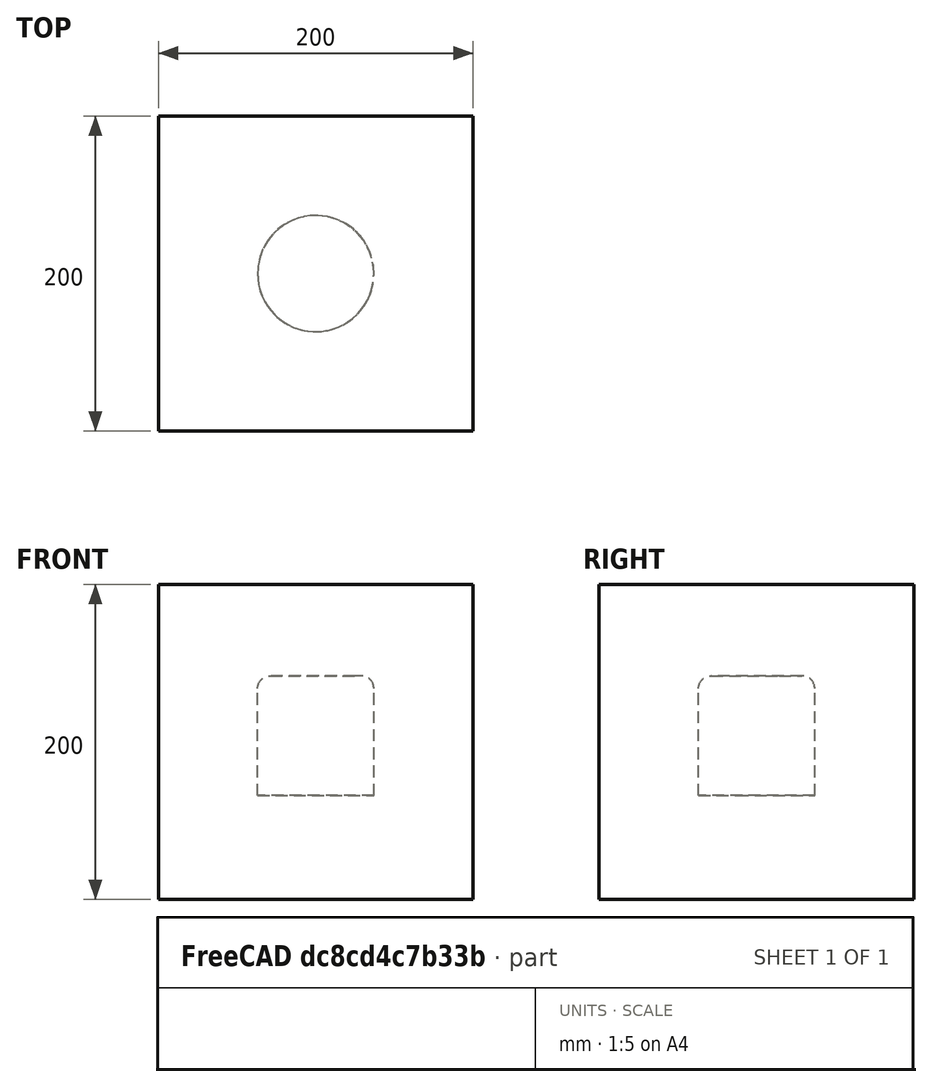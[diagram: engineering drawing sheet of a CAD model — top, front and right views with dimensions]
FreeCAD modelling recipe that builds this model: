
FCSTD DOCUMENT  (FreeCAD 1.0R39109 (Git))
Label: assemblyTest-B
License: All rights reserved
LicenseURL: http://en.wikipedia.org/wiki/All_rights_reserved
objects: App::DocumentObjectGroupPython×1254, Part::FeaturePython×4, App::Part×3, Part::Fuse×2
note: 6 computed .brp shape members not serialized (recipe doc carries the construction recipe); baked Part::Feature solids carry a one-line shape summary decoded from their .brp

FEATURE [App::DocumentObjectGroupPython] HALFPI  # scripted group (container) (typed FeaturePython)
  name = HALFPI
  value = pi/2.
FEATURE [App::DocumentObjectGroupPython] PI  # scripted group (container) (typed FeaturePython)
  name = PI
  value = 1.*pi
FEATURE [App::DocumentObjectGroupPython] TWOPI  # scripted group (container) (typed FeaturePython)
  name = TWOPI
  value = 2.*pi
FEATURE [App::DocumentObjectGroupPython] Variables  # scripted group (container) (typed FeaturePython)
FEATURE [App::DocumentObjectGroupPython] Quantities  # scripted group (container) (typed FeaturePython)
FEATURE [App::DocumentObjectGroupPython] Isotopes  # scripted group (container) (typed FeaturePython)
FEATURE [App::DocumentObjectGroupPython] Elements  # scripted group (container) (typed FeaturePython)
FEATURE [App::DocumentObjectGroupPython] G4Isotopes  # scripted group (container) (typed FeaturePython)
FEATURE [App::DocumentObjectGroupPython] H_element  # scripted group (container) (typed FeaturePython)
  Z = 1
  atom_value = 1.008
  formula = H
  name = H_element
FEATURE [App::DocumentObjectGroupPython] He_element  # scripted group (container) (typed FeaturePython)
  Z = 2
  atom_value = 4.0026
  formula = He
  name = He_element
FEATURE [App::DocumentObjectGroupPython] Li_element  # scripted group (container) (typed FeaturePython)
  Z = 3
  atom_value = 6.94
  formula = Li
  name = Li_element
FEATURE [App::DocumentObjectGroupPython] Be_element  # scripted group (container) (typed FeaturePython)
  Z = 4
  atom_value = 9.01218
  formula = Be
  name = Be_element
FEATURE [App::DocumentObjectGroupPython] B_element  # scripted group (container) (typed FeaturePython)
  Z = 5
  atom_value = 10.81
  formula = B
  name = B_element
FEATURE [App::DocumentObjectGroupPython] C_element  # scripted group (container) (typed FeaturePython)
  Z = 6
  atom_value = 12.011
  formula = C
  name = C_element
FEATURE [App::DocumentObjectGroupPython] N_element  # scripted group (container) (typed FeaturePython)
  Z = 7
  atom_value = 14.007
  formula = N
  name = N_element
FEATURE [App::DocumentObjectGroupPython] O_element  # scripted group (container) (typed FeaturePython)
  Z = 8
  atom_value = 15.999
  formula = O
  name = O_element
FEATURE [App::DocumentObjectGroupPython] F_element  # scripted group (container) (typed FeaturePython)
  Z = 9
  atom_value = 18.9984
  formula = F
  name = F_element
FEATURE [App::DocumentObjectGroupPython] Ne_element  # scripted group (container) (typed FeaturePython)
  Z = 10
  atom_value = 20.1797
  formula = Ne
  name = Ne_element
FEATURE [App::DocumentObjectGroupPython] Na_element  # scripted group (container) (typed FeaturePython)
  Z = 11
  atom_value = 22.9898
  formula = Na
  name = Na_element
FEATURE [App::DocumentObjectGroupPython] Mg_element  # scripted group (container) (typed FeaturePython)
  Z = 12
  atom_value = 24.305
  formula = Mg
  name = Mg_element
FEATURE [App::DocumentObjectGroupPython] Al_element  # scripted group (container) (typed FeaturePython)
  Z = 13
  atom_value = 26.9815
  formula = Al
  name = Al_element
FEATURE [App::DocumentObjectGroupPython] Si_element  # scripted group (container) (typed FeaturePython)
  Z = 14
  atom_value = 28.085
  formula = Si
  name = Si_element
FEATURE [App::DocumentObjectGroupPython] P_element  # scripted group (container) (typed FeaturePython)
  Z = 15
  atom_value = 30.9738
  formula = P
  name = P_element
FEATURE [App::DocumentObjectGroupPython] S_element  # scripted group (container) (typed FeaturePython)
  Z = 16
  atom_value = 32.06
  formula = S
  name = S_element
FEATURE [App::DocumentObjectGroupPython] Cl_element  # scripted group (container) (typed FeaturePython)
  Z = 17
  atom_value = 35.45
  formula = Cl
  name = Cl_element
FEATURE [App::DocumentObjectGroupPython] Ar_element  # scripted group (container) (typed FeaturePython)
  Z = 18
  atom_value = 39.95
  formula = Ar
  name = Ar_element
FEATURE [App::DocumentObjectGroupPython] K_element  # scripted group (container) (typed FeaturePython)
  Z = 19
  atom_value = 39.0983
  formula = K
  name = K_element
FEATURE [App::DocumentObjectGroupPython] Ca_element  # scripted group (container) (typed FeaturePython)
  Z = 20
  atom_value = 40.078
  formula = Ca
  name = Ca_element
FEATURE [App::DocumentObjectGroupPython] Sc_element  # scripted group (container) (typed FeaturePython)
  Z = 21
  atom_value = 44.9559
  formula = Sc
  name = Sc_element
FEATURE [App::DocumentObjectGroupPython] Ti_element  # scripted group (container) (typed FeaturePython)
  Z = 22
  atom_value = 47.867
  formula = Ti
  name = Ti_element
FEATURE [App::DocumentObjectGroupPython] V_element  # scripted group (container) (typed FeaturePython)
  Z = 23
  atom_value = 50.9415
  formula = V
  name = V_element
FEATURE [App::DocumentObjectGroupPython] Cr_element  # scripted group (container) (typed FeaturePython)
  Z = 24
  atom_value = 51.9961
  formula = Cr
  name = Cr_element
FEATURE [App::DocumentObjectGroupPython] Mn_element  # scripted group (container) (typed FeaturePython)
  Z = 25
  atom_value = 54.938
  formula = Mn
  name = Mn_element
FEATURE [App::DocumentObjectGroupPython] Fe_element  # scripted group (container) (typed FeaturePython)
  Z = 26
  atom_value = 55.845
  formula = Fe
  name = Fe_element
FEATURE [App::DocumentObjectGroupPython] Co_element  # scripted group (container) (typed FeaturePython)
  Z = 27
  atom_value = 58.9332
  formula = Co
  name = Co_element
FEATURE [App::DocumentObjectGroupPython] Ni_element  # scripted group (container) (typed FeaturePython)
  Z = 28
  atom_value = 58.6934
  formula = Ni
  name = Ni_element
FEATURE [App::DocumentObjectGroupPython] Cu_element  # scripted group (container) (typed FeaturePython)
  Z = 29
  atom_value = 63.546
  formula = Cu
  name = Cu_element
FEATURE [App::DocumentObjectGroupPython] Zn_element  # scripted group (container) (typed FeaturePython)
  Z = 30
  atom_value = 65.38
  formula = Zn
  name = Zn_element
FEATURE [App::DocumentObjectGroupPython] Ga_element  # scripted group (container) (typed FeaturePython)
  Z = 31
  atom_value = 69.723
  formula = Ga
  name = Ga_element
FEATURE [App::DocumentObjectGroupPython] Ge_element  # scripted group (container) (typed FeaturePython)
  Z = 32
  atom_value = 72.63
  formula = Ge
  name = Ge_element
FEATURE [App::DocumentObjectGroupPython] As_element  # scripted group (container) (typed FeaturePython)
  Z = 33
  atom_value = 74.9216
  formula = As
  name = As_element
FEATURE [App::DocumentObjectGroupPython] Se_element  # scripted group (container) (typed FeaturePython)
  Z = 34
  atom_value = 78.971
  formula = Se
  name = Se_element
FEATURE [App::DocumentObjectGroupPython] Br_element  # scripted group (container) (typed FeaturePython)
  Z = 35
  atom_value = 79.904
  formula = Br
  name = Br_element
FEATURE [App::DocumentObjectGroupPython] Kr_element  # scripted group (container) (typed FeaturePython)
  Z = 36
  atom_value = 83.798
  formula = Kr
  name = Kr_element
FEATURE [App::DocumentObjectGroupPython] Rb_element  # scripted group (container) (typed FeaturePython)
  Z = 37
  atom_value = 85.4678
  formula = Rb
  name = Rb_element
FEATURE [App::DocumentObjectGroupPython] Sr_element  # scripted group (container) (typed FeaturePython)
  Z = 38
  atom_value = 87.62
  formula = Sr
  name = Sr_element
FEATURE [App::DocumentObjectGroupPython] Y_element  # scripted group (container) (typed FeaturePython)
  Z = 39
  atom_value = 88.9058
  formula = Y
  name = Y_element
FEATURE [App::DocumentObjectGroupPython] Zr_element  # scripted group (container) (typed FeaturePython)
  Z = 40
  atom_value = 91.224
  formula = Zr
  name = Zr_element
FEATURE [App::DocumentObjectGroupPython] Nb_element  # scripted group (container) (typed FeaturePython)
  Z = 41
  atom_value = 92.9064
  formula = Nb
  name = Nb_element
FEATURE [App::DocumentObjectGroupPython] Mo_element  # scripted group (container) (typed FeaturePython)
  Z = 42
  atom_value = 95.95
  formula = Mo
  name = Mo_element
FEATURE [App::DocumentObjectGroupPython] Tc_element  # scripted group (container) (typed FeaturePython)
  Z = 43
  atom_value = 97
  formula = Tc
  name = Tc_element
FEATURE [App::DocumentObjectGroupPython] Ru_element  # scripted group (container) (typed FeaturePython)
  Z = 44
  atom_value = 101.07
  formula = Ru
  name = Ru_element
FEATURE [App::DocumentObjectGroupPython] Rh_element  # scripted group (container) (typed FeaturePython)
  Z = 45
  atom_value = 102.905
  formula = Rh
  name = Rh_element
FEATURE [App::DocumentObjectGroupPython] Pd_element  # scripted group (container) (typed FeaturePython)
  Z = 46
  atom_value = 106.42
  formula = Pd
  name = Pd_element
FEATURE [App::DocumentObjectGroupPython] Ag_element  # scripted group (container) (typed FeaturePython)
  Z = 47
  atom_value = 107.868
  formula = Ag
  name = Ag_element
FEATURE [App::DocumentObjectGroupPython] Cd_element  # scripted group (container) (typed FeaturePython)
  Z = 48
  atom_value = 112.414
  formula = Cd
  name = Cd_element
FEATURE [App::DocumentObjectGroupPython] In_element  # scripted group (container) (typed FeaturePython)
  Z = 49
  atom_value = 114.818
  formula = In
  name = In_element
FEATURE [App::DocumentObjectGroupPython] Sn_element  # scripted group (container) (typed FeaturePython)
  Z = 50
  atom_value = 118.71
  formula = Sn
  name = Sn_element
FEATURE [App::DocumentObjectGroupPython] Sb_element  # scripted group (container) (typed FeaturePython)
  Z = 51
  atom_value = 121.76
  formula = Sb
  name = Sb_element
FEATURE [App::DocumentObjectGroupPython] Te_element  # scripted group (container) (typed FeaturePython)
  Z = 52
  atom_value = 127.6
  formula = Te
  name = Te_element
FEATURE [App::DocumentObjectGroupPython] I_element  # scripted group (container) (typed FeaturePython)
  Z = 53
  atom_value = 126.904
  formula = I
  name = I_element
FEATURE [App::DocumentObjectGroupPython] Xe_element  # scripted group (container) (typed FeaturePython)
  Z = 54
  atom_value = 131.293
  formula = Xe
  name = Xe_element
FEATURE [App::DocumentObjectGroupPython] Cs_element  # scripted group (container) (typed FeaturePython)
  Z = 55
  atom_value = 132.905
  formula = Cs
  name = Cs_element
FEATURE [App::DocumentObjectGroupPython] Ba_element  # scripted group (container) (typed FeaturePython)
  Z = 56
  atom_value = 137.327
  formula = Ba
  name = Ba_element
FEATURE [App::DocumentObjectGroupPython] La_element  # scripted group (container) (typed FeaturePython)
  Z = 57
  atom_value = 138.905
  formula = La
  name = La_element
FEATURE [App::DocumentObjectGroupPython] Ce_element  # scripted group (container) (typed FeaturePython)
  Z = 58
  atom_value = 140.116
  formula = Ce
  name = Ce_element
FEATURE [App::DocumentObjectGroupPython] Pr_element  # scripted group (container) (typed FeaturePython)
  Z = 59
  atom_value = 140.908
  formula = Pr
  name = Pr_element
FEATURE [App::DocumentObjectGroupPython] Nd_element  # scripted group (container) (typed FeaturePython)
  Z = 60
  atom_value = 144.242
  formula = Nd
  name = Nd_element
FEATURE [App::DocumentObjectGroupPython] Pm_element  # scripted group (container) (typed FeaturePython)
  Z = 61
  atom_value = 145
  formula = Pm
  name = Pm_element
FEATURE [App::DocumentObjectGroupPython] Sm_element  # scripted group (container) (typed FeaturePython)
  Z = 62
  atom_value = 150.36
  formula = Sm
  name = Sm_element
FEATURE [App::DocumentObjectGroupPython] Eu_element  # scripted group (container) (typed FeaturePython)
  Z = 63
  atom_value = 151.964
  formula = Eu
  name = Eu_element
FEATURE [App::DocumentObjectGroupPython] Gd_element  # scripted group (container) (typed FeaturePython)
  Z = 64
  atom_value = 157.25
  formula = Gd
  name = Gd_element
FEATURE [App::DocumentObjectGroupPython] Tb_element  # scripted group (container) (typed FeaturePython)
  Z = 65
  atom_value = 158.925
  formula = Tb
  name = Tb_element
FEATURE [App::DocumentObjectGroupPython] Dy_element  # scripted group (container) (typed FeaturePython)
  Z = 66
  atom_value = 162.5
  formula = Dy
  name = Dy_element
FEATURE [App::DocumentObjectGroupPython] Ho_element  # scripted group (container) (typed FeaturePython)
  Z = 67
  atom_value = 164.93
  formula = Ho
  name = Ho_element
FEATURE [App::DocumentObjectGroupPython] Er_element  # scripted group (container) (typed FeaturePython)
  Z = 68
  atom_value = 167.259
  formula = Er
  name = Er_element
FEATURE [App::DocumentObjectGroupPython] Tm_element  # scripted group (container) (typed FeaturePython)
  Z = 69
  atom_value = 168.934
  formula = Tm
  name = Tm_element
FEATURE [App::DocumentObjectGroupPython] Yb_element  # scripted group (container) (typed FeaturePython)
  Z = 70
  atom_value = 173.045
  formula = Yb
  name = Yb_element
FEATURE [App::DocumentObjectGroupPython] Lu_element  # scripted group (container) (typed FeaturePython)
  Z = 71
  atom_value = 174.967
  formula = Lu
  name = Lu_element
FEATURE [App::DocumentObjectGroupPython] Hf_element  # scripted group (container) (typed FeaturePython)
  Z = 72
  atom_value = 178.49
  formula = Hf
  name = Hf_element
FEATURE [App::DocumentObjectGroupPython] Ta_element  # scripted group (container) (typed FeaturePython)
  Z = 73
  atom_value = 180.948
  formula = Ta
  name = Ta_element
FEATURE [App::DocumentObjectGroupPython] W_element  # scripted group (container) (typed FeaturePython)
  Z = 74
  atom_value = 183.84
  formula = W
  name = W_element
FEATURE [App::DocumentObjectGroupPython] Re_element  # scripted group (container) (typed FeaturePython)
  Z = 75
  atom_value = 186.207
  formula = Re
  name = Re_element
FEATURE [App::DocumentObjectGroupPython] Os_element  # scripted group (container) (typed FeaturePython)
  Z = 76
  atom_value = 190.23
  formula = Os
  name = Os_element
FEATURE [App::DocumentObjectGroupPython] Ir_element  # scripted group (container) (typed FeaturePython)
  Z = 77
  atom_value = 192.217
  formula = Ir
  name = Ir_element
FEATURE [App::DocumentObjectGroupPython] Pt_element  # scripted group (container) (typed FeaturePython)
  Z = 78
  atom_value = 195.084
  formula = Pt
  name = Pt_element
FEATURE [App::DocumentObjectGroupPython] Au_element  # scripted group (container) (typed FeaturePython)
  Z = 79
  atom_value = 196.967
  formula = Au
  name = Au_element
FEATURE [App::DocumentObjectGroupPython] Hg_element  # scripted group (container) (typed FeaturePython)
  Z = 80
  atom_value = 200.592
  formula = Hg
  name = Hg_element
FEATURE [App::DocumentObjectGroupPython] Tl_element  # scripted group (container) (typed FeaturePython)
  Z = 81
  atom_value = 204.38
  formula = Tl
  name = Tl_element
FEATURE [App::DocumentObjectGroupPython] Pb_element  # scripted group (container) (typed FeaturePython)
  Z = 82
  atom_value = 207.2
  formula = Pb
  name = Pb_element
FEATURE [App::DocumentObjectGroupPython] Bi_element  # scripted group (container) (typed FeaturePython)
  Z = 83
  atom_value = 208.98
  formula = Bi
  name = Bi_element
FEATURE [App::DocumentObjectGroupPython] Po_element  # scripted group (container) (typed FeaturePython)
  Z = 84
  atom_value = 209
  formula = Po
  name = Po_element
FEATURE [App::DocumentObjectGroupPython] At_element  # scripted group (container) (typed FeaturePython)
  Z = 85
  atom_value = 210
  formula = At
  name = At_element
FEATURE [App::DocumentObjectGroupPython] Rn_element  # scripted group (container) (typed FeaturePython)
  Z = 86
  atom_value = 222
  formula = Rn
  name = Rn_element
FEATURE [App::DocumentObjectGroupPython] Fr_element  # scripted group (container) (typed FeaturePython)
  Z = 87
  atom_value = 223
  formula = Fr
  name = Fr_element
FEATURE [App::DocumentObjectGroupPython] Ra_element  # scripted group (container) (typed FeaturePython)
  Z = 88
  atom_value = 226
  formula = Ra
  name = Ra_element
FEATURE [App::DocumentObjectGroupPython] Ac_element  # scripted group (container) (typed FeaturePython)
  Z = 89
  atom_value = 227
  formula = Ac
  name = Ac_element
FEATURE [App::DocumentObjectGroupPython] Th_element  # scripted group (container) (typed FeaturePython)
  Z = 90
  atom_value = 232.038
  formula = Th
  name = Th_element
FEATURE [App::DocumentObjectGroupPython] Pa_element  # scripted group (container) (typed FeaturePython)
  Z = 91
  atom_value = 231.036
  formula = Pa
  name = Pa_element
FEATURE [App::DocumentObjectGroupPython] U_element  # scripted group (container) (typed FeaturePython)
  Z = 92
  atom_value = 238.029
  formula = U
  name = U_element
FEATURE [App::DocumentObjectGroupPython] Np_element  # scripted group (container) (typed FeaturePython)
  Z = 93
  atom_value = 237
  formula = Np
  name = Np_element
FEATURE [App::DocumentObjectGroupPython] Pu_element  # scripted group (container) (typed FeaturePython)
  Z = 94
  atom_value = 244
  formula = Pu
  name = Pu_element
FEATURE [App::DocumentObjectGroupPython] Am_element  # scripted group (container) (typed FeaturePython)
  Z = 95
  atom_value = 243
  formula = Am
  name = Am_element
FEATURE [App::DocumentObjectGroupPython] Cm_element  # scripted group (container) (typed FeaturePython)
  Z = 96
  atom_value = 247
  formula = Cm
  name = Cm_element
FEATURE [App::DocumentObjectGroupPython] Bk_element  # scripted group (container) (typed FeaturePython)
  Z = 97
  atom_value = 247
  formula = Bk
  name = Bk_element
FEATURE [App::DocumentObjectGroupPython] Cf_element  # scripted group (container) (typed FeaturePython)
  Z = 98
  atom_value = 251
  formula = Cf
  name = Cf_element
FEATURE [App::DocumentObjectGroupPython] G4Elements  # scripted group (container) (typed FeaturePython)
  Group = -> [H_element,He_element,Li_element,Be_element,B_element,C_element,N_element,O_element,F_element,Ne_element,Na_element,Mg_element,Al_element,Si_element,P_element,S_element,Cl_element,Ar_element,K_element,Ca_element,Sc_element,Ti_element,V_element,Cr_element,Mn_element,Fe_element,Co_element,Ni_element,Cu_element,Zn_element,Ga_element,Ge_element,As_element,Se_element,Br_element,Kr_element,Rb_element,+61 more]
FEATURE [Part::FeaturePython] GDMLBox_WorldBox  # WARN: FeaturePython — macro-defined, semantics opaque (R4)
  lunit = 2
  material = 5
  x = 200
  y = 200
  z = 200
FEATURE [App::DocumentObjectGroupPython] HALFPI001  # scripted group (container) (typed FeaturePython)
  name = HALFPI
  value = pi/2.
FEATURE [App::DocumentObjectGroupPython] PI001  # scripted group (container) (typed FeaturePython)
  name = PI
  value = 1.*pi
FEATURE [App::DocumentObjectGroupPython] TWOPI001  # scripted group (container) (typed FeaturePython)
  name = TWOPI
  value = 2.*pi
FEATURE [App::DocumentObjectGroupPython] HALFPI001001  # scripted group (container) (typed FeaturePython)
  name = HALFPI001
  value = pi/2.
FEATURE [App::DocumentObjectGroupPython] PI001001  # scripted group (container) (typed FeaturePython)
  name = PI001
  value = 1.*pi
FEATURE [App::DocumentObjectGroupPython] TWOPI001001  # scripted group (container) (typed FeaturePython)
  name = TWOPI001
  value = 2.*pi
FEATURE [App::DocumentObjectGroupPython] Constants  # scripted group (container) (typed FeaturePython)
  Group = -> [HALFPI,PI,TWOPI,HALFPI001,PI001,TWOPI001,HALFPI001001,PI001001,TWOPI001001]
FEATURE [Part::FeaturePython] GDMLTorus_Torus  # WARN: FeaturePython — macro-defined, semantics opaque (R4)
  aunit = deg
  deltaphi = 360
  lunit = 2
  material = 0
  rmax = 8
  rmin = 0
  rtor = 28.9
  startphi = 0
FEATURE [Part::FeaturePython] GDMLTube_Tube  # WARN: FeaturePython — macro-defined, semantics opaque (R4)
  aunit = 1
  deltaphi = 360
  lunit = 2
  material = 0
  rmax = 28.9
  rmin = 0
  startphi = 0
  z = 16
FEATURE [Part::FeaturePython] GDMLTube_Tube001  label="GDMLTube_T_1"  # WARN: FeaturePython — macro-defined, semantics opaque (R4)
  Placement = pos=(0,0,-34) rot=(0,0,-1;0.349066rad)
  aunit = 1
  deltaphi = 360
  lunit = 2
  material = 0
  rmax = 36.9
  rmin = 0
  startphi = 0
  z = 68
FEATURE [Part::Fuse] Union
  Base = -> GDMLTorus_Torus
  Placement = pos=(0,0,0) rot=(0,0,1;0.523599rad)
  Tool = -> GDMLTube_Tube
FEATURE [Part::Fuse] Union001  label="U1"
  Base = -> Union
  Placement = pos=(0,0,34) rot=(0,0,1;0rad)
  Tool = -> GDMLTube_Tube001
  material = 211
FEATURE [App::Part] Bool_Union001  label="Detector"
  Group = -> [GDMLTorus_Torus,GDMLTube_Tube,Union,GDMLTube_Tube001,Union001]
  Origin = -> Origin005
FEATURE [App::Part] Part  label="DetectorAssembly"
  Group = -> [Bool_Union001]
  Origin = -> Origin007
FEATURE [App::Part] worldVOL
  Group = -> [GDMLBox_WorldBox,Part]
  Origin = -> Origin
FEATURE [App::DocumentObjectGroupPython] H_element553  label="H_element : 0.246"  # scripted group (container) (typed FeaturePython)
  n = 0.101327
FEATURE [App::DocumentObjectGroupPython] C_element593  label="C_element : 0.974"  # scripted group (container) (typed FeaturePython)
  n = 0.7755
FEATURE [App::DocumentObjectGroupPython] N_element273  label="N_element : 0.828"  # scripted group (container) (typed FeaturePython)
  n = 0.035057
FEATURE [App::DocumentObjectGroupPython] O_element521  label="O_element : 0.966"  # scripted group (container) (typed FeaturePython)
  n = 0.0523159
FEATURE [App::DocumentObjectGroupPython] F_element077  label="F_element : 0.727"  # scripted group (container) (typed FeaturePython)
  n = 0.017422
FEATURE [App::DocumentObjectGroupPython] Ca_element057  label="Ca_element : 0.240"  # scripted group (container) (typed FeaturePython)
  n = 0.018378
FEATURE [App::DocumentObjectGroupPython] G4_A_150_TISSUE  label="G4_A-150_TISSUE"  # scripted group (container) (typed FeaturePython)
  Dunit = g/cm3
  Dvalue = 1.127
  Group = -> [H_element553,C_element593,N_element273,O_element521,F_element077,Ca_element057]
  conduct = 2
  density = 1
  expand = 3
  formula = G4_A-150_TISSUE
  name = G4_A-150_TISSUE
  specific = 4
FEATURE [App::DocumentObjectGroupPython] C_element594  label="C_element : 390"  # scripted group (container) (typed FeaturePython)
  n = 3
  ref = C_element
FEATURE [App::DocumentObjectGroupPython] H_element554  label="H_element : 358"  # scripted group (container) (typed FeaturePython)
  n = 6
  ref = H_element
FEATURE [App::DocumentObjectGroupPython] O_element522  label="O_element : 335"  # scripted group (container) (typed FeaturePython)
  n = 1
  ref = O_element
FEATURE [App::DocumentObjectGroupPython] G4_ACETONE  # scripted group (container) (typed FeaturePython)
  Dunit = g/cm3
  Dvalue = 0.7899
  Group = -> [C_element594,H_element554,O_element522]
  conduct = 2
  density = 1
  expand = 3
  formula = G4_ACETONE
  name = G4_ACETONE
  specific = 4
FEATURE [App::DocumentObjectGroupPython] C_element595  label="C_element : 391"  # scripted group (container) (typed FeaturePython)
  n = 2
  ref = C_element
FEATURE [App::DocumentObjectGroupPython] H_element555  label="H_element : 359"  # scripted group (container) (typed FeaturePython)
  n = 2
  ref = H_element
FEATURE [App::DocumentObjectGroupPython] G4_ACETYLENE  # scripted group (container) (typed FeaturePython)
  Dunit = g/cm3
  Dvalue = 0.0010967
  Group = -> [C_element595,H_element555]
  conduct = 2
  density = 1
  expand = 3
  formula = G4_ACETYLENE
  name = G4_ACETYLENE
  specific = 4
FEATURE [App::DocumentObjectGroupPython] C_element596  label="C_element : 392"  # scripted group (container) (typed FeaturePython)
  n = 5
  ref = C_element
FEATURE [App::DocumentObjectGroupPython] H_element556  label="H_element : 360"  # scripted group (container) (typed FeaturePython)
  n = 5
  ref = H_element
FEATURE [App::DocumentObjectGroupPython] N_element274  label="N_element : 154"  # scripted group (container) (typed FeaturePython)
  n = 5
  ref = N_element
FEATURE [App::DocumentObjectGroupPython] G4_ADENINE  # scripted group (container) (typed FeaturePython)
  Dunit = g/cm3
  Dvalue = 1.6
  Group = -> [C_element596,H_element556,N_element274]
  conduct = 2
  density = 1
  expand = 3
  formula = G4_ADENINE
  name = G4_ADENINE
  specific = 4
FEATURE [App::DocumentObjectGroupPython] H_element557  label="H_element : 0.247"  # scripted group (container) (typed FeaturePython)
  n = 0.114
FEATURE [App::DocumentObjectGroupPython] C_element597  label="C_element : 0.975"  # scripted group (container) (typed FeaturePython)
  n = 0.598
FEATURE [App::DocumentObjectGroupPython] N_element275  label="N_element : 0.829"  # scripted group (container) (typed FeaturePython)
  n = 0.007
FEATURE [App::DocumentObjectGroupPython] O_element523  label="O_element : 0.967"  # scripted group (container) (typed FeaturePython)
  n = 0.278
FEATURE [App::DocumentObjectGroupPython] Na_element081  label="Na_element : 0.142"  # scripted group (container) (typed FeaturePython)
  n = 0.001
FEATURE [App::DocumentObjectGroupPython] S_element093  label="S_element : 0.065"  # scripted group (container) (typed FeaturePython)
  n = 0.001
FEATURE [App::DocumentObjectGroupPython] Cl_element121  label="Cl_element : 0.627"  # scripted group (container) (typed FeaturePython)
  n = 0.001
FEATURE [App::DocumentObjectGroupPython] G4_ADIPOSE_TISSUE_ICRP  # scripted group (container) (typed FeaturePython)
  Dunit = g/cm3
  Dvalue = 0.95
  Group = -> [H_element557,C_element597,N_element275,O_element523,Na_element081,S_element093,Cl_element121]
  conduct = 2
  density = 1
  expand = 3
  formula = G4_ADIPOSE_TISSUE_ICRP
  name = G4_ADIPOSE_TISSUE_ICRP
  specific = 4
FEATURE [App::DocumentObjectGroupPython] C_element598  label="C_element : 0.976"  # scripted group (container) (typed FeaturePython)
  n = 0.000124
FEATURE [App::DocumentObjectGroupPython] N_element276  label="N_element : 0.830"  # scripted group (container) (typed FeaturePython)
  n = 0.755268
FEATURE [App::DocumentObjectGroupPython] O_element524  label="O_element : 0.968"  # scripted group (container) (typed FeaturePython)
  n = 0.231781
FEATURE [App::DocumentObjectGroupPython] Ar_element009  label="Ar_element : 0.016"  # scripted group (container) (typed FeaturePython)
  n = 0.012827
FEATURE [App::DocumentObjectGroupPython] G4_AIR  # scripted group (container) (typed FeaturePython)
  Dunit = g/cm3
  Dvalue = 0.00120479
  Group = -> [C_element598,N_element276,O_element524,Ar_element009]
  conduct = 2
  density = 1
  expand = 3
  formula = G4_AIR
  name = G4_AIR
  specific = 4
FEATURE [App::DocumentObjectGroupPython] C_element599  label="C_element : 393"  # scripted group (container) (typed FeaturePython)
  n = 3
  ref = C_element
FEATURE [App::DocumentObjectGroupPython] H_element558  label="H_element : 361"  # scripted group (container) (typed FeaturePython)
  n = 7
  ref = H_element
FEATURE [App::DocumentObjectGroupPython] N_element277  label="N_element : 155"  # scripted group (container) (typed FeaturePython)
  n = 1
  ref = N_element
FEATURE [App::DocumentObjectGroupPython] O_element525  label="O_element : 336"  # scripted group (container) (typed FeaturePython)
  n = 2
  ref = O_element
FEATURE [App::DocumentObjectGroupPython] G4_ALANINE  # scripted group (container) (typed FeaturePython)
  Dunit = g/cm3
  Dvalue = 1.42
  Group = -> [C_element599,H_element558,N_element277,O_element525]
  conduct = 2
  density = 1
  expand = 3
  formula = G4_ALANINE
  name = G4_ALANINE
  specific = 4
FEATURE [App::DocumentObjectGroupPython] Al_element017  label="Al_element : 007"  # scripted group (container) (typed FeaturePython)
  n = 2
  ref = Al_element
FEATURE [App::DocumentObjectGroupPython] O_element526  label="O_element : 337"  # scripted group (container) (typed FeaturePython)
  n = 3
  ref = O_element
FEATURE [App::DocumentObjectGroupPython] G4_ALUMINUM_OXIDE  # scripted group (container) (typed FeaturePython)
  Dunit = g/cm3
  Dvalue = 3.97
  Group = -> [Al_element017,O_element526]
  conduct = 2
  density = 1
  expand = 3
  formula = G4_ALUMINUM_OXIDE
  name = G4_ALUMINUM_OXIDE
  specific = 4
FEATURE [App::DocumentObjectGroupPython] H_element559  label="H_element : 0.248"  # scripted group (container) (typed FeaturePython)
  n = 0.10593
FEATURE [App::DocumentObjectGroupPython] C_element600  label="C_element : 0.977"  # scripted group (container) (typed FeaturePython)
  n = 0.788974
FEATURE [App::DocumentObjectGroupPython] O_element527  label="O_element : 0.969"  # scripted group (container) (typed FeaturePython)
  n = 0.105096
FEATURE [App::DocumentObjectGroupPython] G4_AMBER  # scripted group (container) (typed FeaturePython)
  Dunit = g/cm3
  Dvalue = 1.1
  Group = -> [H_element559,C_element600,O_element527]
  conduct = 2
  density = 1
  expand = 3
  formula = G4_AMBER
  name = G4_AMBER
  specific = 4
FEATURE [App::DocumentObjectGroupPython] N_element278  label="N_element : 156"  # scripted group (container) (typed FeaturePython)
  n = 1
  ref = N_element
FEATURE [App::DocumentObjectGroupPython] H_element560  label="H_element : 362"  # scripted group (container) (typed FeaturePython)
  n = 3
  ref = H_element
FEATURE [App::DocumentObjectGroupPython] G4_AMMONIA  # scripted group (container) (typed FeaturePython)
  Dunit = g/cm3
  Dvalue = 0.000826019
  Group = -> [N_element278,H_element560]
  conduct = 2
  density = 1
  expand = 3
  formula = G4_AMMONIA
  name = G4_AMMONIA
  specific = 4
FEATURE [App::DocumentObjectGroupPython] C_element601  label="C_element : 394"  # scripted group (container) (typed FeaturePython)
  n = 6
  ref = C_element
FEATURE [App::DocumentObjectGroupPython] H_element561  label="H_element : 363"  # scripted group (container) (typed FeaturePython)
  n = 7
  ref = H_element
FEATURE [App::DocumentObjectGroupPython] N_element279  label="N_element : 157"  # scripted group (container) (typed FeaturePython)
  n = 1
  ref = N_element
FEATURE [App::DocumentObjectGroupPython] G4_ANILINE  # scripted group (container) (typed FeaturePython)
  Dunit = g/cm3
  Dvalue = 1.0235
  Group = -> [C_element601,H_element561,N_element279]
  conduct = 2
  density = 1
  expand = 3
  formula = G4_ANILINE
  name = G4_ANILINE
  specific = 4
FEATURE [App::DocumentObjectGroupPython] C_element602  label="C_element : 395"  # scripted group (container) (typed FeaturePython)
  n = 14
  ref = C_element
FEATURE [App::DocumentObjectGroupPython] H_element562  label="H_element : 364"  # scripted group (container) (typed FeaturePython)
  n = 10
  ref = H_element
FEATURE [App::DocumentObjectGroupPython] G4_ANTHRACENE  # scripted group (container) (typed FeaturePython)
  Dunit = g/cm3
  Dvalue = 1.283
  Group = -> [C_element602,H_element562]
  conduct = 2
  density = 1
  expand = 3
  formula = G4_ANTHRACENE
  name = G4_ANTHRACENE
  specific = 4
FEATURE [App::DocumentObjectGroupPython] H_element563  label="H_element : 0.249"  # scripted group (container) (typed FeaturePython)
  n = 0.0654709
FEATURE [App::DocumentObjectGroupPython] C_element603  label="C_element : 0.978"  # scripted group (container) (typed FeaturePython)
  n = 0.536944
FEATURE [App::DocumentObjectGroupPython] N_element280  label="N_element : 0.831"  # scripted group (container) (typed FeaturePython)
  n = 0.0215
FEATURE [App::DocumentObjectGroupPython] O_element528  label="O_element : 0.970"  # scripted group (container) (typed FeaturePython)
  n = 0.032085
FEATURE [App::DocumentObjectGroupPython] F_element078  label="F_element : 0.728"  # scripted group (container) (typed FeaturePython)
  n = 0.167411
FEATURE [App::DocumentObjectGroupPython] Ca_element058  label="Ca_element : 0.241"  # scripted group (container) (typed FeaturePython)
  n = 0.176589
FEATURE [App::DocumentObjectGroupPython] G4_B_100_BONE  label="G4_B-100_BONE"  # scripted group (container) (typed FeaturePython)
  Dunit = g/cm3
  Dvalue = 1.45
  Group = -> [H_element563,C_element603,N_element280,O_element528,F_element078,Ca_element058]
  conduct = 2
  density = 1
  expand = 3
  formula = G4_B-100_BONE
  name = G4_B-100_BONE
  specific = 4
FEATURE [App::DocumentObjectGroupPython] H_element564  label="H_element : 0.250"  # scripted group (container) (typed FeaturePython)
  n = 0.057441
FEATURE [App::DocumentObjectGroupPython] C_element604  label="C_element : 0.979"  # scripted group (container) (typed FeaturePython)
  n = 0.774591
FEATURE [App::DocumentObjectGroupPython] O_element529  label="O_element : 0.971"  # scripted group (container) (typed FeaturePython)
  n = 0.167968
FEATURE [App::DocumentObjectGroupPython] G4_BAKELITE  # scripted group (container) (typed FeaturePython)
  Dunit = g/cm3
  Dvalue = 1.25
  Group = -> [H_element564,C_element604,O_element529]
  conduct = 2
  density = 1
  expand = 3
  formula = G4_BAKELITE
  name = G4_BAKELITE
  specific = 4
FEATURE [App::DocumentObjectGroupPython] Ba_element013  label="Ba_element : 012"  # scripted group (container) (typed FeaturePython)
  n = 1
  ref = Ba_element
FEATURE [App::DocumentObjectGroupPython] F_element079  label="F_element : 037"  # scripted group (container) (typed FeaturePython)
  n = 2
  ref = F_element
FEATURE [App::DocumentObjectGroupPython] G4_BARIUM_FLUORIDE  # scripted group (container) (typed FeaturePython)
  Dunit = g/cm3
  Dvalue = 4.89
  Group = -> [Ba_element013,F_element079]
  conduct = 2
  density = 1
  expand = 3
  formula = G4_BARIUM_FLUORIDE
  name = G4_BARIUM_FLUORIDE
  specific = 4
FEATURE [App::DocumentObjectGroupPython] Ba_element014  label="Ba_element : 013"  # scripted group (container) (typed FeaturePython)
  n = 1
  ref = Ba_element
FEATURE [App::DocumentObjectGroupPython] S_element094  label="S_element : 028"  # scripted group (container) (typed FeaturePython)
  n = 1
  ref = S_element
FEATURE [App::DocumentObjectGroupPython] O_element530  label="O_element : 338"  # scripted group (container) (typed FeaturePython)
  n = 4
  ref = O_element
FEATURE [App::DocumentObjectGroupPython] G4_BARIUM_SULFATE  # scripted group (container) (typed FeaturePython)
  Dunit = g/cm3
  Dvalue = 4.5
  Group = -> [Ba_element014,S_element094,O_element530]
  conduct = 2
  density = 1
  expand = 3
  formula = G4_BARIUM_SULFATE
  name = G4_BARIUM_SULFATE
  specific = 4
FEATURE [App::DocumentObjectGroupPython] C_element605  label="C_element : 396"  # scripted group (container) (typed FeaturePython)
  n = 6
  ref = C_element
FEATURE [App::DocumentObjectGroupPython] H_element565  label="H_element : 365"  # scripted group (container) (typed FeaturePython)
  n = 6
  ref = H_element
FEATURE [App::DocumentObjectGroupPython] G4_BENZENE  # scripted group (container) (typed FeaturePython)
  Dunit = g/cm3
  Dvalue = 0.87865
  Group = -> [C_element605,H_element565]
  conduct = 2
  density = 1
  expand = 3
  formula = G4_BENZENE
  name = G4_BENZENE
  specific = 4
FEATURE [App::DocumentObjectGroupPython] Be_element009  label="Be_element : 008"  # scripted group (container) (typed FeaturePython)
  n = 1
  ref = Be_element
FEATURE [App::DocumentObjectGroupPython] O_element531  label="O_element : 339"  # scripted group (container) (typed FeaturePython)
  n = 1
  ref = O_element
FEATURE [App::DocumentObjectGroupPython] G4_BERYLLIUM_OXIDE  # scripted group (container) (typed FeaturePython)
  Dunit = g/cm3
  Dvalue = 3.01
  Group = -> [Be_element009,O_element531]
  conduct = 2
  density = 1
  expand = 3
  formula = G4_BERYLLIUM_OXIDE
  name = G4_BERYLLIUM_OXIDE
  specific = 4
FEATURE [App::DocumentObjectGroupPython] Bi_element009  label="Bi_element : 009"  # scripted group (container) (typed FeaturePython)
  n = 4
  ref = Bi_element
FEATURE [App::DocumentObjectGroupPython] Ge_element009  label="Ge_element : 008"  # scripted group (container) (typed FeaturePython)
  n = 3
  ref = Ge_element
FEATURE [App::DocumentObjectGroupPython] O_element532  label="O_element : 340"  # scripted group (container) (typed FeaturePython)
  n = 12
  ref = O_element
FEATURE [App::DocumentObjectGroupPython] G4_BGO  # scripted group (container) (typed FeaturePython)
  Dunit = g/cm3
  Dvalue = 7.13
  Group = -> [Bi_element009,Ge_element009,O_element532]
  conduct = 2
  density = 1
  expand = 3
  formula = G4_BGO
  name = G4_BGO
  specific = 4
FEATURE [App::DocumentObjectGroupPython] H_element566  label="H_element : 0.251"  # scripted group (container) (typed FeaturePython)
  n = 0.102
FEATURE [App::DocumentObjectGroupPython] C_element606  label="C_element : 0.980"  # scripted group (container) (typed FeaturePython)
  n = 0.11
FEATURE [App::DocumentObjectGroupPython] N_element281  label="N_element : 0.832"  # scripted group (container) (typed FeaturePython)
  n = 0.033
FEATURE [App::DocumentObjectGroupPython] O_element533  label="O_element : 0.972"  # scripted group (container) (typed FeaturePython)
  n = 0.745
FEATURE [App::DocumentObjectGroupPython] Na_element082  label="Na_element : 0.143"  # scripted group (container) (typed FeaturePython)
  n = 0.001
FEATURE [App::DocumentObjectGroupPython] P_element077  label="P_element : 0.138"  # scripted group (container) (typed FeaturePython)
  n = 0.001
FEATURE [App::DocumentObjectGroupPython] S_element095  label="S_element : 0.066"  # scripted group (container) (typed FeaturePython)
  n = 0.002
FEATURE [App::DocumentObjectGroupPython] Cl_element122  label="Cl_element : 0.628"  # scripted group (container) (typed FeaturePython)
  n = 0.003
FEATURE [App::DocumentObjectGroupPython] K_element053  label="K_element : 0.044"  # scripted group (container) (typed FeaturePython)
  n = 0.002
FEATURE [App::DocumentObjectGroupPython] Fe_element033  label="Fe_element : 0.021"  # scripted group (container) (typed FeaturePython)
  n = 0.001
FEATURE [App::DocumentObjectGroupPython] G4_BLOOD_ICRP  # scripted group (container) (typed FeaturePython)
  Dunit = g/cm3
  Dvalue = 1.06
  Group = -> [H_element566,C_element606,N_element281,O_element533,Na_element082,P_element077,S_element095,Cl_element122,K_element053,Fe_element033]
  conduct = 2
  density = 1
  expand = 3
  formula = G4_BLOOD_ICRP
  name = G4_BLOOD_ICRP
  specific = 4
FEATURE [App::DocumentObjectGroupPython] H_element567  label="H_element : 0.252"  # scripted group (container) (typed FeaturePython)
  n = 0.064
FEATURE [App::DocumentObjectGroupPython] C_element607  label="C_element : 0.981"  # scripted group (container) (typed FeaturePython)
  n = 0.278
FEATURE [App::DocumentObjectGroupPython] N_element282  label="N_element : 0.833"  # scripted group (container) (typed FeaturePython)
  n = 0.027
FEATURE [App::DocumentObjectGroupPython] O_element534  label="O_element : 0.973"  # scripted group (container) (typed FeaturePython)
  n = 0.41
FEATURE [App::DocumentObjectGroupPython] Mg_element045  label="Mg_element : 0.150"  # scripted group (container) (typed FeaturePython)
  n = 0.002
FEATURE [App::DocumentObjectGroupPython] P_element078  label="P_element : 0.139"  # scripted group (container) (typed FeaturePython)
  n = 0.07
FEATURE [App::DocumentObjectGroupPython] S_element096  label="S_element : 0.067"  # scripted group (container) (typed FeaturePython)
  n = 0.002
FEATURE [App::DocumentObjectGroupPython] Ca_element059  label="Ca_element : 0.242"  # scripted group (container) (typed FeaturePython)
  n = 0.147
FEATURE [App::DocumentObjectGroupPython] G4_BONE_COMPACT_ICRU  # scripted group (container) (typed FeaturePython)
  Dunit = g/cm3
  Dvalue = 1.85
  Group = -> [H_element567,C_element607,N_element282,O_element534,Mg_element045,P_element078,S_element096,Ca_element059]
  conduct = 2
  density = 1
  expand = 3
  formula = G4_BONE_COMPACT_ICRU
  name = G4_BONE_COMPACT_ICRU
  specific = 4
FEATURE [App::DocumentObjectGroupPython] H_element568  label="H_element : 0.253"  # scripted group (container) (typed FeaturePython)
  n = 0.034
FEATURE [App::DocumentObjectGroupPython] C_element608  label="C_element : 0.982"  # scripted group (container) (typed FeaturePython)
  n = 0.155
FEATURE [App::DocumentObjectGroupPython] N_element283  label="N_element : 0.834"  # scripted group (container) (typed FeaturePython)
  n = 0.042
FEATURE [App::DocumentObjectGroupPython] O_element535  label="O_element : 0.974"  # scripted group (container) (typed FeaturePython)
  n = 0.435
FEATURE [App::DocumentObjectGroupPython] Na_element083  label="Na_element : 0.144"  # scripted group (container) (typed FeaturePython)
  n = 0.001
FEATURE [App::DocumentObjectGroupPython] Mg_element046  label="Mg_element : 0.151"  # scripted group (container) (typed FeaturePython)
  n = 0.002
FEATURE [App::DocumentObjectGroupPython] P_element079  label="P_element : 0.140"  # scripted group (container) (typed FeaturePython)
  n = 0.103
FEATURE [App::DocumentObjectGroupPython] S_element097  label="S_element : 0.068"  # scripted group (container) (typed FeaturePython)
  n = 0.003
FEATURE [App::DocumentObjectGroupPython] Ca_element060  label="Ca_element : 0.243"  # scripted group (container) (typed FeaturePython)
  n = 0.225
FEATURE [App::DocumentObjectGroupPython] G4_BONE_CORTICAL_ICRP  # scripted group (container) (typed FeaturePython)
  Dunit = g/cm3
  Dvalue = 1.92
  Group = -> [H_element568,C_element608,N_element283,O_element535,Na_element083,Mg_element046,P_element079,S_element097,Ca_element060]
  conduct = 2
  density = 1
  expand = 3
  formula = G4_BONE_CORTICAL_ICRP
  name = G4_BONE_CORTICAL_ICRP
  specific = 4
FEATURE [App::DocumentObjectGroupPython] B_element029  label="B_element : 023"  # scripted group (container) (typed FeaturePython)
  n = 4
  ref = B_element
FEATURE [App::DocumentObjectGroupPython] C_element609  label="C_element : 397"  # scripted group (container) (typed FeaturePython)
  n = 1
  ref = C_element
FEATURE [App::DocumentObjectGroupPython] G4_BORON_CARBIDE  # scripted group (container) (typed FeaturePython)
  Dunit = g/cm3
  Dvalue = 2.52
  Group = -> [B_element029,C_element609]
  conduct = 2
  density = 1
  expand = 3
  formula = G4_BORON_CARBIDE
  name = G4_BORON_CARBIDE
  specific = 4
FEATURE [App::DocumentObjectGroupPython] B_element030  label="B_element : 024"  # scripted group (container) (typed FeaturePython)
  n = 2
  ref = B_element
FEATURE [App::DocumentObjectGroupPython] O_element536  label="O_element : 341"  # scripted group (container) (typed FeaturePython)
  n = 3
  ref = O_element
FEATURE [App::DocumentObjectGroupPython] G4_BORON_OXIDE  # scripted group (container) (typed FeaturePython)
  Dunit = g/cm3
  Dvalue = 1.812
  Group = -> [B_element030,O_element536]
  conduct = 2
  density = 1
  expand = 3
  formula = G4_BORON_OXIDE
  name = G4_BORON_OXIDE
  specific = 4
FEATURE [App::DocumentObjectGroupPython] H_element569  label="H_element : 0.254"  # scripted group (container) (typed FeaturePython)
  n = 0.107
FEATURE [App::DocumentObjectGroupPython] C_element610  label="C_element : 0.983"  # scripted group (container) (typed FeaturePython)
  n = 0.145
FEATURE [App::DocumentObjectGroupPython] N_element284  label="N_element : 0.835"  # scripted group (container) (typed FeaturePython)
  n = 0.022
FEATURE [App::DocumentObjectGroupPython] O_element537  label="O_element : 0.975"  # scripted group (container) (typed FeaturePython)
  n = 0.712
FEATURE [App::DocumentObjectGroupPython] Na_element084  label="Na_element : 0.145"  # scripted group (container) (typed FeaturePython)
  n = 0.002
FEATURE [App::DocumentObjectGroupPython] P_element080  label="P_element : 0.141"  # scripted group (container) (typed FeaturePython)
  n = 0.004
FEATURE [App::DocumentObjectGroupPython] S_element098  label="S_element : 0.069"  # scripted group (container) (typed FeaturePython)
  n = 0.002
FEATURE [App::DocumentObjectGroupPython] Cl_element123  label="Cl_element : 0.629"  # scripted group (container) (typed FeaturePython)
  n = 0.003
FEATURE [App::DocumentObjectGroupPython] K_element054  label="K_element : 0.045"  # scripted group (container) (typed FeaturePython)
  n = 0.003
FEATURE [App::DocumentObjectGroupPython] G4_BRAIN_ICRP  # scripted group (container) (typed FeaturePython)
  Dunit = g/cm3
  Dvalue = 1.04
  Group = -> [H_element569,C_element610,N_element284,O_element537,Na_element084,P_element080,S_element098,Cl_element123,K_element054]
  conduct = 2
  density = 1
  expand = 3
  formula = G4_BRAIN_ICRP
  name = G4_BRAIN_ICRP
  specific = 4
FEATURE [App::DocumentObjectGroupPython] C_element611  label="C_element : 398"  # scripted group (container) (typed FeaturePython)
  n = 4
  ref = C_element
FEATURE [App::DocumentObjectGroupPython] H_element570  label="H_element : 366"  # scripted group (container) (typed FeaturePython)
  n = 10
  ref = H_element
FEATURE [App::DocumentObjectGroupPython] G4_BUTANE  # scripted group (container) (typed FeaturePython)
  Dunit = g/cm3
  Dvalue = 0.00249343
  Group = -> [C_element611,H_element570]
  conduct = 2
  density = 1
  expand = 3
  formula = G4_BUTANE
  name = G4_BUTANE
  specific = 4
FEATURE [App::DocumentObjectGroupPython] C_element612  label="C_element : 399"  # scripted group (container) (typed FeaturePython)
  n = 4
  ref = C_element
FEATURE [App::DocumentObjectGroupPython] H_element571  label="H_element : 367"  # scripted group (container) (typed FeaturePython)
  n = 10
  ref = H_element
FEATURE [App::DocumentObjectGroupPython] O_element538  label="O_element : 342"  # scripted group (container) (typed FeaturePython)
  n = 1
  ref = O_element
FEATURE [App::DocumentObjectGroupPython] G4_N_BUTYL_ALCOHOL  label="G4_N-BUTYL_ALCOHOL"  # scripted group (container) (typed FeaturePython)
  Dunit = g/cm3
  Dvalue = 0.8098
  Group = -> [C_element612,H_element571,O_element538]
  conduct = 2
  density = 1
  expand = 3
  formula = G4_N-BUTYL_ALCOHOL
  name = G4_N-BUTYL_ALCOHOL
  specific = 4
FEATURE [App::DocumentObjectGroupPython] H_element572  label="H_element : 0.255"  # scripted group (container) (typed FeaturePython)
  n = 0.02468
FEATURE [App::DocumentObjectGroupPython] C_element613  label="C_element : 0.984"  # scripted group (container) (typed FeaturePython)
  n = 0.501611
FEATURE [App::DocumentObjectGroupPython] O_element539  label="O_element : 0.976"  # scripted group (container) (typed FeaturePython)
  n = 0.004527
FEATURE [App::DocumentObjectGroupPython] F_element080  label="F_element : 0.729"  # scripted group (container) (typed FeaturePython)
  n = 0.465209
FEATURE [App::DocumentObjectGroupPython] Si_element029  label="Si_element : 0.390"  # scripted group (container) (typed FeaturePython)
  n = 0.003973
FEATURE [App::DocumentObjectGroupPython] G4_C_552  label="G4_C-552"  # scripted group (container) (typed FeaturePython)
  Dunit = g/cm3
  Dvalue = 1.76
  Group = -> [H_element572,C_element613,O_element539,F_element080,Si_element029]
  conduct = 2
  density = 1
  expand = 3
  formula = G4_C-552
  name = G4_C-552
  specific = 4
FEATURE [App::DocumentObjectGroupPython] Cd_element013  label="Cd_element : 012"  # scripted group (container) (typed FeaturePython)
  n = 1
  ref = Cd_element
FEATURE [App::DocumentObjectGroupPython] Te_element009  label="Te_element : 008"  # scripted group (container) (typed FeaturePython)
  n = 1
  ref = Te_element
FEATURE [App::DocumentObjectGroupPython] G4_CADMIUM_TELLURIDE  # scripted group (container) (typed FeaturePython)
  Dunit = g/cm3
  Dvalue = 6.2
  Group = -> [Cd_element013,Te_element009]
  conduct = 2
  density = 1
  expand = 3
  formula = G4_CADMIUM_TELLURIDE
  name = G4_CADMIUM_TELLURIDE
  specific = 4
FEATURE [App::DocumentObjectGroupPython] Cd_element014  label="Cd_element : 013"  # scripted group (container) (typed FeaturePython)
  n = 1
  ref = Cd_element
FEATURE [App::DocumentObjectGroupPython] W_element021  label="W_element : 020"  # scripted group (container) (typed FeaturePython)
  n = 1
  ref = W_element
FEATURE [App::DocumentObjectGroupPython] O_element540  label="O_element : 343"  # scripted group (container) (typed FeaturePython)
  n = 4
  ref = O_element
FEATURE [App::DocumentObjectGroupPython] G4_CADMIUM_TUNGSTATE  # scripted group (container) (typed FeaturePython)
  Dunit = g/cm3
  Dvalue = 7.9
  Group = -> [Cd_element014,W_element021,O_element540]
  conduct = 2
  density = 1
  expand = 3
  formula = G4_CADMIUM_TUNGSTATE
  name = G4_CADMIUM_TUNGSTATE
  specific = 4
FEATURE [App::DocumentObjectGroupPython] Ca_element061  label="Ca_element : 028"  # scripted group (container) (typed FeaturePython)
  n = 1
  ref = Ca_element
FEATURE [App::DocumentObjectGroupPython] C_element614  label="C_element : 400"  # scripted group (container) (typed FeaturePython)
  n = 1
  ref = C_element
FEATURE [App::DocumentObjectGroupPython] O_element541  label="O_element : 344"  # scripted group (container) (typed FeaturePython)
  n = 3
  ref = O_element
FEATURE [App::DocumentObjectGroupPython] G4_CALCIUM_CARBONATE  # scripted group (container) (typed FeaturePython)
  Dunit = g/cm3
  Dvalue = 2.8
  Group = -> [Ca_element061,C_element614,O_element541]
  conduct = 2
  density = 1
  expand = 3
  formula = G4_CALCIUM_CARBONATE
  name = G4_CALCIUM_CARBONATE
  specific = 4
FEATURE [App::DocumentObjectGroupPython] Ca_element062  label="Ca_element : 029"  # scripted group (container) (typed FeaturePython)
  n = 1
  ref = Ca_element
FEATURE [App::DocumentObjectGroupPython] F_element081  label="F_element : 038"  # scripted group (container) (typed FeaturePython)
  n = 2
  ref = F_element
FEATURE [App::DocumentObjectGroupPython] G4_CALCIUM_FLUORIDE  # scripted group (container) (typed FeaturePython)
  Dunit = g/cm3
  Dvalue = 3.18
  Group = -> [Ca_element062,F_element081]
  conduct = 2
  density = 1
  expand = 3
  formula = G4_CALCIUM_FLUORIDE
  name = G4_CALCIUM_FLUORIDE
  specific = 4
FEATURE [App::DocumentObjectGroupPython] Ca_element063  label="Ca_element : 030"  # scripted group (container) (typed FeaturePython)
  n = 1
  ref = Ca_element
FEATURE [App::DocumentObjectGroupPython] O_element542  label="O_element : 345"  # scripted group (container) (typed FeaturePython)
  n = 1
  ref = O_element
FEATURE [App::DocumentObjectGroupPython] G4_CALCIUM_OXIDE  # scripted group (container) (typed FeaturePython)
  Dunit = g/cm3
  Dvalue = 3.3
  Group = -> [Ca_element063,O_element542]
  conduct = 2
  density = 1
  expand = 3
  formula = G4_CALCIUM_OXIDE
  name = G4_CALCIUM_OXIDE
  specific = 4
FEATURE [App::DocumentObjectGroupPython] Ca_element064  label="Ca_element : 031"  # scripted group (container) (typed FeaturePython)
  n = 1
  ref = Ca_element
FEATURE [App::DocumentObjectGroupPython] S_element099  label="S_element : 029"  # scripted group (container) (typed FeaturePython)
  n = 1
  ref = S_element
FEATURE [App::DocumentObjectGroupPython] O_element543  label="O_element : 346"  # scripted group (container) (typed FeaturePython)
  n = 4
  ref = O_element
FEATURE [App::DocumentObjectGroupPython] G4_CALCIUM_SULFATE  # scripted group (container) (typed FeaturePython)
  Dunit = g/cm3
  Dvalue = 2.96
  Group = -> [Ca_element064,S_element099,O_element543]
  conduct = 2
  density = 1
  expand = 3
  formula = G4_CALCIUM_SULFATE
  name = G4_CALCIUM_SULFATE
  specific = 4
FEATURE [App::DocumentObjectGroupPython] Ca_element065  label="Ca_element : 032"  # scripted group (container) (typed FeaturePython)
  n = 1
  ref = Ca_element
FEATURE [App::DocumentObjectGroupPython] W_element022  label="W_element : 021"  # scripted group (container) (typed FeaturePython)
  n = 1
  ref = W_element
FEATURE [App::DocumentObjectGroupPython] O_element544  label="O_element : 347"  # scripted group (container) (typed FeaturePython)
  n = 4
  ref = O_element
FEATURE [App::DocumentObjectGroupPython] G4_CALCIUM_TUNGSTATE  # scripted group (container) (typed FeaturePython)
  Dunit = g/cm3
  Dvalue = 6.062
  Group = -> [Ca_element065,W_element022,O_element544]
  conduct = 2
  density = 1
  expand = 3
  formula = G4_CALCIUM_TUNGSTATE
  name = G4_CALCIUM_TUNGSTATE
  specific = 4
FEATURE [App::DocumentObjectGroupPython] C_element615  label="C_element : 401"  # scripted group (container) (typed FeaturePython)
  n = 1
  ref = C_element
FEATURE [App::DocumentObjectGroupPython] O_element545  label="O_element : 348"  # scripted group (container) (typed FeaturePython)
  n = 2
  ref = O_element
FEATURE [App::DocumentObjectGroupPython] G4_CARBON_DIOXIDE  # scripted group (container) (typed FeaturePython)
  Dunit = g/cm3
  Dvalue = 0.00184212
  Group = -> [C_element615,O_element545]
  conduct = 2
  density = 1
  expand = 3
  formula = G4_CARBON_DIOXIDE
  name = G4_CARBON_DIOXIDE
  specific = 4
FEATURE [App::DocumentObjectGroupPython] C_element616  label="C_element : 402"  # scripted group (container) (typed FeaturePython)
  n = 1
  ref = C_element
FEATURE [App::DocumentObjectGroupPython] Cl_element124  label="Cl_element : 061"  # scripted group (container) (typed FeaturePython)
  n = 4
  ref = Cl_element
FEATURE [App::DocumentObjectGroupPython] G4_CARBON_TETRACHLORIDE  # scripted group (container) (typed FeaturePython)
  Dunit = g/cm3
  Dvalue = 1.594
  Group = -> [C_element616,Cl_element124]
  conduct = 2
  density = 1
  expand = 3
  formula = G4_CARBON_TETRACHLORIDE
  name = G4_CARBON_TETRACHLORIDE
  specific = 4
FEATURE [App::DocumentObjectGroupPython] C_element617  label="C_element : 403"  # scripted group (container) (typed FeaturePython)
  n = 6
  ref = C_element
FEATURE [App::DocumentObjectGroupPython] H_element573  label="H_element : 368"  # scripted group (container) (typed FeaturePython)
  n = 10
  ref = H_element
FEATURE [App::DocumentObjectGroupPython] O_element546  label="O_element : 349"  # scripted group (container) (typed FeaturePython)
  n = 5
  ref = O_element
FEATURE [App::DocumentObjectGroupPython] G4_CELLULOSE_CELLOPHANE  # scripted group (container) (typed FeaturePython)
  Dunit = g/cm3
  Dvalue = 1.42
  Group = -> [C_element617,H_element573,O_element546]
  conduct = 2
  density = 1
  expand = 3
  formula = G4_CELLULOSE_CELLOPHANE
  name = G4_CELLULOSE_CELLOPHANE
  specific = 4
FEATURE [App::DocumentObjectGroupPython] H_element574  label="H_element : 0.256"  # scripted group (container) (typed FeaturePython)
  n = 0.067125
FEATURE [App::DocumentObjectGroupPython] C_element618  label="C_element : 0.985"  # scripted group (container) (typed FeaturePython)
  n = 0.545403
FEATURE [App::DocumentObjectGroupPython] O_element547  label="O_element : 0.977"  # scripted group (container) (typed FeaturePython)
  n = 0.387472
FEATURE [App::DocumentObjectGroupPython] G4_CELLULOSE_BUTYRATE  # scripted group (container) (typed FeaturePython)
  Dunit = g/cm3
  Dvalue = 1.2
  Group = -> [H_element574,C_element618,O_element547]
  conduct = 2
  density = 1
  expand = 3
  formula = G4_CELLULOSE_BUTYRATE
  name = G4_CELLULOSE_BUTYRATE
  specific = 4
FEATURE [App::DocumentObjectGroupPython] H_element575  label="H_element : 0.257"  # scripted group (container) (typed FeaturePython)
  n = 0.029216
FEATURE [App::DocumentObjectGroupPython] C_element619  label="C_element : 0.986"  # scripted group (container) (typed FeaturePython)
  n = 0.271296
FEATURE [App::DocumentObjectGroupPython] N_element285  label="N_element : 0.836"  # scripted group (container) (typed FeaturePython)
  n = 0.121276
FEATURE [App::DocumentObjectGroupPython] O_element548  label="O_element : 0.978"  # scripted group (container) (typed FeaturePython)
  n = 0.578212
FEATURE [App::DocumentObjectGroupPython] G4_CELLULOSE_NITRATE  # scripted group (container) (typed FeaturePython)
  Dunit = g/cm3
  Dvalue = 1.49
  Group = -> [H_element575,C_element619,N_element285,O_element548]
  conduct = 2
  density = 1
  expand = 3
  formula = G4_CELLULOSE_NITRATE
  name = G4_CELLULOSE_NITRATE
  specific = 4
FEATURE [App::DocumentObjectGroupPython] H_element576  label="H_element : 0.258"  # scripted group (container) (typed FeaturePython)
  n = 0.107596
FEATURE [App::DocumentObjectGroupPython] N_element286  label="N_element : 0.837"  # scripted group (container) (typed FeaturePython)
  n = 0.0008
FEATURE [App::DocumentObjectGroupPython] O_element549  label="O_element : 0.979"  # scripted group (container) (typed FeaturePython)
  n = 0.874976
FEATURE [App::DocumentObjectGroupPython] S_element100  label="S_element : 0.070"  # scripted group (container) (typed FeaturePython)
  n = 0.014627
FEATURE [App::DocumentObjectGroupPython] Ce_element009  label="Ce_element : 0.005"  # scripted group (container) (typed FeaturePython)
  n = 0.002001
FEATURE [App::DocumentObjectGroupPython] G4_CERIC_SULFATE  # scripted group (container) (typed FeaturePython)
  Dunit = g/cm3
  Dvalue = 1.03
  Group = -> [H_element576,N_element286,O_element549,S_element100,Ce_element009]
  conduct = 2
  density = 1
  expand = 3
  formula = G4_CERIC_SULFATE
  name = G4_CERIC_SULFATE
  specific = 4
FEATURE [App::DocumentObjectGroupPython] Cs_element013  label="Cs_element : 012"  # scripted group (container) (typed FeaturePython)
  n = 1
  ref = Cs_element
FEATURE [App::DocumentObjectGroupPython] F_element082  label="F_element : 039"  # scripted group (container) (typed FeaturePython)
  n = 1
  ref = F_element
FEATURE [App::DocumentObjectGroupPython] G4_CESIUM_FLUORIDE  # scripted group (container) (typed FeaturePython)
  Dunit = g/cm3
  Dvalue = 4.115
  Group = -> [Cs_element013,F_element082]
  conduct = 2
  density = 1
  expand = 3
  formula = G4_CESIUM_FLUORIDE
  name = G4_CESIUM_FLUORIDE
  specific = 4
FEATURE [App::DocumentObjectGroupPython] Cs_element014  label="Cs_element : 013"  # scripted group (container) (typed FeaturePython)
  n = 1
  ref = Cs_element
FEATURE [App::DocumentObjectGroupPython] I_element041  label="I_element : 026"  # scripted group (container) (typed FeaturePython)
  n = 1
  ref = I_element
FEATURE [App::DocumentObjectGroupPython] G4_CESIUM_IODIDE  # scripted group (container) (typed FeaturePython)
  Dunit = g/cm3
  Dvalue = 4.51
  Group = -> [Cs_element014,I_element041]
  conduct = 2
  density = 1
  expand = 3
  formula = G4_CESIUM_IODIDE
  name = G4_CESIUM_IODIDE
  specific = 4
FEATURE [App::DocumentObjectGroupPython] C_element620  label="C_element : 404"  # scripted group (container) (typed FeaturePython)
  n = 6
  ref = C_element
FEATURE [App::DocumentObjectGroupPython] H_element577  label="H_element : 369"  # scripted group (container) (typed FeaturePython)
  n = 5
  ref = H_element
FEATURE [App::DocumentObjectGroupPython] Cl_element125  label="Cl_element : 062"  # scripted group (container) (typed FeaturePython)
  n = 1
  ref = Cl_element
FEATURE [App::DocumentObjectGroupPython] G4_CHLOROBENZENE  # scripted group (container) (typed FeaturePython)
  Dunit = g/cm3
  Dvalue = 1.1058
  Group = -> [C_element620,H_element577,Cl_element125]
  conduct = 2
  density = 1
  expand = 3
  formula = G4_CHLOROBENZENE
  name = G4_CHLOROBENZENE
  specific = 4
FEATURE [App::DocumentObjectGroupPython] C_element621  label="C_element : 405"  # scripted group (container) (typed FeaturePython)
  n = 1
  ref = C_element
FEATURE [App::DocumentObjectGroupPython] H_element578  label="H_element : 370"  # scripted group (container) (typed FeaturePython)
  n = 1
  ref = H_element
FEATURE [App::DocumentObjectGroupPython] Cl_element126  label="Cl_element : 063"  # scripted group (container) (typed FeaturePython)
  n = 3
  ref = Cl_element
FEATURE [App::DocumentObjectGroupPython] G4_CHLOROFORM  # scripted group (container) (typed FeaturePython)
  Dunit = g/cm3
  Dvalue = 1.4832
  Group = -> [C_element621,H_element578,Cl_element126]
  conduct = 2
  density = 1
  expand = 3
  formula = G4_CHLOROFORM
  name = G4_CHLOROFORM
  specific = 4
FEATURE [App::DocumentObjectGroupPython] H_element579  label="H_element : 0.259"  # scripted group (container) (typed FeaturePython)
  n = 0.01
FEATURE [App::DocumentObjectGroupPython] C_element622  label="C_element : 0.987"  # scripted group (container) (typed FeaturePython)
  n = 0.001
FEATURE [App::DocumentObjectGroupPython] O_element550  label="O_element : 0.980"  # scripted group (container) (typed FeaturePython)
  n = 0.529107
FEATURE [App::DocumentObjectGroupPython] Na_element085  label="Na_element : 0.146"  # scripted group (container) (typed FeaturePython)
  n = 0.016
FEATURE [App::DocumentObjectGroupPython] Mg_element047  label="Mg_element : 0.152"  # scripted group (container) (typed FeaturePython)
  n = 0.002
FEATURE [App::DocumentObjectGroupPython] Al_element018  label="Al_element : 0.039"  # scripted group (container) (typed FeaturePython)
  n = 0.033872
FEATURE [App::DocumentObjectGroupPython] Si_element030  label="Si_element : 0.391"  # scripted group (container) (typed FeaturePython)
  n = 0.337021
FEATURE [App::DocumentObjectGroupPython] K_element055  label="K_element : 0.046"  # scripted group (container) (typed FeaturePython)
  n = 0.013
FEATURE [App::DocumentObjectGroupPython] Ca_element066  label="Ca_element : 0.244"  # scripted group (container) (typed FeaturePython)
  n = 0.044
FEATURE [App::DocumentObjectGroupPython] Fe_element034  label="Fe_element : 0.022"  # scripted group (container) (typed FeaturePython)
  n = 0.014
FEATURE [App::DocumentObjectGroupPython] G4_CONCRETE  # scripted group (container) (typed FeaturePython)
  Dunit = g/cm3
  Dvalue = 2.3
  Group = -> [H_element579,C_element622,O_element550,Na_element085,Mg_element047,Al_element018,Si_element030,K_element055,Ca_element066,Fe_element034]
  conduct = 2
  density = 1
  expand = 3
  formula = G4_CONCRETE
  name = G4_CONCRETE
  specific = 4
FEATURE [App::DocumentObjectGroupPython] C_element623  label="C_element : 406"  # scripted group (container) (typed FeaturePython)
  n = 6
  ref = C_element
FEATURE [App::DocumentObjectGroupPython] H_element580  label="H_element : 371"  # scripted group (container) (typed FeaturePython)
  n = 12
  ref = H_element
FEATURE [App::DocumentObjectGroupPython] G4_CYCLOHEXANE  # scripted group (container) (typed FeaturePython)
  Dunit = g/cm3
  Dvalue = 0.779
  Group = -> [C_element623,H_element580]
  conduct = 2
  density = 1
  expand = 3
  formula = G4_CYCLOHEXANE
  name = G4_CYCLOHEXANE
  specific = 4
FEATURE [App::DocumentObjectGroupPython] C_element624  label="C_element : 407"  # scripted group (container) (typed FeaturePython)
  n = 6
  ref = C_element
FEATURE [App::DocumentObjectGroupPython] H_element581  label="H_element : 372"  # scripted group (container) (typed FeaturePython)
  n = 4
  ref = H_element
FEATURE [App::DocumentObjectGroupPython] Cl_element127  label="Cl_element : 064"  # scripted group (container) (typed FeaturePython)
  n = 2
  ref = Cl_element
FEATURE [App::DocumentObjectGroupPython] G4_1_2_DICHLOROBENZENE  label="G4_1.2-DICHLOROBENZENE"  # scripted group (container) (typed FeaturePython)
  Dunit = g/cm3
  Dvalue = 1.3048
  Group = -> [C_element624,H_element581,Cl_element127]
  conduct = 2
  density = 1
  expand = 3
  formula = G4_1.2-DICHLOROBENZENE
  name = G4_1.2-DICHLOROBENZENE
  specific = 4
FEATURE [App::DocumentObjectGroupPython] C_element625  label="C_element : 408"  # scripted group (container) (typed FeaturePython)
  n = 4
  ref = C_element
FEATURE [App::DocumentObjectGroupPython] H_element582  label="H_element : 373"  # scripted group (container) (typed FeaturePython)
  n = 8
  ref = H_element
FEATURE [App::DocumentObjectGroupPython] O_element551  label="O_element : 350"  # scripted group (container) (typed FeaturePython)
  n = 1
  ref = O_element
FEATURE [App::DocumentObjectGroupPython] Cl_element128  label="Cl_element : 065"  # scripted group (container) (typed FeaturePython)
  n = 2
  ref = Cl_element
FEATURE [App::DocumentObjectGroupPython] G4_DICHLORODIETHYL_ETHER  # scripted group (container) (typed FeaturePython)
  Dunit = g/cm3
  Dvalue = 1.2199
  Group = -> [C_element625,H_element582,O_element551,Cl_element128]
  conduct = 2
  density = 1
  expand = 3
  formula = G4_DICHLORODIETHYL_ETHER
  name = G4_DICHLORODIETHYL_ETHER
  specific = 4
FEATURE [App::DocumentObjectGroupPython] C_element626  label="C_element : 409"  # scripted group (container) (typed FeaturePython)
  n = 2
  ref = C_element
FEATURE [App::DocumentObjectGroupPython] H_element583  label="H_element : 374"  # scripted group (container) (typed FeaturePython)
  n = 4
  ref = H_element
FEATURE [App::DocumentObjectGroupPython] Cl_element129  label="Cl_element : 066"  # scripted group (container) (typed FeaturePython)
  n = 2
  ref = Cl_element
FEATURE [App::DocumentObjectGroupPython] G4_1_2_DICHLOROETHANE  label="G4_1.2-DICHLOROETHANE"  # scripted group (container) (typed FeaturePython)
  Dunit = g/cm3
  Dvalue = 1.2351
  Group = -> [C_element626,H_element583,Cl_element129]
  conduct = 2
  density = 1
  expand = 3
  formula = G4_1.2-DICHLOROETHANE
  name = G4_1.2-DICHLOROETHANE
  specific = 4
FEATURE [App::DocumentObjectGroupPython] C_element627  label="C_element : 410"  # scripted group (container) (typed FeaturePython)
  n = 4
  ref = C_element
FEATURE [App::DocumentObjectGroupPython] H_element584  label="H_element : 375"  # scripted group (container) (typed FeaturePython)
  n = 10
  ref = H_element
FEATURE [App::DocumentObjectGroupPython] O_element552  label="O_element : 351"  # scripted group (container) (typed FeaturePython)
  n = 1
  ref = O_element
FEATURE [App::DocumentObjectGroupPython] G4_DIETHYL_ETHER  # scripted group (container) (typed FeaturePython)
  Dunit = g/cm3
  Dvalue = 0.71378
  Group = -> [C_element627,H_element584,O_element552]
  conduct = 2
  density = 1
  expand = 3
  formula = G4_DIETHYL_ETHER
  name = G4_DIETHYL_ETHER
  specific = 4
FEATURE [App::DocumentObjectGroupPython] C_element628  label="C_element : 411"  # scripted group (container) (typed FeaturePython)
  n = 3
  ref = C_element
FEATURE [App::DocumentObjectGroupPython] H_element585  label="H_element : 376"  # scripted group (container) (typed FeaturePython)
  n = 7
  ref = H_element
FEATURE [App::DocumentObjectGroupPython] N_element287  label="N_element : 158"  # scripted group (container) (typed FeaturePython)
  n = 1
  ref = N_element
FEATURE [App::DocumentObjectGroupPython] O_element553  label="O_element : 352"  # scripted group (container) (typed FeaturePython)
  n = 1
  ref = O_element
FEATURE [App::DocumentObjectGroupPython] G4_N_N_DIMETHYL_FORMAMIDE  label="G4_N.N-DIMETHYL_FORMAMIDE"  # scripted group (container) (typed FeaturePython)
  Dunit = g/cm3
  Dvalue = 0.9487
  Group = -> [C_element628,H_element585,N_element287,O_element553]
  conduct = 2
  density = 1
  expand = 3
  formula = G4_N.N-DIMETHYL_FORMAMIDE
  name = G4_N.N-DIMETHYL_FORMAMIDE
  specific = 4
FEATURE [App::DocumentObjectGroupPython] C_element629  label="C_element : 412"  # scripted group (container) (typed FeaturePython)
  n = 2
  ref = C_element
FEATURE [App::DocumentObjectGroupPython] H_element586  label="H_element : 377"  # scripted group (container) (typed FeaturePython)
  n = 6
  ref = H_element
FEATURE [App::DocumentObjectGroupPython] O_element554  label="O_element : 353"  # scripted group (container) (typed FeaturePython)
  n = 1
  ref = O_element
FEATURE [App::DocumentObjectGroupPython] S_element101  label="S_element : 030"  # scripted group (container) (typed FeaturePython)
  n = 1
  ref = S_element
FEATURE [App::DocumentObjectGroupPython] G4_DIMETHYL_SULFOXIDE  # scripted group (container) (typed FeaturePython)
  Dunit = g/cm3
  Dvalue = 1.1014
  Group = -> [C_element629,H_element586,O_element554,S_element101]
  conduct = 2
  density = 1
  expand = 3
  formula = G4_DIMETHYL_SULFOXIDE
  name = G4_DIMETHYL_SULFOXIDE
  specific = 4
FEATURE [App::DocumentObjectGroupPython] C_element630  label="C_element : 413"  # scripted group (container) (typed FeaturePython)
  n = 2
  ref = C_element
FEATURE [App::DocumentObjectGroupPython] H_element587  label="H_element : 378"  # scripted group (container) (typed FeaturePython)
  n = 6
  ref = H_element
FEATURE [App::DocumentObjectGroupPython] G4_ETHANE  # scripted group (container) (typed FeaturePython)
  Dunit = g/cm3
  Dvalue = 0.00125324
  Group = -> [C_element630,H_element587]
  conduct = 2
  density = 1
  expand = 3
  formula = G4_ETHANE
  name = G4_ETHANE
  specific = 4
FEATURE [App::DocumentObjectGroupPython] C_element631  label="C_element : 414"  # scripted group (container) (typed FeaturePython)
  n = 2
  ref = C_element
FEATURE [App::DocumentObjectGroupPython] H_element588  label="H_element : 379"  # scripted group (container) (typed FeaturePython)
  n = 6
  ref = H_element
FEATURE [App::DocumentObjectGroupPython] O_element555  label="O_element : 354"  # scripted group (container) (typed FeaturePython)
  n = 1
  ref = O_element
FEATURE [App::DocumentObjectGroupPython] G4_ETHYL_ALCOHOL  # scripted group (container) (typed FeaturePython)
  Dunit = g/cm3
  Dvalue = 0.7893
  Group = -> [C_element631,H_element588,O_element555]
  conduct = 2
  density = 1
  expand = 3
  formula = G4_ETHYL_ALCOHOL
  name = G4_ETHYL_ALCOHOL
  specific = 4
FEATURE [App::DocumentObjectGroupPython] H_element589  label="H_element : 0.260"  # scripted group (container) (typed FeaturePython)
  n = 0.090027
FEATURE [App::DocumentObjectGroupPython] C_element632  label="C_element : 0.988"  # scripted group (container) (typed FeaturePython)
  n = 0.585182
FEATURE [App::DocumentObjectGroupPython] O_element556  label="O_element : 0.981"  # scripted group (container) (typed FeaturePython)
  n = 0.324791
FEATURE [App::DocumentObjectGroupPython] G4_ETHYL_CELLULOSE  # scripted group (container) (typed FeaturePython)
  Dunit = g/cm3
  Dvalue = 1.13
  Group = -> [H_element589,C_element632,O_element556]
  conduct = 2
  density = 1
  expand = 3
  formula = G4_ETHYL_CELLULOSE
  name = G4_ETHYL_CELLULOSE
  specific = 4
FEATURE [App::DocumentObjectGroupPython] C_element633  label="C_element : 415"  # scripted group (container) (typed FeaturePython)
  n = 2
  ref = C_element
FEATURE [App::DocumentObjectGroupPython] H_element590  label="H_element : 380"  # scripted group (container) (typed FeaturePython)
  n = 4
  ref = H_element
FEATURE [App::DocumentObjectGroupPython] G4_ETHYLENE  # scripted group (container) (typed FeaturePython)
  Dunit = g/cm3
  Dvalue = 0.00117497
  Group = -> [C_element633,H_element590]
  conduct = 2
  density = 1
  expand = 3
  formula = G4_ETHYLENE
  name = G4_ETHYLENE
  specific = 4
FEATURE [App::DocumentObjectGroupPython] H_element591  label="H_element : 0.261"  # scripted group (container) (typed FeaturePython)
  n = 0.096
FEATURE [App::DocumentObjectGroupPython] C_element634  label="C_element : 0.989"  # scripted group (container) (typed FeaturePython)
  n = 0.195
FEATURE [App::DocumentObjectGroupPython] N_element288  label="N_element : 0.838"  # scripted group (container) (typed FeaturePython)
  n = 0.057
FEATURE [App::DocumentObjectGroupPython] O_element557  label="O_element : 0.982"  # scripted group (container) (typed FeaturePython)
  n = 0.646
FEATURE [App::DocumentObjectGroupPython] Na_element086  label="Na_element : 0.147"  # scripted group (container) (typed FeaturePython)
  n = 0.001
FEATURE [App::DocumentObjectGroupPython] P_element081  label="P_element : 0.142"  # scripted group (container) (typed FeaturePython)
  n = 0.001
FEATURE [App::DocumentObjectGroupPython] S_element102  label="S_element : 0.071"  # scripted group (container) (typed FeaturePython)
  n = 0.003
FEATURE [App::DocumentObjectGroupPython] Cl_element130  label="Cl_element : 0.630"  # scripted group (container) (typed FeaturePython)
  n = 0.001
FEATURE [App::DocumentObjectGroupPython] G4_EYE_LENS_ICRP  # scripted group (container) (typed FeaturePython)
  Dunit = g/cm3
  Dvalue = 1.07
  Group = -> [H_element591,C_element634,N_element288,O_element557,Na_element086,P_element081,S_element102,Cl_element130]
  conduct = 2
  density = 1
  expand = 3
  formula = G4_EYE_LENS_ICRP
  name = G4_EYE_LENS_ICRP
  specific = 4
FEATURE [App::DocumentObjectGroupPython] Fe_element035  label="Fe_element : 017"  # scripted group (container) (typed FeaturePython)
  n = 2
  ref = Fe_element
FEATURE [App::DocumentObjectGroupPython] O_element558  label="O_element : 355"  # scripted group (container) (typed FeaturePython)
  n = 3
  ref = O_element
FEATURE [App::DocumentObjectGroupPython] G4_FERRIC_OXIDE  # scripted group (container) (typed FeaturePython)
  Dunit = g/cm3
  Dvalue = 5.2
  Group = -> [Fe_element035,O_element558]
  conduct = 2
  density = 1
  expand = 3
  formula = G4_FERRIC_OXIDE
  name = G4_FERRIC_OXIDE
  specific = 4
FEATURE [App::DocumentObjectGroupPython] Fe_element036  label="Fe_element : 018"  # scripted group (container) (typed FeaturePython)
  n = 1
  ref = Fe_element
FEATURE [App::DocumentObjectGroupPython] B_element031  label="B_element : 025"  # scripted group (container) (typed FeaturePython)
  n = 1
  ref = B_element
FEATURE [App::DocumentObjectGroupPython] G4_FERROBORIDE  # scripted group (container) (typed FeaturePython)
  Dunit = g/cm3
  Dvalue = 7.15
  Group = -> [Fe_element036,B_element031]
  conduct = 2
  density = 1
  expand = 3
  formula = G4_FERROBORIDE
  name = G4_FERROBORIDE
  specific = 4
FEATURE [App::DocumentObjectGroupPython] Fe_element037  label="Fe_element : 019"  # scripted group (container) (typed FeaturePython)
  n = 1
  ref = Fe_element
FEATURE [App::DocumentObjectGroupPython] O_element559  label="O_element : 356"  # scripted group (container) (typed FeaturePython)
  n = 1
  ref = O_element
FEATURE [App::DocumentObjectGroupPython] G4_FERROUS_OXIDE  # scripted group (container) (typed FeaturePython)
  Dunit = g/cm3
  Dvalue = 5.7
  Group = -> [Fe_element037,O_element559]
  conduct = 2
  density = 1
  expand = 3
  formula = G4_FERROUS_OXIDE
  name = G4_FERROUS_OXIDE
  specific = 4
FEATURE [App::DocumentObjectGroupPython] H_element592  label="H_element : 0.262"  # scripted group (container) (typed FeaturePython)
  n = 0.108259
FEATURE [App::DocumentObjectGroupPython] N_element289  label="N_element : 0.839"  # scripted group (container) (typed FeaturePython)
  n = 2.7e-05
FEATURE [App::DocumentObjectGroupPython] O_element560  label="O_element : 0.983"  # scripted group (container) (typed FeaturePython)
  n = 0.878636
FEATURE [App::DocumentObjectGroupPython] Na_element087  label="Na_element : 0.148"  # scripted group (container) (typed FeaturePython)
  n = 2.2e-05
FEATURE [App::DocumentObjectGroupPython] S_element103  label="S_element : 0.072"  # scripted group (container) (typed FeaturePython)
  n = 0.012968
FEATURE [App::DocumentObjectGroupPython] Cl_element131  label="Cl_element : 0.631"  # scripted group (container) (typed FeaturePython)
  n = 3.4e-05
FEATURE [App::DocumentObjectGroupPython] Fe_element038  label="Fe_element : 0.023"  # scripted group (container) (typed FeaturePython)
  n = 5.4e-05
FEATURE [App::DocumentObjectGroupPython] G4_FERROUS_SULFATE  # scripted group (container) (typed FeaturePython)
  Dunit = g/cm3
  Dvalue = 1.024
  Group = -> [H_element592,N_element289,O_element560,Na_element087,S_element103,Cl_element131,Fe_element038]
  conduct = 2
  density = 1
  expand = 3
  formula = G4_FERROUS_SULFATE
  name = G4_FERROUS_SULFATE
  specific = 4
FEATURE [App::DocumentObjectGroupPython] C_element635  label="C_element : 0.990"  # scripted group (container) (typed FeaturePython)
  n = 0.099335
FEATURE [App::DocumentObjectGroupPython] F_element083  label="F_element : 0.730"  # scripted group (container) (typed FeaturePython)
  n = 0.314247
FEATURE [App::DocumentObjectGroupPython] Cl_element132  label="Cl_element : 0.632"  # scripted group (container) (typed FeaturePython)
  n = 0.586418
FEATURE [App::DocumentObjectGroupPython] G4_FREON_12  label="G4_FREON-12"  # scripted group (container) (typed FeaturePython)
  Dunit = g/cm3
  Dvalue = 1.12
  Group = -> [C_element635,F_element083,Cl_element132]
  conduct = 2
  density = 1
  expand = 3
  formula = G4_FREON-12
  name = G4_FREON-12
  specific = 4
FEATURE [App::DocumentObjectGroupPython] C_element636  label="C_element : 0.991"  # scripted group (container) (typed FeaturePython)
  n = 0.057245
FEATURE [App::DocumentObjectGroupPython] F_element084  label="F_element : 0.731"  # scripted group (container) (typed FeaturePython)
  n = 0.181096
FEATURE [App::DocumentObjectGroupPython] Br_element029  label="Br_element : 0.769"  # scripted group (container) (typed FeaturePython)
  n = 0.761659
FEATURE [App::DocumentObjectGroupPython] G4_FREON_12B2  label="G4_FREON-12B2"  # scripted group (container) (typed FeaturePython)
  Dunit = g/cm3
  Dvalue = 1.8
  Group = -> [C_element636,F_element084,Br_element029]
  conduct = 2
  density = 1
  expand = 3
  formula = G4_FREON-12B2
  name = G4_FREON-12B2
  specific = 4
FEATURE [App::DocumentObjectGroupPython] C_element637  label="C_element : 0.992"  # scripted group (container) (typed FeaturePython)
  n = 0.114983
FEATURE [App::DocumentObjectGroupPython] F_element085  label="F_element : 0.732"  # scripted group (container) (typed FeaturePython)
  n = 0.545621
FEATURE [App::DocumentObjectGroupPython] Cl_element133  label="Cl_element : 0.633"  # scripted group (container) (typed FeaturePython)
  n = 0.339396
FEATURE [App::DocumentObjectGroupPython] G4_FREON_13  label="G4_FREON-13"  # scripted group (container) (typed FeaturePython)
  Dunit = g/cm3
  Dvalue = 0.95
  Group = -> [C_element637,F_element085,Cl_element133]
  conduct = 2
  density = 1
  expand = 3
  formula = G4_FREON-13
  name = G4_FREON-13
  specific = 4
FEATURE [App::DocumentObjectGroupPython] C_element638  label="C_element : 416"  # scripted group (container) (typed FeaturePython)
  n = 1
  ref = C_element
FEATURE [App::DocumentObjectGroupPython] F_element086  label="F_element : 040"  # scripted group (container) (typed FeaturePython)
  n = 3
  ref = F_element
FEATURE [App::DocumentObjectGroupPython] Br_element030  label="Br_element : 016"  # scripted group (container) (typed FeaturePython)
  n = 1
  ref = Br_element
FEATURE [App::DocumentObjectGroupPython] G4_FREON_13B1  label="G4_FREON-13B1"  # scripted group (container) (typed FeaturePython)
  Dunit = g/cm3
  Dvalue = 1.5
  Group = -> [C_element638,F_element086,Br_element030]
  conduct = 2
  density = 1
  expand = 3
  formula = G4_FREON-13B1
  name = G4_FREON-13B1
  specific = 4
FEATURE [App::DocumentObjectGroupPython] C_element639  label="C_element : 0.993"  # scripted group (container) (typed FeaturePython)
  n = 0.061309
FEATURE [App::DocumentObjectGroupPython] F_element087  label="F_element : 0.733"  # scripted group (container) (typed FeaturePython)
  n = 0.290924
FEATURE [App::DocumentObjectGroupPython] I_element042  label="I_element : 0.657"  # scripted group (container) (typed FeaturePython)
  n = 0.647767
FEATURE [App::DocumentObjectGroupPython] G4_FREON_13I1  label="G4_FREON-13I1"  # scripted group (container) (typed FeaturePython)
  Dunit = g/cm3
  Dvalue = 1.8
  Group = -> [C_element639,F_element087,I_element042]
  conduct = 2
  density = 1
  expand = 3
  formula = G4_FREON-13I1
  name = G4_FREON-13I1
  specific = 4
FEATURE [App::DocumentObjectGroupPython] Gd_element009  label="Gd_element : 007"  # scripted group (container) (typed FeaturePython)
  n = 2
  ref = Gd_element
FEATURE [App::DocumentObjectGroupPython] O_element561  label="O_element : 357"  # scripted group (container) (typed FeaturePython)
  n = 2
  ref = O_element
FEATURE [App::DocumentObjectGroupPython] S_element104  label="S_element : 031"  # scripted group (container) (typed FeaturePython)
  n = 1
  ref = S_element
FEATURE [App::DocumentObjectGroupPython] G4_GADOLINIUM_OXYSULFIDE  # scripted group (container) (typed FeaturePython)
  Dunit = g/cm3
  Dvalue = 7.44
  Group = -> [Gd_element009,O_element561,S_element104]
  conduct = 2
  density = 1
  expand = 3
  formula = G4_GADOLINIUM_OXYSULFIDE
  name = G4_GADOLINIUM_OXYSULFIDE
  specific = 4
FEATURE [App::DocumentObjectGroupPython] Ga_element009  label="Ga_element : 008"  # scripted group (container) (typed FeaturePython)
  n = 1
  ref = Ga_element
FEATURE [App::DocumentObjectGroupPython] As_element013  label="As_element : 008"  # scripted group (container) (typed FeaturePython)
  n = 1
  ref = As_element
FEATURE [App::DocumentObjectGroupPython] G4_GALLIUM_ARSENIDE  # scripted group (container) (typed FeaturePython)
  Dunit = g/cm3
  Dvalue = 5.31
  Group = -> [Ga_element009,As_element013]
  conduct = 2
  density = 1
  expand = 3
  formula = G4_GALLIUM_ARSENIDE
  name = G4_GALLIUM_ARSENIDE
  specific = 4
FEATURE [App::DocumentObjectGroupPython] H_element593  label="H_element : 0.263"  # scripted group (container) (typed FeaturePython)
  n = 0.08118
FEATURE [App::DocumentObjectGroupPython] C_element640  label="C_element : 0.994"  # scripted group (container) (typed FeaturePython)
  n = 0.41606
FEATURE [App::DocumentObjectGroupPython] N_element290  label="N_element : 0.840"  # scripted group (container) (typed FeaturePython)
  n = 0.11124
FEATURE [App::DocumentObjectGroupPython] O_element562  label="O_element : 0.984"  # scripted group (container) (typed FeaturePython)
  n = 0.38064
FEATURE [App::DocumentObjectGroupPython] S_element105  label="S_element : 0.073"  # scripted group (container) (typed FeaturePython)
  n = 0.01088
FEATURE [App::DocumentObjectGroupPython] G4_GEL_PHOTO_EMULSION  # scripted group (container) (typed FeaturePython)
  Dunit = g/cm3
  Dvalue = 1.2914
  Group = -> [H_element593,C_element640,N_element290,O_element562,S_element105]
  conduct = 2
  density = 1
  expand = 3
  formula = G4_GEL_PHOTO_EMULSION
  name = G4_GEL_PHOTO_EMULSION
  specific = 4
FEATURE [App::DocumentObjectGroupPython] B_element032  label="B_element : 0.043"  # scripted group (container) (typed FeaturePython)
  n = 0.0400639
FEATURE [App::DocumentObjectGroupPython] O_element563  label="O_element : 0.985"  # scripted group (container) (typed FeaturePython)
  n = 0.539561
FEATURE [App::DocumentObjectGroupPython] Na_element088  label="Na_element : 0.149"  # scripted group (container) (typed FeaturePython)
  n = 0.0281909
FEATURE [App::DocumentObjectGroupPython] Al_element019  label="Al_element : 0.040"  # scripted group (container) (typed FeaturePython)
  n = 0.011644
FEATURE [App::DocumentObjectGroupPython] Si_element031  label="Si_element : 0.392"  # scripted group (container) (typed FeaturePython)
  n = 0.377219
FEATURE [App::DocumentObjectGroupPython] K_element056  label="K_element : 0.047"  # scripted group (container) (typed FeaturePython)
  n = 0.00332099
FEATURE [App::DocumentObjectGroupPython] G4_Pyrex_Glass  # scripted group (container) (typed FeaturePython)
  Dunit = g/cm3
  Dvalue = 2.23
  Group = -> [B_element032,O_element563,Na_element088,Al_element019,Si_element031,K_element056]
  conduct = 2
  density = 1
  expand = 3
  formula = G4_Pyrex_Glass
  name = G4_Pyrex_Glass
  specific = 4
FEATURE [App::DocumentObjectGroupPython] O_element564  label="O_element : 0.986"  # scripted group (container) (typed FeaturePython)
  n = 0.156453
FEATURE [App::DocumentObjectGroupPython] Si_element032  label="Si_element : 0.393"  # scripted group (container) (typed FeaturePython)
  n = 0.080866
FEATURE [App::DocumentObjectGroupPython] Ti_element017  label="Ti_element : 0.019"  # scripted group (container) (typed FeaturePython)
  n = 0.008092
FEATURE [App::DocumentObjectGroupPython] As_element014  label="As_element : 0.006"  # scripted group (container) (typed FeaturePython)
  n = 0.002651
FEATURE [App::DocumentObjectGroupPython] Pb_element025  label="Pb_element : 0.933"  # scripted group (container) (typed FeaturePython)
  n = 0.751938
FEATURE [App::DocumentObjectGroupPython] G4_GLASS_LEAD  # scripted group (container) (typed FeaturePython)
  Dunit = g/cm3
  Dvalue = 6.22
  Group = -> [O_element564,Si_element032,Ti_element017,As_element014,Pb_element025]
  conduct = 2
  density = 1
  expand = 3
  formula = G4_GLASS_LEAD
  name = G4_GLASS_LEAD
  specific = 4
FEATURE [App::DocumentObjectGroupPython] O_element565  label="O_element : 0.987"  # scripted group (container) (typed FeaturePython)
  n = 0.4598
FEATURE [App::DocumentObjectGroupPython] Na_element089  label="Na_element : 0.150"  # scripted group (container) (typed FeaturePython)
  n = 0.0964411
FEATURE [App::DocumentObjectGroupPython] Si_element033  label="Si_element : 0.394"  # scripted group (container) (typed FeaturePython)
  n = 0.336553
FEATURE [App::DocumentObjectGroupPython] Ca_element067  label="Ca_element : 0.245"  # scripted group (container) (typed FeaturePython)
  n = 0.107205
FEATURE [App::DocumentObjectGroupPython] G4_GLASS_PLATE  # scripted group (container) (typed FeaturePython)
  Dunit = g/cm3
  Dvalue = 2.4
  Group = -> [O_element565,Na_element089,Si_element033,Ca_element067]
  conduct = 2
  density = 1
  expand = 3
  formula = G4_GLASS_PLATE
  name = G4_GLASS_PLATE
  specific = 4
FEATURE [App::DocumentObjectGroupPython] C_element641  label="C_element : 417"  # scripted group (container) (typed FeaturePython)
  n = 5
  ref = C_element
FEATURE [App::DocumentObjectGroupPython] H_element594  label="H_element : 381"  # scripted group (container) (typed FeaturePython)
  n = 10
  ref = H_element
FEATURE [App::DocumentObjectGroupPython] N_element291  label="N_element : 159"  # scripted group (container) (typed FeaturePython)
  n = 2
  ref = N_element
FEATURE [App::DocumentObjectGroupPython] O_element566  label="O_element : 358"  # scripted group (container) (typed FeaturePython)
  n = 3
  ref = O_element
FEATURE [App::DocumentObjectGroupPython] G4_GLUTAMINE  # scripted group (container) (typed FeaturePython)
  Dunit = g/cm3
  Dvalue = 1.46
  Group = -> [C_element641,H_element594,N_element291,O_element566]
  conduct = 2
  density = 1
  expand = 3
  formula = G4_GLUTAMINE
  name = G4_GLUTAMINE
  specific = 4
FEATURE [App::DocumentObjectGroupPython] C_element642  label="C_element : 418"  # scripted group (container) (typed FeaturePython)
  n = 3
  ref = C_element
FEATURE [App::DocumentObjectGroupPython] H_element595  label="H_element : 382"  # scripted group (container) (typed FeaturePython)
  n = 8
  ref = H_element
FEATURE [App::DocumentObjectGroupPython] O_element567  label="O_element : 359"  # scripted group (container) (typed FeaturePython)
  n = 3
  ref = O_element
FEATURE [App::DocumentObjectGroupPython] G4_GLYCEROL  # scripted group (container) (typed FeaturePython)
  Dunit = g/cm3
  Dvalue = 1.2613
  Group = -> [C_element642,H_element595,O_element567]
  conduct = 2
  density = 1
  expand = 3
  formula = G4_GLYCEROL
  name = G4_GLYCEROL
  specific = 4
FEATURE [App::DocumentObjectGroupPython] C_element643  label="C_element : 419"  # scripted group (container) (typed FeaturePython)
  n = 5
  ref = C_element
FEATURE [App::DocumentObjectGroupPython] H_element596  label="H_element : 383"  # scripted group (container) (typed FeaturePython)
  n = 5
  ref = H_element
FEATURE [App::DocumentObjectGroupPython] N_element292  label="N_element : 160"  # scripted group (container) (typed FeaturePython)
  n = 5
  ref = N_element
FEATURE [App::DocumentObjectGroupPython] O_element568  label="O_element : 360"  # scripted group (container) (typed FeaturePython)
  n = 1
  ref = O_element
FEATURE [App::DocumentObjectGroupPython] G4_GUANINE  # scripted group (container) (typed FeaturePython)
  Dunit = g/cm3
  Dvalue = 2.2
  Group = -> [C_element643,H_element596,N_element292,O_element568]
  conduct = 2
  density = 1
  expand = 3
  formula = G4_GUANINE
  name = G4_GUANINE
  specific = 4
FEATURE [App::DocumentObjectGroupPython] Ca_element068  label="Ca_element : 033"  # scripted group (container) (typed FeaturePython)
  n = 1
  ref = Ca_element
FEATURE [App::DocumentObjectGroupPython] S_element106  label="S_element : 032"  # scripted group (container) (typed FeaturePython)
  n = 1
  ref = S_element
FEATURE [App::DocumentObjectGroupPython] O_element569  label="O_element : 361"  # scripted group (container) (typed FeaturePython)
  n = 6
  ref = O_element
FEATURE [App::DocumentObjectGroupPython] H_element597  label="H_element : 384"  # scripted group (container) (typed FeaturePython)
  n = 4
  ref = H_element
FEATURE [App::DocumentObjectGroupPython] G4_GYPSUM  # scripted group (container) (typed FeaturePython)
  Dunit = g/cm3
  Dvalue = 2.32
  Group = -> [Ca_element068,S_element106,O_element569,H_element597]
  conduct = 2
  density = 1
  expand = 3
  formula = G4_GYPSUM
  name = G4_GYPSUM
  specific = 4
FEATURE [App::DocumentObjectGroupPython] C_element644  label="C_element : 420"  # scripted group (container) (typed FeaturePython)
  n = 7
  ref = C_element
FEATURE [App::DocumentObjectGroupPython] H_element598  label="H_element : 385"  # scripted group (container) (typed FeaturePython)
  n = 16
  ref = H_element
FEATURE [App::DocumentObjectGroupPython] G4_N_HEPTANE  label="G4_N-HEPTANE"  # scripted group (container) (typed FeaturePython)
  Dunit = g/cm3
  Dvalue = 0.68376
  Group = -> [C_element644,H_element598]
  conduct = 2
  density = 1
  expand = 3
  formula = G4_N-HEPTANE
  name = G4_N-HEPTANE
  specific = 4
FEATURE [App::DocumentObjectGroupPython] C_element645  label="C_element : 421"  # scripted group (container) (typed FeaturePython)
  n = 6
  ref = C_element
FEATURE [App::DocumentObjectGroupPython] H_element599  label="H_element : 386"  # scripted group (container) (typed FeaturePython)
  n = 14
  ref = H_element
FEATURE [App::DocumentObjectGroupPython] G4_N_HEXANE  label="G4_N-HEXANE"  # scripted group (container) (typed FeaturePython)
  Dunit = g/cm3
  Dvalue = 0.6603
  Group = -> [C_element645,H_element599]
  conduct = 2
  density = 1
  expand = 3
  formula = G4_N-HEXANE
  name = G4_N-HEXANE
  specific = 4
FEATURE [App::DocumentObjectGroupPython] C_element646  label="C_element : 422"  # scripted group (container) (typed FeaturePython)
  n = 22
  ref = C_element
FEATURE [App::DocumentObjectGroupPython] H_element600  label="H_element : 387"  # scripted group (container) (typed FeaturePython)
  n = 10
  ref = H_element
FEATURE [App::DocumentObjectGroupPython] N_element293  label="N_element : 161"  # scripted group (container) (typed FeaturePython)
  n = 2
  ref = N_element
FEATURE [App::DocumentObjectGroupPython] O_element570  label="O_element : 362"  # scripted group (container) (typed FeaturePython)
  n = 5
  ref = O_element
FEATURE [App::DocumentObjectGroupPython] G4_KAPTON  # scripted group (container) (typed FeaturePython)
  Dunit = g/cm3
  Dvalue = 1.42
  Group = -> [C_element646,H_element600,N_element293,O_element570]
  conduct = 2
  density = 1
  expand = 3
  formula = G4_KAPTON
  name = G4_KAPTON
  specific = 4
FEATURE [App::DocumentObjectGroupPython] La_element013  label="La_element : 011"  # scripted group (container) (typed FeaturePython)
  n = 1
  ref = La_element
FEATURE [App::DocumentObjectGroupPython] Br_element031  label="Br_element : 017"  # scripted group (container) (typed FeaturePython)
  n = 1
  ref = Br_element
FEATURE [App::DocumentObjectGroupPython] O_element571  label="O_element : 363"  # scripted group (container) (typed FeaturePython)
  n = 1
  ref = O_element
FEATURE [App::DocumentObjectGroupPython] G4_LANTHANUM_OXYBROMIDE  # scripted group (container) (typed FeaturePython)
  Dunit = g/cm3
  Dvalue = 6.28
  Group = -> [La_element013,Br_element031,O_element571]
  conduct = 2
  density = 1
  expand = 3
  formula = G4_LANTHANUM_OXYBROMIDE
  name = G4_LANTHANUM_OXYBROMIDE
  specific = 4
FEATURE [App::DocumentObjectGroupPython] La_element014  label="La_element : 012"  # scripted group (container) (typed FeaturePython)
  n = 2
  ref = La_element
FEATURE [App::DocumentObjectGroupPython] O_element572  label="O_element : 364"  # scripted group (container) (typed FeaturePython)
  n = 2
  ref = O_element
FEATURE [App::DocumentObjectGroupPython] S_element107  label="S_element : 033"  # scripted group (container) (typed FeaturePython)
  n = 1
  ref = S_element
FEATURE [App::DocumentObjectGroupPython] G4_LANTHANUM_OXYSULFIDE  # scripted group (container) (typed FeaturePython)
  Dunit = g/cm3
  Dvalue = 5.86
  Group = -> [La_element014,O_element572,S_element107]
  conduct = 2
  density = 1
  expand = 3
  formula = G4_LANTHANUM_OXYSULFIDE
  name = G4_LANTHANUM_OXYSULFIDE
  specific = 4
FEATURE [App::DocumentObjectGroupPython] O_element573  label="O_element : 0.988"  # scripted group (container) (typed FeaturePython)
  n = 0.071682
FEATURE [App::DocumentObjectGroupPython] Pb_element026  label="Pb_element : 0.934"  # scripted group (container) (typed FeaturePython)
  n = 0.928318
FEATURE [App::DocumentObjectGroupPython] G4_LEAD_OXIDE  # scripted group (container) (typed FeaturePython)
  Dunit = g/cm3
  Dvalue = 9.53
  Group = -> [O_element573,Pb_element026]
  conduct = 2
  density = 1
  expand = 3
  formula = G4_LEAD_OXIDE
  name = G4_LEAD_OXIDE
  specific = 4
FEATURE [App::DocumentObjectGroupPython] Li_element033  label="Li_element : 031"  # scripted group (container) (typed FeaturePython)
  n = 1
  ref = Li_element
FEATURE [App::DocumentObjectGroupPython] N_element294  label="N_element : 162"  # scripted group (container) (typed FeaturePython)
  n = 1
  ref = N_element
FEATURE [App::DocumentObjectGroupPython] H_element601  label="H_element : 388"  # scripted group (container) (typed FeaturePython)
  n = 2
  ref = H_element
FEATURE [App::DocumentObjectGroupPython] G4_LITHIUM_AMIDE  # scripted group (container) (typed FeaturePython)
  Dunit = g/cm3
  Dvalue = 1.178
  Group = -> [Li_element033,N_element294,H_element601]
  conduct = 2
  density = 1
  expand = 3
  formula = G4_LITHIUM_AMIDE
  name = G4_LITHIUM_AMIDE
  specific = 4
FEATURE [App::DocumentObjectGroupPython] Li_element034  label="Li_element : 032"  # scripted group (container) (typed FeaturePython)
  n = 2
  ref = Li_element
FEATURE [App::DocumentObjectGroupPython] C_element647  label="C_element : 423"  # scripted group (container) (typed FeaturePython)
  n = 1
  ref = C_element
FEATURE [App::DocumentObjectGroupPython] O_element574  label="O_element : 365"  # scripted group (container) (typed FeaturePython)
  n = 3
  ref = O_element
FEATURE [App::DocumentObjectGroupPython] G4_LITHIUM_CARBONATE  # scripted group (container) (typed FeaturePython)
  Dunit = g/cm3
  Dvalue = 2.11
  Group = -> [Li_element034,C_element647,O_element574]
  conduct = 2
  density = 1
  expand = 3
  formula = G4_LITHIUM_CARBONATE
  name = G4_LITHIUM_CARBONATE
  specific = 4
FEATURE [App::DocumentObjectGroupPython] Li_element035  label="Li_element : 033"  # scripted group (container) (typed FeaturePython)
  n = 1
  ref = Li_element
FEATURE [App::DocumentObjectGroupPython] F_element088  label="F_element : 041"  # scripted group (container) (typed FeaturePython)
  n = 1
  ref = F_element
FEATURE [App::DocumentObjectGroupPython] G4_LITHIUM_FLUORIDE  # scripted group (container) (typed FeaturePython)
  Dunit = g/cm3
  Dvalue = 2.635
  Group = -> [Li_element035,F_element088]
  conduct = 2
  density = 1
  expand = 3
  formula = G4_LITHIUM_FLUORIDE
  name = G4_LITHIUM_FLUORIDE
  specific = 4
FEATURE [App::DocumentObjectGroupPython] Li_element036  label="Li_element : 034"  # scripted group (container) (typed FeaturePython)
  n = 1
  ref = Li_element
FEATURE [App::DocumentObjectGroupPython] H_element602  label="H_element : 389"  # scripted group (container) (typed FeaturePython)
  n = 1
  ref = H_element
FEATURE [App::DocumentObjectGroupPython] G4_LITHIUM_HYDRIDE  # scripted group (container) (typed FeaturePython)
  Dunit = g/cm3
  Dvalue = 0.82
  Group = -> [Li_element036,H_element602]
  conduct = 2
  density = 1
  expand = 3
  formula = G4_LITHIUM_HYDRIDE
  name = G4_LITHIUM_HYDRIDE
  specific = 4
FEATURE [App::DocumentObjectGroupPython] Li_element037  label="Li_element : 035"  # scripted group (container) (typed FeaturePython)
  n = 1
  ref = Li_element
FEATURE [App::DocumentObjectGroupPython] I_element043  label="I_element : 027"  # scripted group (container) (typed FeaturePython)
  n = 1
  ref = I_element
FEATURE [App::DocumentObjectGroupPython] G4_LITHIUM_IODIDE  # scripted group (container) (typed FeaturePython)
  Dunit = g/cm3
  Dvalue = 3.494
  Group = -> [Li_element037,I_element043]
  conduct = 2
  density = 1
  expand = 3
  formula = G4_LITHIUM_IODIDE
  name = G4_LITHIUM_IODIDE
  specific = 4
FEATURE [App::DocumentObjectGroupPython] Li_element038  label="Li_element : 036"  # scripted group (container) (typed FeaturePython)
  n = 2
  ref = Li_element
FEATURE [App::DocumentObjectGroupPython] O_element575  label="O_element : 366"  # scripted group (container) (typed FeaturePython)
  n = 1
  ref = O_element
FEATURE [App::DocumentObjectGroupPython] G4_LITHIUM_OXIDE  # scripted group (container) (typed FeaturePython)
  Dunit = g/cm3
  Dvalue = 2.013
  Group = -> [Li_element038,O_element575]
  conduct = 2
  density = 1
  expand = 3
  formula = G4_LITHIUM_OXIDE
  name = G4_LITHIUM_OXIDE
  specific = 4
FEATURE [App::DocumentObjectGroupPython] Li_element039  label="Li_element : 037"  # scripted group (container) (typed FeaturePython)
  n = 2
  ref = Li_element
FEATURE [App::DocumentObjectGroupPython] B_element033  label="B_element : 026"  # scripted group (container) (typed FeaturePython)
  n = 4
  ref = B_element
FEATURE [App::DocumentObjectGroupPython] O_element576  label="O_element : 367"  # scripted group (container) (typed FeaturePython)
  n = 7
  ref = O_element
FEATURE [App::DocumentObjectGroupPython] G4_LITHIUM_TETRABORATE  # scripted group (container) (typed FeaturePython)
  Dunit = g/cm3
  Dvalue = 2.44
  Group = -> [Li_element039,B_element033,O_element576]
  conduct = 2
  density = 1
  expand = 3
  formula = G4_LITHIUM_TETRABORATE
  name = G4_LITHIUM_TETRABORATE
  specific = 4
FEATURE [App::DocumentObjectGroupPython] H_element603  label="H_element : 0.264"  # scripted group (container) (typed FeaturePython)
  n = 0.105
FEATURE [App::DocumentObjectGroupPython] C_element648  label="C_element : 0.995"  # scripted group (container) (typed FeaturePython)
  n = 0.083
FEATURE [App::DocumentObjectGroupPython] N_element295  label="N_element : 0.841"  # scripted group (container) (typed FeaturePython)
  n = 0.023
FEATURE [App::DocumentObjectGroupPython] O_element577  label="O_element : 0.989"  # scripted group (container) (typed FeaturePython)
  n = 0.779
FEATURE [App::DocumentObjectGroupPython] Na_element090  label="Na_element : 0.151"  # scripted group (container) (typed FeaturePython)
  n = 0.002
FEATURE [App::DocumentObjectGroupPython] P_element082  label="P_element : 0.143"  # scripted group (container) (typed FeaturePython)
  n = 0.001
FEATURE [App::DocumentObjectGroupPython] S_element108  label="S_element : 0.074"  # scripted group (container) (typed FeaturePython)
  n = 0.002
FEATURE [App::DocumentObjectGroupPython] Cl_element134  label="Cl_element : 0.634"  # scripted group (container) (typed FeaturePython)
  n = 0.003
FEATURE [App::DocumentObjectGroupPython] K_element057  label="K_element : 0.048"  # scripted group (container) (typed FeaturePython)
  n = 0.002
FEATURE [App::DocumentObjectGroupPython] G4_LUNG_ICRP  # scripted group (container) (typed FeaturePython)
  Dunit = g/cm3
  Dvalue = 1.04
  Group = -> [H_element603,C_element648,N_element295,O_element577,Na_element090,P_element082,S_element108,Cl_element134,K_element057]
  conduct = 2
  density = 1
  expand = 3
  formula = G4_LUNG_ICRP
  name = G4_LUNG_ICRP
  specific = 4
FEATURE [App::DocumentObjectGroupPython] H_element604  label="H_element : 0.265"  # scripted group (container) (typed FeaturePython)
  n = 0.114318
FEATURE [App::DocumentObjectGroupPython] C_element649  label="C_element : 0.996"  # scripted group (container) (typed FeaturePython)
  n = 0.655824
FEATURE [App::DocumentObjectGroupPython] O_element578  label="O_element : 0.990"  # scripted group (container) (typed FeaturePython)
  n = 0.0921831
FEATURE [App::DocumentObjectGroupPython] Mg_element048  label="Mg_element : 0.153"  # scripted group (container) (typed FeaturePython)
  n = 0.134792
FEATURE [App::DocumentObjectGroupPython] Ca_element069  label="Ca_element : 0.246"  # scripted group (container) (typed FeaturePython)
  n = 0.002883
FEATURE [App::DocumentObjectGroupPython] G4_M3_WAX  # scripted group (container) (typed FeaturePython)
  Dunit = g/cm3
  Dvalue = 1.05
  Group = -> [H_element604,C_element649,O_element578,Mg_element048,Ca_element069]
  conduct = 2
  density = 1
  expand = 3
  formula = G4_M3_WAX
  name = G4_M3_WAX
  specific = 4
FEATURE [App::DocumentObjectGroupPython] Mg_element049  label="Mg_element : 020"  # scripted group (container) (typed FeaturePython)
  n = 1
  ref = Mg_element
FEATURE [App::DocumentObjectGroupPython] C_element650  label="C_element : 424"  # scripted group (container) (typed FeaturePython)
  n = 1
  ref = C_element
FEATURE [App::DocumentObjectGroupPython] O_element579  label="O_element : 368"  # scripted group (container) (typed FeaturePython)
  n = 3
  ref = O_element
FEATURE [App::DocumentObjectGroupPython] G4_MAGNESIUM_CARBONATE  # scripted group (container) (typed FeaturePython)
  Dunit = g/cm3
  Dvalue = 2.958
  Group = -> [Mg_element049,C_element650,O_element579]
  conduct = 2
  density = 1
  expand = 3
  formula = G4_MAGNESIUM_CARBONATE
  name = G4_MAGNESIUM_CARBONATE
  specific = 4
FEATURE [App::DocumentObjectGroupPython] Mg_element050  label="Mg_element : 021"  # scripted group (container) (typed FeaturePython)
  n = 1
  ref = Mg_element
FEATURE [App::DocumentObjectGroupPython] F_element089  label="F_element : 042"  # scripted group (container) (typed FeaturePython)
  n = 2
  ref = F_element
FEATURE [App::DocumentObjectGroupPython] G4_MAGNESIUM_FLUORIDE  # scripted group (container) (typed FeaturePython)
  Dunit = g/cm3
  Dvalue = 3
  Group = -> [Mg_element050,F_element089]
  conduct = 2
  density = 1
  expand = 3
  formula = G4_MAGNESIUM_FLUORIDE
  name = G4_MAGNESIUM_FLUORIDE
  specific = 4
FEATURE [App::DocumentObjectGroupPython] Mg_element051  label="Mg_element : 022"  # scripted group (container) (typed FeaturePython)
  n = 1
  ref = Mg_element
FEATURE [App::DocumentObjectGroupPython] O_element580  label="O_element : 369"  # scripted group (container) (typed FeaturePython)
  n = 1
  ref = O_element
FEATURE [App::DocumentObjectGroupPython] G4_MAGNESIUM_OXIDE  # scripted group (container) (typed FeaturePython)
  Dunit = g/cm3
  Dvalue = 3.58
  Group = -> [Mg_element051,O_element580]
  conduct = 2
  density = 1
  expand = 3
  formula = G4_MAGNESIUM_OXIDE
  name = G4_MAGNESIUM_OXIDE
  specific = 4
FEATURE [App::DocumentObjectGroupPython] Mg_element052  label="Mg_element : 023"  # scripted group (container) (typed FeaturePython)
  n = 1
  ref = Mg_element
FEATURE [App::DocumentObjectGroupPython] B_element034  label="B_element : 027"  # scripted group (container) (typed FeaturePython)
  n = 4
  ref = B_element
FEATURE [App::DocumentObjectGroupPython] O_element581  label="O_element : 370"  # scripted group (container) (typed FeaturePython)
  n = 7
  ref = O_element
FEATURE [App::DocumentObjectGroupPython] G4_MAGNESIUM_TETRABORATE  # scripted group (container) (typed FeaturePython)
  Dunit = g/cm3
  Dvalue = 2.53
  Group = -> [Mg_element052,B_element034,O_element581]
  conduct = 2
  density = 1
  expand = 3
  formula = G4_MAGNESIUM_TETRABORATE
  name = G4_MAGNESIUM_TETRABORATE
  specific = 4
FEATURE [App::DocumentObjectGroupPython] Hg_element009  label="Hg_element : 008"  # scripted group (container) (typed FeaturePython)
  n = 1
  ref = Hg_element
FEATURE [App::DocumentObjectGroupPython] I_element044  label="I_element : 028"  # scripted group (container) (typed FeaturePython)
  n = 2
  ref = I_element
FEATURE [App::DocumentObjectGroupPython] G4_MERCURIC_IODIDE  # scripted group (container) (typed FeaturePython)
  Dunit = g/cm3
  Dvalue = 6.36
  Group = -> [Hg_element009,I_element044]
  conduct = 2
  density = 1
  expand = 3
  formula = G4_MERCURIC_IODIDE
  name = G4_MERCURIC_IODIDE
  specific = 4
FEATURE [App::DocumentObjectGroupPython] C_element651  label="C_element : 425"  # scripted group (container) (typed FeaturePython)
  n = 1
  ref = C_element
FEATURE [App::DocumentObjectGroupPython] H_element605  label="H_element : 390"  # scripted group (container) (typed FeaturePython)
  n = 4
  ref = H_element
FEATURE [App::DocumentObjectGroupPython] G4_METHANE  # scripted group (container) (typed FeaturePython)
  Dunit = g/cm3
  Dvalue = 0.000667151
  Group = -> [C_element651,H_element605]
  conduct = 2
  density = 1
  expand = 3
  formula = G4_METHANE
  name = G4_METHANE
  specific = 4
FEATURE [App::DocumentObjectGroupPython] C_element652  label="C_element : 426"  # scripted group (container) (typed FeaturePython)
  n = 1
  ref = C_element
FEATURE [App::DocumentObjectGroupPython] H_element606  label="H_element : 391"  # scripted group (container) (typed FeaturePython)
  n = 4
  ref = H_element
FEATURE [App::DocumentObjectGroupPython] O_element582  label="O_element : 371"  # scripted group (container) (typed FeaturePython)
  n = 1
  ref = O_element
FEATURE [App::DocumentObjectGroupPython] G4_METHANOL  # scripted group (container) (typed FeaturePython)
  Dunit = g/cm3
  Dvalue = 0.7914
  Group = -> [C_element652,H_element606,O_element582]
  conduct = 2
  density = 1
  expand = 3
  formula = G4_METHANOL
  name = G4_METHANOL
  specific = 4
FEATURE [App::DocumentObjectGroupPython] H_element607  label="H_element : 0.266"  # scripted group (container) (typed FeaturePython)
  n = 0.13404
FEATURE [App::DocumentObjectGroupPython] C_element653  label="C_element : 0.997"  # scripted group (container) (typed FeaturePython)
  n = 0.77796
FEATURE [App::DocumentObjectGroupPython] O_element583  label="O_element : 0.991"  # scripted group (container) (typed FeaturePython)
  n = 0.03502
FEATURE [App::DocumentObjectGroupPython] Mg_element053  label="Mg_element : 0.154"  # scripted group (container) (typed FeaturePython)
  n = 0.038594
FEATURE [App::DocumentObjectGroupPython] Ti_element018  label="Ti_element : 0.020"  # scripted group (container) (typed FeaturePython)
  n = 0.014386
FEATURE [App::DocumentObjectGroupPython] G4_MIX_D_WAX  # scripted group (container) (typed FeaturePython)
  Dunit = g/cm3
  Dvalue = 0.99
  Group = -> [H_element607,C_element653,O_element583,Mg_element053,Ti_element018]
  conduct = 2
  density = 1
  expand = 3
  formula = G4_MIX_D_WAX
  name = G4_MIX_D_WAX
  specific = 4
FEATURE [App::DocumentObjectGroupPython] H_element608  label="H_element : 0.267"  # scripted group (container) (typed FeaturePython)
  n = 0.081192
FEATURE [App::DocumentObjectGroupPython] C_element654  label="C_element : 0.998"  # scripted group (container) (typed FeaturePython)
  n = 0.583442
FEATURE [App::DocumentObjectGroupPython] N_element296  label="N_element : 0.842"  # scripted group (container) (typed FeaturePython)
  n = 0.017798
FEATURE [App::DocumentObjectGroupPython] O_element584  label="O_element : 0.992"  # scripted group (container) (typed FeaturePython)
  n = 0.186381
FEATURE [App::DocumentObjectGroupPython] Mg_element054  label="Mg_element : 0.155"  # scripted group (container) (typed FeaturePython)
  n = 0.130287
FEATURE [App::DocumentObjectGroupPython] Cl_element135  label="Cl_element : 0.635"  # scripted group (container) (typed FeaturePython)
  n = 0.0009
FEATURE [App::DocumentObjectGroupPython] G4_MS20_TISSUE  # scripted group (container) (typed FeaturePython)
  Dunit = g/cm3
  Dvalue = 1
  Group = -> [H_element608,C_element654,N_element296,O_element584,Mg_element054,Cl_element135]
  conduct = 2
  density = 1
  expand = 3
  formula = G4_MS20_TISSUE
  name = G4_MS20_TISSUE
  specific = 4
FEATURE [App::DocumentObjectGroupPython] H_element609  label="H_element : 0.268"  # scripted group (container) (typed FeaturePython)
  n = 0.102
FEATURE [App::DocumentObjectGroupPython] C_element655  label="C_element : 0.999"  # scripted group (container) (typed FeaturePython)
  n = 0.143
FEATURE [App::DocumentObjectGroupPython] N_element297  label="N_element : 0.843"  # scripted group (container) (typed FeaturePython)
  n = 0.034
FEATURE [App::DocumentObjectGroupPython] O_element585  label="O_element : 0.993"  # scripted group (container) (typed FeaturePython)
  n = 0.71
FEATURE [App::DocumentObjectGroupPython] Na_element091  label="Na_element : 0.152"  # scripted group (container) (typed FeaturePython)
  n = 0.001
FEATURE [App::DocumentObjectGroupPython] P_element083  label="P_element : 0.144"  # scripted group (container) (typed FeaturePython)
  n = 0.002
FEATURE [App::DocumentObjectGroupPython] S_element109  label="S_element : 0.075"  # scripted group (container) (typed FeaturePython)
  n = 0.003
FEATURE [App::DocumentObjectGroupPython] Cl_element136  label="Cl_element : 0.636"  # scripted group (container) (typed FeaturePython)
  n = 0.001
FEATURE [App::DocumentObjectGroupPython] K_element058  label="K_element : 0.049"  # scripted group (container) (typed FeaturePython)
  n = 0.004
FEATURE [App::DocumentObjectGroupPython] G4_MUSCLE_SKELETAL_ICRP  # scripted group (container) (typed FeaturePython)
  Dunit = g/cm3
  Dvalue = 1.05
  Group = -> [H_element609,C_element655,N_element297,O_element585,Na_element091,P_element083,S_element109,Cl_element136,K_element058]
  conduct = 2
  density = 1
  expand = 3
  formula = G4_MUSCLE_SKELETAL_ICRP
  name = G4_MUSCLE_SKELETAL_ICRP
  specific = 4
FEATURE [App::DocumentObjectGroupPython] H_element610  label="H_element : 0.269"  # scripted group (container) (typed FeaturePython)
  n = 0.102102
FEATURE [App::DocumentObjectGroupPython] C_element656  label="C_element : 0.1000"  # scripted group (container) (typed FeaturePython)
  n = 0.123123
FEATURE [App::DocumentObjectGroupPython] N_element298  label="N_element : 0.844"  # scripted group (container) (typed FeaturePython)
  n = 0.035035
FEATURE [App::DocumentObjectGroupPython] O_element586  label="O_element : 0.994"  # scripted group (container) (typed FeaturePython)
  n = 0.72973
FEATURE [App::DocumentObjectGroupPython] Na_element092  label="Na_element : 0.153"  # scripted group (container) (typed FeaturePython)
  n = 0.001001
FEATURE [App::DocumentObjectGroupPython] P_element084  label="P_element : 0.145"  # scripted group (container) (typed FeaturePython)
  n = 0.002002
FEATURE [App::DocumentObjectGroupPython] S_element110  label="S_element : 0.076"  # scripted group (container) (typed FeaturePython)
  n = 0.004004
FEATURE [App::DocumentObjectGroupPython] K_element059  label="K_element : 0.050"  # scripted group (container) (typed FeaturePython)
  n = 0.003003
FEATURE [App::DocumentObjectGroupPython] G4_MUSCLE_STRIATED_ICRU  # scripted group (container) (typed FeaturePython)
  Dunit = g/cm3
  Dvalue = 1.04
  Group = -> [H_element610,C_element656,N_element298,O_element586,Na_element092,P_element084,S_element110,K_element059]
  conduct = 2
  density = 1
  expand = 3
  formula = G4_MUSCLE_STRIATED_ICRU
  name = G4_MUSCLE_STRIATED_ICRU
  specific = 4
FEATURE [App::DocumentObjectGroupPython] H_element611  label="H_element : 0.270"  # scripted group (container) (typed FeaturePython)
  n = 0.0982341
FEATURE [App::DocumentObjectGroupPython] C_element657  label="C_element : 0.1001"  # scripted group (container) (typed FeaturePython)
  n = 0.156214
FEATURE [App::DocumentObjectGroupPython] N_element299  label="N_element : 0.845"  # scripted group (container) (typed FeaturePython)
  n = 0.035451
FEATURE [App::DocumentObjectGroupPython] O_element587  label="O_element : 0.995"  # scripted group (container) (typed FeaturePython)
  n = 0.710101
FEATURE [App::DocumentObjectGroupPython] G4_MUSCLE_WITH_SUCROSE  # scripted group (container) (typed FeaturePython)
  Dunit = g/cm3
  Dvalue = 1.11
  Group = -> [H_element611,C_element657,N_element299,O_element587]
  conduct = 2
  density = 1
  expand = 3
  formula = G4_MUSCLE_WITH_SUCROSE
  name = G4_MUSCLE_WITH_SUCROSE
  specific = 4
FEATURE [App::DocumentObjectGroupPython] H_element612  label="H_element : 0.271"  # scripted group (container) (typed FeaturePython)
  n = 0.101969
FEATURE [App::DocumentObjectGroupPython] C_element658  label="C_element : 0.1002"  # scripted group (container) (typed FeaturePython)
  n = 0.120058
FEATURE [App::DocumentObjectGroupPython] N_element300  label="N_element : 0.846"  # scripted group (container) (typed FeaturePython)
  n = 0.035451
FEATURE [App::DocumentObjectGroupPython] O_element588  label="O_element : 0.996"  # scripted group (container) (typed FeaturePython)
  n = 0.742522
FEATURE [App::DocumentObjectGroupPython] G4_MUSCLE_WITHOUT_SUCROSE  # scripted group (container) (typed FeaturePython)
  Dunit = g/cm3
  Dvalue = 1.07
  Group = -> [H_element612,C_element658,N_element300,O_element588]
  conduct = 2
  density = 1
  expand = 3
  formula = G4_MUSCLE_WITHOUT_SUCROSE
  name = G4_MUSCLE_WITHOUT_SUCROSE
  specific = 4
FEATURE [App::DocumentObjectGroupPython] C_element659  label="C_element : 427"  # scripted group (container) (typed FeaturePython)
  n = 10
  ref = C_element
FEATURE [App::DocumentObjectGroupPython] H_element613  label="H_element : 392"  # scripted group (container) (typed FeaturePython)
  n = 8
  ref = H_element
FEATURE [App::DocumentObjectGroupPython] G4_NAPHTHALENE  # scripted group (container) (typed FeaturePython)
  Dunit = g/cm3
  Dvalue = 1.145
  Group = -> [C_element659,H_element613]
  conduct = 2
  density = 1
  expand = 3
  formula = G4_NAPHTHALENE
  name = G4_NAPHTHALENE
  specific = 4
FEATURE [App::DocumentObjectGroupPython] C_element660  label="C_element : 428"  # scripted group (container) (typed FeaturePython)
  n = 6
  ref = C_element
FEATURE [App::DocumentObjectGroupPython] H_element614  label="H_element : 393"  # scripted group (container) (typed FeaturePython)
  n = 5
  ref = H_element
FEATURE [App::DocumentObjectGroupPython] N_element301  label="N_element : 163"  # scripted group (container) (typed FeaturePython)
  n = 1
  ref = N_element
FEATURE [App::DocumentObjectGroupPython] O_element589  label="O_element : 372"  # scripted group (container) (typed FeaturePython)
  n = 2
  ref = O_element
FEATURE [App::DocumentObjectGroupPython] G4_NITROBENZENE  # scripted group (container) (typed FeaturePython)
  Dunit = g/cm3
  Dvalue = 1.19867
  Group = -> [C_element660,H_element614,N_element301,O_element589]
  conduct = 2
  density = 1
  expand = 3
  formula = G4_NITROBENZENE
  name = G4_NITROBENZENE
  specific = 4
FEATURE [App::DocumentObjectGroupPython] N_element302  label="N_element : 164"  # scripted group (container) (typed FeaturePython)
  n = 2
  ref = N_element
FEATURE [App::DocumentObjectGroupPython] O_element590  label="O_element : 373"  # scripted group (container) (typed FeaturePython)
  n = 1
  ref = O_element
FEATURE [App::DocumentObjectGroupPython] G4_NITROUS_OXIDE  # scripted group (container) (typed FeaturePython)
  Dunit = g/cm3
  Dvalue = 0.00183094
  Group = -> [N_element302,O_element590]
  conduct = 2
  density = 1
  expand = 3
  formula = G4_NITROUS_OXIDE
  name = G4_NITROUS_OXIDE
  specific = 4
FEATURE [App::DocumentObjectGroupPython] H_element615  label="H_element : 0.272"  # scripted group (container) (typed FeaturePython)
  n = 0.103509
FEATURE [App::DocumentObjectGroupPython] C_element661  label="C_element : 0.1003"  # scripted group (container) (typed FeaturePython)
  n = 0.648416
FEATURE [App::DocumentObjectGroupPython] N_element303  label="N_element : 0.847"  # scripted group (container) (typed FeaturePython)
  n = 0.0995361
FEATURE [App::DocumentObjectGroupPython] O_element591  label="O_element : 0.997"  # scripted group (container) (typed FeaturePython)
  n = 0.148539
FEATURE [App::DocumentObjectGroupPython] G4_NYLON_8062  label="G4_NYLON-8062"  # scripted group (container) (typed FeaturePython)
  Dunit = g/cm3
  Dvalue = 1.08
  Group = -> [H_element615,C_element661,N_element303,O_element591]
  conduct = 2
  density = 1
  expand = 3
  formula = G4_NYLON-8062
  name = G4_NYLON-8062
  specific = 4
FEATURE [App::DocumentObjectGroupPython] C_element662  label="C_element : 429"  # scripted group (container) (typed FeaturePython)
  n = 6
  ref = C_element
FEATURE [App::DocumentObjectGroupPython] H_element616  label="H_element : 394"  # scripted group (container) (typed FeaturePython)
  n = 11
  ref = H_element
FEATURE [App::DocumentObjectGroupPython] N_element304  label="N_element : 165"  # scripted group (container) (typed FeaturePython)
  n = 1
  ref = N_element
FEATURE [App::DocumentObjectGroupPython] O_element592  label="O_element : 374"  # scripted group (container) (typed FeaturePython)
  n = 1
  ref = O_element
FEATURE [App::DocumentObjectGroupPython] G4_NYLON_6_6  label="G4_NYLON-6-6"  # scripted group (container) (typed FeaturePython)
  Dunit = g/cm3
  Dvalue = 1.14
  Group = -> [C_element662,H_element616,N_element304,O_element592]
  conduct = 2
  density = 1
  expand = 3
  formula = G4_NYLON-6-6
  name = G4_NYLON-6-6
  specific = 4
FEATURE [App::DocumentObjectGroupPython] H_element617  label="H_element : 0.273"  # scripted group (container) (typed FeaturePython)
  n = 0.107062
FEATURE [App::DocumentObjectGroupPython] C_element663  label="C_element : 0.1004"  # scripted group (container) (typed FeaturePython)
  n = 0.680449
FEATURE [App::DocumentObjectGroupPython] N_element305  label="N_element : 0.848"  # scripted group (container) (typed FeaturePython)
  n = 0.099189
FEATURE [App::DocumentObjectGroupPython] O_element593  label="O_element : 0.998"  # scripted group (container) (typed FeaturePython)
  n = 0.1133
FEATURE [App::DocumentObjectGroupPython] G4_NYLON_6_10  label="G4_NYLON-6-10"  # scripted group (container) (typed FeaturePython)
  Dunit = g/cm3
  Dvalue = 1.14
  Group = -> [H_element617,C_element663,N_element305,O_element593]
  conduct = 2
  density = 1
  expand = 3
  formula = G4_NYLON-6-10
  name = G4_NYLON-6-10
  specific = 4
FEATURE [App::DocumentObjectGroupPython] H_element618  label="H_element : 0.274"  # scripted group (container) (typed FeaturePython)
  n = 0.115476
FEATURE [App::DocumentObjectGroupPython] C_element664  label="C_element : 0.1005"  # scripted group (container) (typed FeaturePython)
  n = 0.720818
FEATURE [App::DocumentObjectGroupPython] N_element306  label="N_element : 0.849"  # scripted group (container) (typed FeaturePython)
  n = 0.0764169
FEATURE [App::DocumentObjectGroupPython] O_element594  label="O_element : 0.999"  # scripted group (container) (typed FeaturePython)
  n = 0.0872889
FEATURE [App::DocumentObjectGroupPython] G4_NYLON_11_RILSAN  label="G4_NYLON-11_RILSAN"  # scripted group (container) (typed FeaturePython)
  Dunit = g/cm3
  Dvalue = 1.425
  Group = -> [H_element618,C_element664,N_element306,O_element594]
  conduct = 2
  density = 1
  expand = 3
  formula = G4_NYLON-11_RILSAN
  name = G4_NYLON-11_RILSAN
  specific = 4
FEATURE [App::DocumentObjectGroupPython] C_element665  label="C_element : 430"  # scripted group (container) (typed FeaturePython)
  n = 8
  ref = C_element
FEATURE [App::DocumentObjectGroupPython] H_element619  label="H_element : 395"  # scripted group (container) (typed FeaturePython)
  n = 18
  ref = H_element
FEATURE [App::DocumentObjectGroupPython] G4_OCTANE  # scripted group (container) (typed FeaturePython)
  Dunit = g/cm3
  Dvalue = 0.7026
  Group = -> [C_element665,H_element619]
  conduct = 2
  density = 1
  expand = 3
  formula = G4_OCTANE
  name = G4_OCTANE
  specific = 4
FEATURE [App::DocumentObjectGroupPython] C_element666  label="C_element : 431"  # scripted group (container) (typed FeaturePython)
  n = 25
  ref = C_element
FEATURE [App::DocumentObjectGroupPython] H_element620  label="H_element : 396"  # scripted group (container) (typed FeaturePython)
  n = 52
  ref = H_element
FEATURE [App::DocumentObjectGroupPython] G4_PARAFFIN  # scripted group (container) (typed FeaturePython)
  Dunit = g/cm3
  Dvalue = 0.93
  Group = -> [C_element666,H_element620]
  conduct = 2
  density = 1
  expand = 3
  formula = G4_PARAFFIN
  name = G4_PARAFFIN
  specific = 4
FEATURE [App::DocumentObjectGroupPython] C_element667  label="C_element : 432"  # scripted group (container) (typed FeaturePython)
  n = 5
  ref = C_element
FEATURE [App::DocumentObjectGroupPython] H_element621  label="H_element : 397"  # scripted group (container) (typed FeaturePython)
  n = 12
  ref = H_element
FEATURE [App::DocumentObjectGroupPython] G4_N_PENTANE  label="G4_N-PENTANE"  # scripted group (container) (typed FeaturePython)
  Dunit = g/cm3
  Dvalue = 0.6262
  Group = -> [C_element667,H_element621]
  conduct = 2
  density = 1
  expand = 3
  formula = G4_N-PENTANE
  name = G4_N-PENTANE
  specific = 4
FEATURE [App::DocumentObjectGroupPython] H_element622  label="H_element : 0.275"  # scripted group (container) (typed FeaturePython)
  n = 0.0141
FEATURE [App::DocumentObjectGroupPython] C_element668  label="C_element : 0.1006"  # scripted group (container) (typed FeaturePython)
  n = 0.072261
FEATURE [App::DocumentObjectGroupPython] N_element307  label="N_element : 0.850"  # scripted group (container) (typed FeaturePython)
  n = 0.01932
FEATURE [App::DocumentObjectGroupPython] O_element595  label="O_element : 0.1000"  # scripted group (container) (typed FeaturePython)
  n = 0.066101
FEATURE [App::DocumentObjectGroupPython] S_element111  label="S_element : 0.077"  # scripted group (container) (typed FeaturePython)
  n = 0.00189
FEATURE [App::DocumentObjectGroupPython] Br_element032  label="Br_element : 0.770"  # scripted group (container) (typed FeaturePython)
  n = 0.349103
FEATURE [App::DocumentObjectGroupPython] Ag_element025  label="Ag_element : 0.579"  # scripted group (container) (typed FeaturePython)
  n = 0.474105
FEATURE [App::DocumentObjectGroupPython] I_element045  label="I_element : 0.658"  # scripted group (container) (typed FeaturePython)
  n = 0.00312
FEATURE [App::DocumentObjectGroupPython] G4_PHOTO_EMULSION  # scripted group (container) (typed FeaturePython)
  Dunit = g/cm3
  Dvalue = 3.815
  Group = -> [H_element622,C_element668,N_element307,O_element595,S_element111,Br_element032,Ag_element025,I_element045]
  conduct = 2
  density = 1
  expand = 3
  formula = G4_PHOTO_EMULSION
  name = G4_PHOTO_EMULSION
  specific = 4
FEATURE [App::DocumentObjectGroupPython] C_element669  label="C_element : 433"  # scripted group (container) (typed FeaturePython)
  n = 9
  ref = C_element
FEATURE [App::DocumentObjectGroupPython] H_element623  label="H_element : 398"  # scripted group (container) (typed FeaturePython)
  n = 10
  ref = H_element
FEATURE [App::DocumentObjectGroupPython] G4_PLASTIC_SC_VINYLTOLUENE  # scripted group (container) (typed FeaturePython)
  Dunit = g/cm3
  Dvalue = 1.032
  Group = -> [C_element669,H_element623]
  conduct = 2
  density = 1
  expand = 3
  formula = G4_PLASTIC_SC_VINYLTOLUENE
  name = G4_PLASTIC_SC_VINYLTOLUENE
  specific = 4
FEATURE [App::DocumentObjectGroupPython] Pu_element009  label="Pu_element : 008"  # scripted group (container) (typed FeaturePython)
  n = 1
  ref = Pu_element
FEATURE [App::DocumentObjectGroupPython] O_element596  label="O_element : 375"  # scripted group (container) (typed FeaturePython)
  n = 2
  ref = O_element
FEATURE [App::DocumentObjectGroupPython] G4_PLUTONIUM_DIOXIDE  # scripted group (container) (typed FeaturePython)
  Dunit = g/cm3
  Dvalue = 11.46
  Group = -> [Pu_element009,O_element596]
  conduct = 2
  density = 1
  expand = 3
  formula = G4_PLUTONIUM_DIOXIDE
  name = G4_PLUTONIUM_DIOXIDE
  specific = 4
FEATURE [App::DocumentObjectGroupPython] C_element670  label="C_element : 434"  # scripted group (container) (typed FeaturePython)
  n = 3
  ref = C_element
FEATURE [App::DocumentObjectGroupPython] H_element624  label="H_element : 399"  # scripted group (container) (typed FeaturePython)
  n = 3
  ref = H_element
FEATURE [App::DocumentObjectGroupPython] N_element308  label="N_element : 166"  # scripted group (container) (typed FeaturePython)
  n = 1
  ref = N_element
FEATURE [App::DocumentObjectGroupPython] G4_POLYACRYLONITRILE  # scripted group (container) (typed FeaturePython)
  Dunit = g/cm3
  Dvalue = 1.17
  Group = -> [C_element670,H_element624,N_element308]
  conduct = 2
  density = 1
  expand = 3
  formula = G4_POLYACRYLONITRILE
  name = G4_POLYACRYLONITRILE
  specific = 4
FEATURE [App::DocumentObjectGroupPython] C_element671  label="C_element : 435"  # scripted group (container) (typed FeaturePython)
  n = 16
  ref = C_element
FEATURE [App::DocumentObjectGroupPython] H_element625  label="H_element : 400"  # scripted group (container) (typed FeaturePython)
  n = 14
  ref = H_element
FEATURE [App::DocumentObjectGroupPython] O_element597  label="O_element : 376"  # scripted group (container) (typed FeaturePython)
  n = 3
  ref = O_element
FEATURE [App::DocumentObjectGroupPython] G4_POLYCARBONATE  # scripted group (container) (typed FeaturePython)
  Dunit = g/cm3
  Dvalue = 1.2
  Group = -> [C_element671,H_element625,O_element597]
  conduct = 2
  density = 1
  expand = 3
  formula = G4_POLYCARBONATE
  name = G4_POLYCARBONATE
  specific = 4
FEATURE [App::DocumentObjectGroupPython] C_element672  label="C_element : 436"  # scripted group (container) (typed FeaturePython)
  n = 8
  ref = C_element
FEATURE [App::DocumentObjectGroupPython] H_element626  label="H_element : 401"  # scripted group (container) (typed FeaturePython)
  n = 7
  ref = H_element
FEATURE [App::DocumentObjectGroupPython] Cl_element137  label="Cl_element : 067"  # scripted group (container) (typed FeaturePython)
  n = 1
  ref = Cl_element
FEATURE [App::DocumentObjectGroupPython] G4_POLYCHLOROSTYRENE  # scripted group (container) (typed FeaturePython)
  Dunit = g/cm3
  Dvalue = 1.3
  Group = -> [C_element672,H_element626,Cl_element137]
  conduct = 2
  density = 1
  expand = 3
  formula = G4_POLYCHLOROSTYRENE
  name = G4_POLYCHLOROSTYRENE
  specific = 4
FEATURE [App::DocumentObjectGroupPython] C_element673  label="C_element : 437"  # scripted group (container) (typed FeaturePython)
  n = 1
  ref = C_element
FEATURE [App::DocumentObjectGroupPython] H_element627  label="H_element : 402"  # scripted group (container) (typed FeaturePython)
  n = 2
  ref = H_element
FEATURE [App::DocumentObjectGroupPython] G4_POLYETHYLENE  # scripted group (container) (typed FeaturePython)
  Dunit = g/cm3
  Dvalue = 0.94
  Group = -> [C_element673,H_element627]
  conduct = 2
  density = 1
  expand = 3
  formula = G4_POLYETHYLENE
  name = G4_POLYETHYLENE
  specific = 4
FEATURE [App::DocumentObjectGroupPython] C_element674  label="C_element : 438"  # scripted group (container) (typed FeaturePython)
  n = 10
  ref = C_element
FEATURE [App::DocumentObjectGroupPython] H_element628  label="H_element : 403"  # scripted group (container) (typed FeaturePython)
  n = 8
  ref = H_element
FEATURE [App::DocumentObjectGroupPython] O_element598  label="O_element : 377"  # scripted group (container) (typed FeaturePython)
  n = 4
  ref = O_element
FEATURE [App::DocumentObjectGroupPython] G4_MYLAR  # scripted group (container) (typed FeaturePython)
  Dunit = g/cm3
  Dvalue = 1.4
  Group = -> [C_element674,H_element628,O_element598]
  conduct = 2
  density = 1
  expand = 3
  formula = G4_MYLAR
  name = G4_MYLAR
  specific = 4
FEATURE [App::DocumentObjectGroupPython] C_element675  label="C_element : 439"  # scripted group (container) (typed FeaturePython)
  n = 5
  ref = C_element
FEATURE [App::DocumentObjectGroupPython] H_element629  label="H_element : 404"  # scripted group (container) (typed FeaturePython)
  n = 8
  ref = H_element
FEATURE [App::DocumentObjectGroupPython] O_element599  label="O_element : 378"  # scripted group (container) (typed FeaturePython)
  n = 2
  ref = O_element
FEATURE [App::DocumentObjectGroupPython] G4_PLEXIGLASS  # scripted group (container) (typed FeaturePython)
  Dunit = g/cm3
  Dvalue = 1.19
  Group = -> [C_element675,H_element629,O_element599]
  conduct = 2
  density = 1
  expand = 3
  formula = G4_PLEXIGLASS
  name = G4_PLEXIGLASS
  specific = 4
FEATURE [App::DocumentObjectGroupPython] C_element676  label="C_element : 440"  # scripted group (container) (typed FeaturePython)
  n = 1
  ref = C_element
FEATURE [App::DocumentObjectGroupPython] H_element630  label="H_element : 405"  # scripted group (container) (typed FeaturePython)
  n = 2
  ref = H_element
FEATURE [App::DocumentObjectGroupPython] O_element600  label="O_element : 379"  # scripted group (container) (typed FeaturePython)
  n = 1
  ref = O_element
FEATURE [App::DocumentObjectGroupPython] G4_POLYOXYMETHYLENE  # scripted group (container) (typed FeaturePython)
  Dunit = g/cm3
  Dvalue = 1.425
  Group = -> [C_element676,H_element630,O_element600]
  conduct = 2
  density = 1
  expand = 3
  formula = G4_POLYOXYMETHYLENE
  name = G4_POLYOXYMETHYLENE
  specific = 4
FEATURE [App::DocumentObjectGroupPython] C_element677  label="C_element : 441"  # scripted group (container) (typed FeaturePython)
  n = 2
  ref = C_element
FEATURE [App::DocumentObjectGroupPython] H_element631  label="H_element : 406"  # scripted group (container) (typed FeaturePython)
  n = 4
  ref = H_element
FEATURE [App::DocumentObjectGroupPython] G4_POLYPROPYLENE  # scripted group (container) (typed FeaturePython)
  Dunit = g/cm3
  Dvalue = 0.9
  Group = -> [C_element677,H_element631]
  conduct = 2
  density = 1
  expand = 3
  formula = G4_POLYPROPYLENE
  name = G4_POLYPROPYLENE
  specific = 4
FEATURE [App::DocumentObjectGroupPython] C_element678  label="C_element : 442"  # scripted group (container) (typed FeaturePython)
  n = 8
  ref = C_element
FEATURE [App::DocumentObjectGroupPython] H_element632  label="H_element : 407"  # scripted group (container) (typed FeaturePython)
  n = 8
  ref = H_element
FEATURE [App::DocumentObjectGroupPython] G4_POLYSTYRENE  # scripted group (container) (typed FeaturePython)
  Dunit = g/cm3
  Dvalue = 1.06
  Group = -> [C_element678,H_element632]
  conduct = 2
  density = 1
  expand = 3
  formula = G4_POLYSTYRENE
  name = G4_POLYSTYRENE
  specific = 4
FEATURE [App::DocumentObjectGroupPython] C_element679  label="C_element : 443"  # scripted group (container) (typed FeaturePython)
  n = 2
  ref = C_element
FEATURE [App::DocumentObjectGroupPython] F_element090  label="F_element : 043"  # scripted group (container) (typed FeaturePython)
  n = 4
  ref = F_element
FEATURE [App::DocumentObjectGroupPython] G4_TEFLON  # scripted group (container) (typed FeaturePython)
  Dunit = g/cm3
  Dvalue = 2.2
  Group = -> [C_element679,F_element090]
  conduct = 2
  density = 1
  expand = 3
  formula = G4_TEFLON
  name = G4_TEFLON
  specific = 4
FEATURE [App::DocumentObjectGroupPython] C_element680  label="C_element : 444"  # scripted group (container) (typed FeaturePython)
  n = 2
  ref = C_element
FEATURE [App::DocumentObjectGroupPython] F_element091  label="F_element : 044"  # scripted group (container) (typed FeaturePython)
  n = 3
  ref = F_element
FEATURE [App::DocumentObjectGroupPython] Cl_element138  label="Cl_element : 068"  # scripted group (container) (typed FeaturePython)
  n = 1
  ref = Cl_element
FEATURE [App::DocumentObjectGroupPython] G4_POLYTRIFLUOROCHLOROETHYLENE  # scripted group (container) (typed FeaturePython)
  Dunit = g/cm3
  Dvalue = 2.1
  Group = -> [C_element680,F_element091,Cl_element138]
  conduct = 2
  density = 1
  expand = 3
  formula = G4_POLYTRIFLUOROCHLOROETHYLENE
  name = G4_POLYTRIFLUOROCHLOROETHYLENE
  specific = 4
FEATURE [App::DocumentObjectGroupPython] C_element681  label="C_element : 445"  # scripted group (container) (typed FeaturePython)
  n = 4
  ref = C_element
FEATURE [App::DocumentObjectGroupPython] H_element633  label="H_element : 408"  # scripted group (container) (typed FeaturePython)
  n = 6
  ref = H_element
FEATURE [App::DocumentObjectGroupPython] O_element601  label="O_element : 380"  # scripted group (container) (typed FeaturePython)
  n = 2
  ref = O_element
FEATURE [App::DocumentObjectGroupPython] G4_POLYVINYL_ACETATE  # scripted group (container) (typed FeaturePython)
  Dunit = g/cm3
  Dvalue = 1.19
  Group = -> [C_element681,H_element633,O_element601]
  conduct = 2
  density = 1
  expand = 3
  formula = G4_POLYVINYL_ACETATE
  name = G4_POLYVINYL_ACETATE
  specific = 4
FEATURE [App::DocumentObjectGroupPython] C_element682  label="C_element : 446"  # scripted group (container) (typed FeaturePython)
  n = 2
  ref = C_element
FEATURE [App::DocumentObjectGroupPython] H_element634  label="H_element : 409"  # scripted group (container) (typed FeaturePython)
  n = 4
  ref = H_element
FEATURE [App::DocumentObjectGroupPython] O_element602  label="O_element : 381"  # scripted group (container) (typed FeaturePython)
  n = 1
  ref = O_element
FEATURE [App::DocumentObjectGroupPython] G4_POLYVINYL_ALCOHOL  # scripted group (container) (typed FeaturePython)
  Dunit = g/cm3
  Dvalue = 1.3
  Group = -> [C_element682,H_element634,O_element602]
  conduct = 2
  density = 1
  expand = 3
  formula = G4_POLYVINYL_ALCOHOL
  name = G4_POLYVINYL_ALCOHOL
  specific = 4
FEATURE [App::DocumentObjectGroupPython] C_element683  label="C_element : 447"  # scripted group (container) (typed FeaturePython)
  n = 8
  ref = C_element
FEATURE [App::DocumentObjectGroupPython] H_element635  label="H_element : 410"  # scripted group (container) (typed FeaturePython)
  n = 14
  ref = H_element
FEATURE [App::DocumentObjectGroupPython] O_element603  label="O_element : 382"  # scripted group (container) (typed FeaturePython)
  n = 2
  ref = O_element
FEATURE [App::DocumentObjectGroupPython] G4_POLYVINYL_BUTYRAL  # scripted group (container) (typed FeaturePython)
  Dunit = g/cm3
  Dvalue = 1.12
  Group = -> [C_element683,H_element635,O_element603]
  conduct = 2
  density = 1
  expand = 3
  formula = G4_POLYVINYL_BUTYRAL
  name = G4_POLYVINYL_BUTYRAL
  specific = 4
FEATURE [App::DocumentObjectGroupPython] C_element684  label="C_element : 448"  # scripted group (container) (typed FeaturePython)
  n = 2
  ref = C_element
FEATURE [App::DocumentObjectGroupPython] H_element636  label="H_element : 411"  # scripted group (container) (typed FeaturePython)
  n = 3
  ref = H_element
FEATURE [App::DocumentObjectGroupPython] Cl_element139  label="Cl_element : 069"  # scripted group (container) (typed FeaturePython)
  n = 1
  ref = Cl_element
FEATURE [App::DocumentObjectGroupPython] G4_POLYVINYL_CHLORIDE  # scripted group (container) (typed FeaturePython)
  Dunit = g/cm3
  Dvalue = 1.3
  Group = -> [C_element684,H_element636,Cl_element139]
  conduct = 2
  density = 1
  expand = 3
  formula = G4_POLYVINYL_CHLORIDE
  name = G4_POLYVINYL_CHLORIDE
  specific = 4
FEATURE [App::DocumentObjectGroupPython] C_element685  label="C_element : 449"  # scripted group (container) (typed FeaturePython)
  n = 2
  ref = C_element
FEATURE [App::DocumentObjectGroupPython] H_element637  label="H_element : 412"  # scripted group (container) (typed FeaturePython)
  n = 2
  ref = H_element
FEATURE [App::DocumentObjectGroupPython] Cl_element140  label="Cl_element : 070"  # scripted group (container) (typed FeaturePython)
  n = 2
  ref = Cl_element
FEATURE [App::DocumentObjectGroupPython] G4_POLYVINYLIDENE_CHLORIDE  # scripted group (container) (typed FeaturePython)
  Dunit = g/cm3
  Dvalue = 1.7
  Group = -> [C_element685,H_element637,Cl_element140]
  conduct = 2
  density = 1
  expand = 3
  formula = G4_POLYVINYLIDENE_CHLORIDE
  name = G4_POLYVINYLIDENE_CHLORIDE
  specific = 4
FEATURE [App::DocumentObjectGroupPython] C_element686  label="C_element : 450"  # scripted group (container) (typed FeaturePython)
  n = 2
  ref = C_element
FEATURE [App::DocumentObjectGroupPython] H_element638  label="H_element : 413"  # scripted group (container) (typed FeaturePython)
  n = 2
  ref = H_element
FEATURE [App::DocumentObjectGroupPython] F_element092  label="F_element : 045"  # scripted group (container) (typed FeaturePython)
  n = 2
  ref = F_element
FEATURE [App::DocumentObjectGroupPython] G4_POLYVINYLIDENE_FLUORIDE  # scripted group (container) (typed FeaturePython)
  Dunit = g/cm3
  Dvalue = 1.76
  Group = -> [C_element686,H_element638,F_element092]
  conduct = 2
  density = 1
  expand = 3
  formula = G4_POLYVINYLIDENE_FLUORIDE
  name = G4_POLYVINYLIDENE_FLUORIDE
  specific = 4
FEATURE [App::DocumentObjectGroupPython] C_element687  label="C_element : 451"  # scripted group (container) (typed FeaturePython)
  n = 6
  ref = C_element
FEATURE [App::DocumentObjectGroupPython] H_element639  label="H_element : 414"  # scripted group (container) (typed FeaturePython)
  n = 9
  ref = H_element
FEATURE [App::DocumentObjectGroupPython] N_element309  label="N_element : 167"  # scripted group (container) (typed FeaturePython)
  n = 1
  ref = N_element
FEATURE [App::DocumentObjectGroupPython] O_element604  label="O_element : 383"  # scripted group (container) (typed FeaturePython)
  n = 1
  ref = O_element
FEATURE [App::DocumentObjectGroupPython] G4_POLYVINYL_PYRROLIDONE  # scripted group (container) (typed FeaturePython)
  Dunit = g/cm3
  Dvalue = 1.25
  Group = -> [C_element687,H_element639,N_element309,O_element604]
  conduct = 2
  density = 1
  expand = 3
  formula = G4_POLYVINYL_PYRROLIDONE
  name = G4_POLYVINYL_PYRROLIDONE
  specific = 4
FEATURE [App::DocumentObjectGroupPython] K_element060  label="K_element : 011"  # scripted group (container) (typed FeaturePython)
  n = 1
  ref = K_element
FEATURE [App::DocumentObjectGroupPython] I_element046  label="I_element : 029"  # scripted group (container) (typed FeaturePython)
  n = 1
  ref = I_element
FEATURE [App::DocumentObjectGroupPython] G4_POTASSIUM_IODIDE  # scripted group (container) (typed FeaturePython)
  Dunit = g/cm3
  Dvalue = 3.13
  Group = -> [K_element060,I_element046]
  conduct = 2
  density = 1
  expand = 3
  formula = G4_POTASSIUM_IODIDE
  name = G4_POTASSIUM_IODIDE
  specific = 4
FEATURE [App::DocumentObjectGroupPython] K_element061  label="K_element : 012"  # scripted group (container) (typed FeaturePython)
  n = 2
  ref = K_element
FEATURE [App::DocumentObjectGroupPython] O_element605  label="O_element : 384"  # scripted group (container) (typed FeaturePython)
  n = 1
  ref = O_element
FEATURE [App::DocumentObjectGroupPython] G4_POTASSIUM_OXIDE  # scripted group (container) (typed FeaturePython)
  Dunit = g/cm3
  Dvalue = 2.32
  Group = -> [K_element061,O_element605]
  conduct = 2
  density = 1
  expand = 3
  formula = G4_POTASSIUM_OXIDE
  name = G4_POTASSIUM_OXIDE
  specific = 4
FEATURE [App::DocumentObjectGroupPython] C_element688  label="C_element : 452"  # scripted group (container) (typed FeaturePython)
  n = 3
  ref = C_element
FEATURE [App::DocumentObjectGroupPython] H_element640  label="H_element : 415"  # scripted group (container) (typed FeaturePython)
  n = 8
  ref = H_element
FEATURE [App::DocumentObjectGroupPython] G4_PROPANE  # scripted group (container) (typed FeaturePython)
  Dunit = g/cm3
  Dvalue = 0.00187939
  Group = -> [C_element688,H_element640]
  conduct = 2
  density = 1
  expand = 3
  formula = G4_PROPANE
  name = G4_PROPANE
  specific = 4
FEATURE [App::DocumentObjectGroupPython] C_element689  label="C_element : 453"  # scripted group (container) (typed FeaturePython)
  n = 3
  ref = C_element
FEATURE [App::DocumentObjectGroupPython] H_element641  label="H_element : 416"  # scripted group (container) (typed FeaturePython)
  n = 8
  ref = H_element
FEATURE [App::DocumentObjectGroupPython] G4_lPROPANE  # scripted group (container) (typed FeaturePython)
  Dunit = g/cm3
  Dvalue = 0.43
  Group = -> [C_element689,H_element641]
  conduct = 2
  density = 1
  expand = 3
  formula = G4_lPROPANE
  name = G4_lPROPANE
  specific = 4
FEATURE [App::DocumentObjectGroupPython] C_element690  label="C_element : 454"  # scripted group (container) (typed FeaturePython)
  n = 3
  ref = C_element
FEATURE [App::DocumentObjectGroupPython] H_element642  label="H_element : 417"  # scripted group (container) (typed FeaturePython)
  n = 8
  ref = H_element
FEATURE [App::DocumentObjectGroupPython] O_element606  label="O_element : 385"  # scripted group (container) (typed FeaturePython)
  n = 1
  ref = O_element
FEATURE [App::DocumentObjectGroupPython] G4_N_PROPYL_ALCOHOL  label="G4_N-PROPYL_ALCOHOL"  # scripted group (container) (typed FeaturePython)
  Dunit = g/cm3
  Dvalue = 0.8035
  Group = -> [C_element690,H_element642,O_element606]
  conduct = 2
  density = 1
  expand = 3
  formula = G4_N-PROPYL_ALCOHOL
  name = G4_N-PROPYL_ALCOHOL
  specific = 4
FEATURE [App::DocumentObjectGroupPython] C_element691  label="C_element : 455"  # scripted group (container) (typed FeaturePython)
  n = 5
  ref = C_element
FEATURE [App::DocumentObjectGroupPython] H_element643  label="H_element : 418"  # scripted group (container) (typed FeaturePython)
  n = 5
  ref = H_element
FEATURE [App::DocumentObjectGroupPython] N_element310  label="N_element : 168"  # scripted group (container) (typed FeaturePython)
  n = 1
  ref = N_element
FEATURE [App::DocumentObjectGroupPython] G4_PYRIDINE  # scripted group (container) (typed FeaturePython)
  Dunit = g/cm3
  Dvalue = 0.9819
  Group = -> [C_element691,H_element643,N_element310]
  conduct = 2
  density = 1
  expand = 3
  formula = G4_PYRIDINE
  name = G4_PYRIDINE
  specific = 4
FEATURE [App::DocumentObjectGroupPython] H_element644  label="H_element : 0.276"  # scripted group (container) (typed FeaturePython)
  n = 0.143711
FEATURE [App::DocumentObjectGroupPython] C_element692  label="C_element : 0.1007"  # scripted group (container) (typed FeaturePython)
  n = 0.856289
FEATURE [App::DocumentObjectGroupPython] G4_RUBBER_BUTYL  # scripted group (container) (typed FeaturePython)
  Dunit = g/cm3
  Dvalue = 0.92
  Group = -> [H_element644,C_element692]
  conduct = 2
  density = 1
  expand = 3
  formula = G4_RUBBER_BUTYL
  name = G4_RUBBER_BUTYL
  specific = 4
FEATURE [App::DocumentObjectGroupPython] H_element645  label="H_element : 0.277"  # scripted group (container) (typed FeaturePython)
  n = 0.118371
FEATURE [App::DocumentObjectGroupPython] C_element693  label="C_element : 0.1008"  # scripted group (container) (typed FeaturePython)
  n = 0.881629
FEATURE [App::DocumentObjectGroupPython] G4_RUBBER_NATURAL  # scripted group (container) (typed FeaturePython)
  Dunit = g/cm3
  Dvalue = 0.92
  Group = -> [H_element645,C_element693]
  conduct = 2
  density = 1
  expand = 3
  formula = G4_RUBBER_NATURAL
  name = G4_RUBBER_NATURAL
  specific = 4
FEATURE [App::DocumentObjectGroupPython] H_element646  label="H_element : 0.278"  # scripted group (container) (typed FeaturePython)
  n = 0.05692
FEATURE [App::DocumentObjectGroupPython] C_element694  label="C_element : 0.1009"  # scripted group (container) (typed FeaturePython)
  n = 0.542646
FEATURE [App::DocumentObjectGroupPython] Cl_element141  label="Cl_element : 0.637"  # scripted group (container) (typed FeaturePython)
  n = 0.400434
FEATURE [App::DocumentObjectGroupPython] G4_RUBBER_NEOPRENE  # scripted group (container) (typed FeaturePython)
  Dunit = g/cm3
  Dvalue = 1.23
  Group = -> [H_element646,C_element694,Cl_element141]
  conduct = 2
  density = 1
  expand = 3
  formula = G4_RUBBER_NEOPRENE
  name = G4_RUBBER_NEOPRENE
  specific = 4
FEATURE [App::DocumentObjectGroupPython] Si_element034  label="Si_element : 008"  # scripted group (container) (typed FeaturePython)
  n = 1
  ref = Si_element
FEATURE [App::DocumentObjectGroupPython] O_element607  label="O_element : 386"  # scripted group (container) (typed FeaturePython)
  n = 2
  ref = O_element
FEATURE [App::DocumentObjectGroupPython] G4_SILICON_DIOXIDE  # scripted group (container) (typed FeaturePython)
  Dunit = g/cm3
  Dvalue = 2.32
  Group = -> [Si_element034,O_element607]
  conduct = 2
  density = 1
  expand = 3
  formula = G4_SILICON_DIOXIDE
  name = G4_SILICON_DIOXIDE
  specific = 4
FEATURE [App::DocumentObjectGroupPython] Ag_element026  label="Ag_element : 016"  # scripted group (container) (typed FeaturePython)
  n = 1
  ref = Ag_element
FEATURE [App::DocumentObjectGroupPython] Br_element033  label="Br_element : 018"  # scripted group (container) (typed FeaturePython)
  n = 1
  ref = Br_element
FEATURE [App::DocumentObjectGroupPython] G4_SILVER_BROMIDE  # scripted group (container) (typed FeaturePython)
  Dunit = g/cm3
  Dvalue = 6.473
  Group = -> [Ag_element026,Br_element033]
  conduct = 2
  density = 1
  expand = 3
  formula = G4_SILVER_BROMIDE
  name = G4_SILVER_BROMIDE
  specific = 4
FEATURE [App::DocumentObjectGroupPython] Ag_element027  label="Ag_element : 017"  # scripted group (container) (typed FeaturePython)
  n = 1
  ref = Ag_element
FEATURE [App::DocumentObjectGroupPython] Cl_element142  label="Cl_element : 071"  # scripted group (container) (typed FeaturePython)
  n = 1
  ref = Cl_element
FEATURE [App::DocumentObjectGroupPython] G4_SILVER_CHLORIDE  # scripted group (container) (typed FeaturePython)
  Dunit = g/cm3
  Dvalue = 5.56
  Group = -> [Ag_element027,Cl_element142]
  conduct = 2
  density = 1
  expand = 3
  formula = G4_SILVER_CHLORIDE
  name = G4_SILVER_CHLORIDE
  specific = 4
FEATURE [App::DocumentObjectGroupPython] Br_element034  label="Br_element : 0.771"  # scripted group (container) (typed FeaturePython)
  n = 0.422895
FEATURE [App::DocumentObjectGroupPython] Ag_element028  label="Ag_element : 0.580"  # scripted group (container) (typed FeaturePython)
  n = 0.573748
FEATURE [App::DocumentObjectGroupPython] I_element047  label="I_element : 0.659"  # scripted group (container) (typed FeaturePython)
  n = 0.003357
FEATURE [App::DocumentObjectGroupPython] G4_SILVER_HALIDES  # scripted group (container) (typed FeaturePython)
  Dunit = g/cm3
  Dvalue = 6.47
  Group = -> [Br_element034,Ag_element028,I_element047]
  conduct = 2
  density = 1
  expand = 3
  formula = G4_SILVER_HALIDES
  name = G4_SILVER_HALIDES
  specific = 4
FEATURE [App::DocumentObjectGroupPython] Ag_element029  label="Ag_element : 018"  # scripted group (container) (typed FeaturePython)
  n = 1
  ref = Ag_element
FEATURE [App::DocumentObjectGroupPython] I_element048  label="I_element : 030"  # scripted group (container) (typed FeaturePython)
  n = 1
  ref = I_element
FEATURE [App::DocumentObjectGroupPython] G4_SILVER_IODIDE  # scripted group (container) (typed FeaturePython)
  Dunit = g/cm3
  Dvalue = 6.01
  Group = -> [Ag_element029,I_element048]
  conduct = 2
  density = 1
  expand = 3
  formula = G4_SILVER_IODIDE
  name = G4_SILVER_IODIDE
  specific = 4
FEATURE [App::DocumentObjectGroupPython] H_element647  label="H_element : 0.279"  # scripted group (container) (typed FeaturePython)
  n = 0.1
FEATURE [App::DocumentObjectGroupPython] C_element695  label="C_element : 0.1010"  # scripted group (container) (typed FeaturePython)
  n = 0.204
FEATURE [App::DocumentObjectGroupPython] N_element311  label="N_element : 0.851"  # scripted group (container) (typed FeaturePython)
  n = 0.042
FEATURE [App::DocumentObjectGroupPython] O_element608  label="O_element : 0.1001"  # scripted group (container) (typed FeaturePython)
  n = 0.645
FEATURE [App::DocumentObjectGroupPython] Na_element093  label="Na_element : 0.154"  # scripted group (container) (typed FeaturePython)
  n = 0.002
FEATURE [App::DocumentObjectGroupPython] P_element085  label="P_element : 0.146"  # scripted group (container) (typed FeaturePython)
  n = 0.001
FEATURE [App::DocumentObjectGroupPython] S_element112  label="S_element : 0.078"  # scripted group (container) (typed FeaturePython)
  n = 0.002
FEATURE [App::DocumentObjectGroupPython] Cl_element143  label="Cl_element : 0.638"  # scripted group (container) (typed FeaturePython)
  n = 0.003
FEATURE [App::DocumentObjectGroupPython] K_element062  label="K_element : 0.051"  # scripted group (container) (typed FeaturePython)
  n = 0.001
FEATURE [App::DocumentObjectGroupPython] G4_SKIN_ICRP  # scripted group (container) (typed FeaturePython)
  Dunit = g/cm3
  Dvalue = 1.09
  Group = -> [H_element647,C_element695,N_element311,O_element608,Na_element093,P_element085,S_element112,Cl_element143,K_element062]
  conduct = 2
  density = 1
  expand = 3
  formula = G4_SKIN_ICRP
  name = G4_SKIN_ICRP
  specific = 4
FEATURE [App::DocumentObjectGroupPython] Na_element094  label="Na_element : 019"  # scripted group (container) (typed FeaturePython)
  n = 2
  ref = Na_element
FEATURE [App::DocumentObjectGroupPython] C_element696  label="C_element : 456"  # scripted group (container) (typed FeaturePython)
  n = 1
  ref = C_element
FEATURE [App::DocumentObjectGroupPython] O_element609  label="O_element : 387"  # scripted group (container) (typed FeaturePython)
  n = 3
  ref = O_element
FEATURE [App::DocumentObjectGroupPython] G4_SODIUM_CARBONATE  # scripted group (container) (typed FeaturePython)
  Dunit = g/cm3
  Dvalue = 2.532
  Group = -> [Na_element094,C_element696,O_element609]
  conduct = 2
  density = 1
  expand = 3
  formula = G4_SODIUM_CARBONATE
  name = G4_SODIUM_CARBONATE
  specific = 4
FEATURE [App::DocumentObjectGroupPython] Na_element095  label="Na_element : 020"  # scripted group (container) (typed FeaturePython)
  n = 1
  ref = Na_element
FEATURE [App::DocumentObjectGroupPython] I_element049  label="I_element : 031"  # scripted group (container) (typed FeaturePython)
  n = 1
  ref = I_element
FEATURE [App::DocumentObjectGroupPython] G4_SODIUM_IODIDE  # scripted group (container) (typed FeaturePython)
  Dunit = g/cm3
  Dvalue = 3.667
  Group = -> [Na_element095,I_element049]
  conduct = 2
  density = 1
  expand = 3
  formula = G4_SODIUM_IODIDE
  name = G4_SODIUM_IODIDE
  specific = 4
FEATURE [App::DocumentObjectGroupPython] Na_element096  label="Na_element : 021"  # scripted group (container) (typed FeaturePython)
  n = 2
  ref = Na_element
FEATURE [App::DocumentObjectGroupPython] O_element610  label="O_element : 388"  # scripted group (container) (typed FeaturePython)
  n = 1
  ref = O_element
FEATURE [App::DocumentObjectGroupPython] G4_SODIUM_MONOXIDE  # scripted group (container) (typed FeaturePython)
  Dunit = g/cm3
  Dvalue = 2.27
  Group = -> [Na_element096,O_element610]
  conduct = 2
  density = 1
  expand = 3
  formula = G4_SODIUM_MONOXIDE
  name = G4_SODIUM_MONOXIDE
  specific = 4
FEATURE [App::DocumentObjectGroupPython] Na_element097  label="Na_element : 022"  # scripted group (container) (typed FeaturePython)
  n = 1
  ref = Na_element
FEATURE [App::DocumentObjectGroupPython] N_element312  label="N_element : 169"  # scripted group (container) (typed FeaturePython)
  n = 1
  ref = N_element
FEATURE [App::DocumentObjectGroupPython] O_element611  label="O_element : 389"  # scripted group (container) (typed FeaturePython)
  n = 3
  ref = O_element
FEATURE [App::DocumentObjectGroupPython] G4_SODIUM_NITRATE  # scripted group (container) (typed FeaturePython)
  Dunit = g/cm3
  Dvalue = 2.261
  Group = -> [Na_element097,N_element312,O_element611]
  conduct = 2
  density = 1
  expand = 3
  formula = G4_SODIUM_NITRATE
  name = G4_SODIUM_NITRATE
  specific = 4
FEATURE [App::DocumentObjectGroupPython] C_element697  label="C_element : 457"  # scripted group (container) (typed FeaturePython)
  n = 14
  ref = C_element
FEATURE [App::DocumentObjectGroupPython] H_element648  label="H_element : 419"  # scripted group (container) (typed FeaturePython)
  n = 12
  ref = H_element
FEATURE [App::DocumentObjectGroupPython] G4_STILBENE  # scripted group (container) (typed FeaturePython)
  Dunit = g/cm3
  Dvalue = 0.9707
  Group = -> [C_element697,H_element648]
  conduct = 2
  density = 1
  expand = 3
  formula = G4_STILBENE
  name = G4_STILBENE
  specific = 4
FEATURE [App::DocumentObjectGroupPython] C_element698  label="C_element : 458"  # scripted group (container) (typed FeaturePython)
  n = 12
  ref = C_element
FEATURE [App::DocumentObjectGroupPython] H_element649  label="H_element : 420"  # scripted group (container) (typed FeaturePython)
  n = 22
  ref = H_element
FEATURE [App::DocumentObjectGroupPython] O_element612  label="O_element : 390"  # scripted group (container) (typed FeaturePython)
  n = 11
  ref = O_element
FEATURE [App::DocumentObjectGroupPython] G4_SUCROSE  # scripted group (container) (typed FeaturePython)
  Dunit = g/cm3
  Dvalue = 1.5805
  Group = -> [C_element698,H_element649,O_element612]
  conduct = 2
  density = 1
  expand = 3
  formula = G4_SUCROSE
  name = G4_SUCROSE
  specific = 4
FEATURE [App::DocumentObjectGroupPython] C_element699  label="C_element : 459"  # scripted group (container) (typed FeaturePython)
  n = 18
  ref = C_element
FEATURE [App::DocumentObjectGroupPython] H_element650  label="H_element : 421"  # scripted group (container) (typed FeaturePython)
  n = 14
  ref = H_element
FEATURE [App::DocumentObjectGroupPython] G4_TERPHENYL  # scripted group (container) (typed FeaturePython)
  Dunit = g/cm3
  Dvalue = 1.24
  Group = -> [C_element699,H_element650]
  conduct = 2
  density = 1
  expand = 3
  formula = G4_TERPHENYL
  name = G4_TERPHENYL
  specific = 4
FEATURE [App::DocumentObjectGroupPython] H_element651  label="H_element : 0.280"  # scripted group (container) (typed FeaturePython)
  n = 0.106
FEATURE [App::DocumentObjectGroupPython] C_element700  label="C_element : 0.1011"  # scripted group (container) (typed FeaturePython)
  n = 0.099
FEATURE [App::DocumentObjectGroupPython] N_element313  label="N_element : 0.852"  # scripted group (container) (typed FeaturePython)
  n = 0.02
FEATURE [App::DocumentObjectGroupPython] O_element613  label="O_element : 0.1002"  # scripted group (container) (typed FeaturePython)
  n = 0.766
FEATURE [App::DocumentObjectGroupPython] Na_element098  label="Na_element : 0.155"  # scripted group (container) (typed FeaturePython)
  n = 0.002
FEATURE [App::DocumentObjectGroupPython] P_element086  label="P_element : 0.147"  # scripted group (container) (typed FeaturePython)
  n = 0.001
FEATURE [App::DocumentObjectGroupPython] S_element113  label="S_element : 0.079"  # scripted group (container) (typed FeaturePython)
  n = 0.002
FEATURE [App::DocumentObjectGroupPython] Cl_element144  label="Cl_element : 0.639"  # scripted group (container) (typed FeaturePython)
  n = 0.002
FEATURE [App::DocumentObjectGroupPython] K_element063  label="K_element : 0.052"  # scripted group (container) (typed FeaturePython)
  n = 0.002
FEATURE [App::DocumentObjectGroupPython] G4_TESTIS_ICRP  # scripted group (container) (typed FeaturePython)
  Dunit = g/cm3
  Dvalue = 1.04
  Group = -> [H_element651,C_element700,N_element313,O_element613,Na_element098,P_element086,S_element113,Cl_element144,K_element063]
  conduct = 2
  density = 1
  expand = 3
  formula = G4_TESTIS_ICRP
  name = G4_TESTIS_ICRP
  specific = 4
FEATURE [App::DocumentObjectGroupPython] C_element701  label="C_element : 460"  # scripted group (container) (typed FeaturePython)
  n = 2
  ref = C_element
FEATURE [App::DocumentObjectGroupPython] Cl_element145  label="Cl_element : 072"  # scripted group (container) (typed FeaturePython)
  n = 4
  ref = Cl_element
FEATURE [App::DocumentObjectGroupPython] G4_TETRACHLOROETHYLENE  # scripted group (container) (typed FeaturePython)
  Dunit = g/cm3
  Dvalue = 1.625
  Group = -> [C_element701,Cl_element145]
  conduct = 2
  density = 1
  expand = 3
  formula = G4_TETRACHLOROETHYLENE
  name = G4_TETRACHLOROETHYLENE
  specific = 4
FEATURE [App::DocumentObjectGroupPython] Tl_element009  label="Tl_element : 008"  # scripted group (container) (typed FeaturePython)
  n = 1
  ref = Tl_element
FEATURE [App::DocumentObjectGroupPython] Cl_element146  label="Cl_element : 073"  # scripted group (container) (typed FeaturePython)
  n = 1
  ref = Cl_element
FEATURE [App::DocumentObjectGroupPython] G4_THALLIUM_CHLORIDE  # scripted group (container) (typed FeaturePython)
  Dunit = g/cm3
  Dvalue = 7.004
  Group = -> [Tl_element009,Cl_element146]
  conduct = 2
  density = 1
  expand = 3
  formula = G4_THALLIUM_CHLORIDE
  name = G4_THALLIUM_CHLORIDE
  specific = 4
FEATURE [App::DocumentObjectGroupPython] H_element652  label="H_element : 0.281"  # scripted group (container) (typed FeaturePython)
  n = 0.105
FEATURE [App::DocumentObjectGroupPython] C_element702  label="C_element : 0.1012"  # scripted group (container) (typed FeaturePython)
  n = 0.256
FEATURE [App::DocumentObjectGroupPython] N_element314  label="N_element : 0.853"  # scripted group (container) (typed FeaturePython)
  n = 0.027
FEATURE [App::DocumentObjectGroupPython] O_element614  label="O_element : 0.1003"  # scripted group (container) (typed FeaturePython)
  n = 0.602
FEATURE [App::DocumentObjectGroupPython] Na_element099  label="Na_element : 0.156"  # scripted group (container) (typed FeaturePython)
  n = 0.001
FEATURE [App::DocumentObjectGroupPython] P_element087  label="P_element : 0.148"  # scripted group (container) (typed FeaturePython)
  n = 0.002
FEATURE [App::DocumentObjectGroupPython] S_element114  label="S_element : 0.080"  # scripted group (container) (typed FeaturePython)
  n = 0.003
FEATURE [App::DocumentObjectGroupPython] Cl_element147  label="Cl_element : 0.640"  # scripted group (container) (typed FeaturePython)
  n = 0.002
FEATURE [App::DocumentObjectGroupPython] K_element064  label="K_element : 0.053"  # scripted group (container) (typed FeaturePython)
  n = 0.002
FEATURE [App::DocumentObjectGroupPython] G4_TISSUE_SOFT_ICRP  # scripted group (container) (typed FeaturePython)
  Dunit = g/cm3
  Dvalue = 1.03
  Group = -> [H_element652,C_element702,N_element314,O_element614,Na_element099,P_element087,S_element114,Cl_element147,K_element064]
  conduct = 2
  density = 1
  expand = 3
  formula = G4_TISSUE_SOFT_ICRP
  name = G4_TISSUE_SOFT_ICRP
  specific = 4
FEATURE [App::DocumentObjectGroupPython] H_element653  label="H_element : 0.282"  # scripted group (container) (typed FeaturePython)
  n = 0.101
FEATURE [App::DocumentObjectGroupPython] C_element703  label="C_element : 0.1013"  # scripted group (container) (typed FeaturePython)
  n = 0.111
FEATURE [App::DocumentObjectGroupPython] N_element315  label="N_element : 0.854"  # scripted group (container) (typed FeaturePython)
  n = 0.026
FEATURE [App::DocumentObjectGroupPython] O_element615  label="O_element : 0.1004"  # scripted group (container) (typed FeaturePython)
  n = 0.762
FEATURE [App::DocumentObjectGroupPython] G4_TISSUE_SOFT_ICRU_4  label="G4_TISSUE_SOFT_ICRU-4"  # scripted group (container) (typed FeaturePython)
  Dunit = g/cm3
  Dvalue = 1
  Group = -> [H_element653,C_element703,N_element315,O_element615]
  conduct = 2
  density = 1
  expand = 3
  formula = G4_TISSUE_SOFT_ICRU-4
  name = G4_TISSUE_SOFT_ICRU-4
  specific = 4
FEATURE [App::DocumentObjectGroupPython] H_element654  label="H_element : 0.283"  # scripted group (container) (typed FeaturePython)
  n = 0.101869
FEATURE [App::DocumentObjectGroupPython] C_element704  label="C_element : 0.1014"  # scripted group (container) (typed FeaturePython)
  n = 0.456179
FEATURE [App::DocumentObjectGroupPython] N_element316  label="N_element : 0.855"  # scripted group (container) (typed FeaturePython)
  n = 0.035172
FEATURE [App::DocumentObjectGroupPython] O_element616  label="O_element : 0.1005"  # scripted group (container) (typed FeaturePython)
  n = 0.40678
FEATURE [App::DocumentObjectGroupPython] G4_TISSUE_METHANE  label="G4_TISSUE-METHANE"  # scripted group (container) (typed FeaturePython)
  Dunit = g/cm3
  Dvalue = 0.00106409
  Group = -> [H_element654,C_element704,N_element316,O_element616]
  conduct = 2
  density = 1
  expand = 3
  formula = G4_TISSUE-METHANE
  name = G4_TISSUE-METHANE
  specific = 4
FEATURE [App::DocumentObjectGroupPython] H_element655  label="H_element : 0.284"  # scripted group (container) (typed FeaturePython)
  n = 0.102672
FEATURE [App::DocumentObjectGroupPython] C_element705  label="C_element : 0.1015"  # scripted group (container) (typed FeaturePython)
  n = 0.56894
FEATURE [App::DocumentObjectGroupPython] N_element317  label="N_element : 0.856"  # scripted group (container) (typed FeaturePython)
  n = 0.035022
FEATURE [App::DocumentObjectGroupPython] O_element617  label="O_element : 0.1006"  # scripted group (container) (typed FeaturePython)
  n = 0.293366
FEATURE [App::DocumentObjectGroupPython] G4_TISSUE_PROPANE  label="G4_TISSUE-PROPANE"  # scripted group (container) (typed FeaturePython)
  Dunit = g/cm3
  Dvalue = 0.00182628
  Group = -> [H_element655,C_element705,N_element317,O_element617]
  conduct = 2
  density = 1
  expand = 3
  formula = G4_TISSUE-PROPANE
  name = G4_TISSUE-PROPANE
  specific = 4
FEATURE [App::DocumentObjectGroupPython] Ti_element019  label="Ti_element : 008"  # scripted group (container) (typed FeaturePython)
  n = 1
  ref = Ti_element
FEATURE [App::DocumentObjectGroupPython] O_element618  label="O_element : 391"  # scripted group (container) (typed FeaturePython)
  n = 2
  ref = O_element
FEATURE [App::DocumentObjectGroupPython] G4_TITANIUM_DIOXIDE  # scripted group (container) (typed FeaturePython)
  Dunit = g/cm3
  Dvalue = 4.26
  Group = -> [Ti_element019,O_element618]
  conduct = 2
  density = 1
  expand = 3
  formula = G4_TITANIUM_DIOXIDE
  name = G4_TITANIUM_DIOXIDE
  specific = 4
FEATURE [App::DocumentObjectGroupPython] C_element706  label="C_element : 461"  # scripted group (container) (typed FeaturePython)
  n = 7
  ref = C_element
FEATURE [App::DocumentObjectGroupPython] H_element656  label="H_element : 422"  # scripted group (container) (typed FeaturePython)
  n = 8
  ref = H_element
FEATURE [App::DocumentObjectGroupPython] G4_TOLUENE  # scripted group (container) (typed FeaturePython)
  Dunit = g/cm3
  Dvalue = 0.8669
  Group = -> [C_element706,H_element656]
  conduct = 2
  density = 1
  expand = 3
  formula = G4_TOLUENE
  name = G4_TOLUENE
  specific = 4
FEATURE [App::DocumentObjectGroupPython] C_element707  label="C_element : 462"  # scripted group (container) (typed FeaturePython)
  n = 2
  ref = C_element
FEATURE [App::DocumentObjectGroupPython] H_element657  label="H_element : 423"  # scripted group (container) (typed FeaturePython)
  n = 1
  ref = H_element
FEATURE [App::DocumentObjectGroupPython] Cl_element148  label="Cl_element : 074"  # scripted group (container) (typed FeaturePython)
  n = 3
  ref = Cl_element
FEATURE [App::DocumentObjectGroupPython] G4_TRICHLOROETHYLENE  # scripted group (container) (typed FeaturePython)
  Dunit = g/cm3
  Dvalue = 1.46
  Group = -> [C_element707,H_element657,Cl_element148]
  conduct = 2
  density = 1
  expand = 3
  formula = G4_TRICHLOROETHYLENE
  name = G4_TRICHLOROETHYLENE
  specific = 4
FEATURE [App::DocumentObjectGroupPython] C_element708  label="C_element : 463"  # scripted group (container) (typed FeaturePython)
  n = 6
  ref = C_element
FEATURE [App::DocumentObjectGroupPython] H_element658  label="H_element : 424"  # scripted group (container) (typed FeaturePython)
  n = 15
  ref = H_element
FEATURE [App::DocumentObjectGroupPython] O_element619  label="O_element : 392"  # scripted group (container) (typed FeaturePython)
  n = 4
  ref = O_element
FEATURE [App::DocumentObjectGroupPython] P_element088  label="P_element : 032"  # scripted group (container) (typed FeaturePython)
  n = 1
  ref = P_element
FEATURE [App::DocumentObjectGroupPython] G4_TRIETHYL_PHOSPHATE  # scripted group (container) (typed FeaturePython)
  Dunit = g/cm3
  Dvalue = 1.07
  Group = -> [C_element708,H_element658,O_element619,P_element088]
  conduct = 2
  density = 1
  expand = 3
  formula = G4_TRIETHYL_PHOSPHATE
  name = G4_TRIETHYL_PHOSPHATE
  specific = 4
FEATURE [App::DocumentObjectGroupPython] W_element023  label="W_element : 022"  # scripted group (container) (typed FeaturePython)
  n = 1
  ref = W_element
FEATURE [App::DocumentObjectGroupPython] F_element093  label="F_element : 046"  # scripted group (container) (typed FeaturePython)
  n = 6
  ref = F_element
FEATURE [App::DocumentObjectGroupPython] G4_TUNGSTEN_HEXAFLUORIDE  # scripted group (container) (typed FeaturePython)
  Dunit = g/cm3
  Dvalue = 2.4
  Group = -> [W_element023,F_element093]
  conduct = 2
  density = 1
  expand = 3
  formula = G4_TUNGSTEN_HEXAFLUORIDE
  name = G4_TUNGSTEN_HEXAFLUORIDE
  specific = 4
FEATURE [App::DocumentObjectGroupPython] U_element017  label="U_element : 016"  # scripted group (container) (typed FeaturePython)
  n = 1
  ref = U_element
FEATURE [App::DocumentObjectGroupPython] C_element709  label="C_element : 464"  # scripted group (container) (typed FeaturePython)
  n = 2
  ref = C_element
FEATURE [App::DocumentObjectGroupPython] G4_URANIUM_DICARBIDE  # scripted group (container) (typed FeaturePython)
  Dunit = g/cm3
  Dvalue = 11.28
  Group = -> [U_element017,C_element709]
  conduct = 2
  density = 1
  expand = 3
  formula = G4_URANIUM_DICARBIDE
  name = G4_URANIUM_DICARBIDE
  specific = 4
FEATURE [App::DocumentObjectGroupPython] U_element018  label="U_element : 017"  # scripted group (container) (typed FeaturePython)
  n = 1
  ref = U_element
FEATURE [App::DocumentObjectGroupPython] C_element710  label="C_element : 465"  # scripted group (container) (typed FeaturePython)
  n = 1
  ref = C_element
FEATURE [App::DocumentObjectGroupPython] G4_URANIUM_MONOCARBIDE  # scripted group (container) (typed FeaturePython)
  Dunit = g/cm3
  Dvalue = 13.63
  Group = -> [U_element018,C_element710]
  conduct = 2
  density = 1
  expand = 3
  formula = G4_URANIUM_MONOCARBIDE
  name = G4_URANIUM_MONOCARBIDE
  specific = 4
FEATURE [App::DocumentObjectGroupPython] U_element019  label="U_element : 018"  # scripted group (container) (typed FeaturePython)
  n = 1
  ref = U_element
FEATURE [App::DocumentObjectGroupPython] O_element620  label="O_element : 393"  # scripted group (container) (typed FeaturePython)
  n = 2
  ref = O_element
FEATURE [App::DocumentObjectGroupPython] G4_URANIUM_OXIDE  # scripted group (container) (typed FeaturePython)
  Dunit = g/cm3
  Dvalue = 10.96
  Group = -> [U_element019,O_element620]
  conduct = 2
  density = 1
  expand = 3
  formula = G4_URANIUM_OXIDE
  name = G4_URANIUM_OXIDE
  specific = 4
FEATURE [App::DocumentObjectGroupPython] C_element711  label="C_element : 466"  # scripted group (container) (typed FeaturePython)
  n = 1
  ref = C_element
FEATURE [App::DocumentObjectGroupPython] H_element659  label="H_element : 425"  # scripted group (container) (typed FeaturePython)
  n = 4
  ref = H_element
FEATURE [App::DocumentObjectGroupPython] N_element318  label="N_element : 170"  # scripted group (container) (typed FeaturePython)
  n = 2
  ref = N_element
FEATURE [App::DocumentObjectGroupPython] O_element621  label="O_element : 394"  # scripted group (container) (typed FeaturePython)
  n = 1
  ref = O_element
FEATURE [App::DocumentObjectGroupPython] G4_UREA  # scripted group (container) (typed FeaturePython)
  Dunit = g/cm3
  Dvalue = 1.323
  Group = -> [C_element711,H_element659,N_element318,O_element621]
  conduct = 2
  density = 1
  expand = 3
  formula = G4_UREA
  name = G4_UREA
  specific = 4
FEATURE [App::DocumentObjectGroupPython] C_element712  label="C_element : 467"  # scripted group (container) (typed FeaturePython)
  n = 5
  ref = C_element
FEATURE [App::DocumentObjectGroupPython] H_element660  label="H_element : 426"  # scripted group (container) (typed FeaturePython)
  n = 11
  ref = H_element
FEATURE [App::DocumentObjectGroupPython] N_element319  label="N_element : 171"  # scripted group (container) (typed FeaturePython)
  n = 1
  ref = N_element
FEATURE [App::DocumentObjectGroupPython] O_element622  label="O_element : 395"  # scripted group (container) (typed FeaturePython)
  n = 2
  ref = O_element
FEATURE [App::DocumentObjectGroupPython] G4_VALINE  # scripted group (container) (typed FeaturePython)
  Dunit = g/cm3
  Dvalue = 1.23
  Group = -> [C_element712,H_element660,N_element319,O_element622]
  conduct = 2
  density = 1
  expand = 3
  formula = G4_VALINE
  name = G4_VALINE
  specific = 4
FEATURE [App::DocumentObjectGroupPython] H_element661  label="H_element : 0.285"  # scripted group (container) (typed FeaturePython)
  n = 0.009417
FEATURE [App::DocumentObjectGroupPython] C_element713  label="C_element : 0.1016"  # scripted group (container) (typed FeaturePython)
  n = 0.280555
FEATURE [App::DocumentObjectGroupPython] F_element094  label="F_element : 0.734"  # scripted group (container) (typed FeaturePython)
  n = 0.710028
FEATURE [App::DocumentObjectGroupPython] G4_VITON  # scripted group (container) (typed FeaturePython)
  Dunit = g/cm3
  Dvalue = 1.8
  Group = -> [H_element661,C_element713,F_element094]
  conduct = 2
  density = 1
  expand = 3
  formula = G4_VITON
  name = G4_VITON
  specific = 4
FEATURE [App::DocumentObjectGroupPython] H_element662  label="H_element : 427"  # scripted group (container) (typed FeaturePython)
  n = 2
  ref = H_element
FEATURE [App::DocumentObjectGroupPython] O_element623  label="O_element : 396"  # scripted group (container) (typed FeaturePython)
  n = 1
  ref = O_element
FEATURE [App::DocumentObjectGroupPython] G4_WATER  # scripted group (container) (typed FeaturePython)
  Dunit = g/cm3
  Dvalue = 1
  Group = -> [H_element662,O_element623]
  conduct = 2
  density = 1
  expand = 3
  formula = G4_WATER
  name = G4_WATER
  specific = 4
FEATURE [App::DocumentObjectGroupPython] H_element663  label="H_element : 428"  # scripted group (container) (typed FeaturePython)
  n = 2
  ref = H_element
FEATURE [App::DocumentObjectGroupPython] O_element624  label="O_element : 397"  # scripted group (container) (typed FeaturePython)
  n = 1
  ref = O_element
FEATURE [App::DocumentObjectGroupPython] G4_WATER_VAPOR  # scripted group (container) (typed FeaturePython)
  Dunit = g/cm3
  Dvalue = 0.000756182
  Group = -> [H_element663,O_element624]
  conduct = 2
  density = 1
  expand = 3
  formula = G4_WATER_VAPOR
  name = G4_WATER_VAPOR
  specific = 4
FEATURE [App::DocumentObjectGroupPython] C_element714  label="C_element : 468"  # scripted group (container) (typed FeaturePython)
  n = 8
  ref = C_element
FEATURE [App::DocumentObjectGroupPython] H_element664  label="H_element : 429"  # scripted group (container) (typed FeaturePython)
  n = 10
  ref = H_element
FEATURE [App::DocumentObjectGroupPython] G4_XYLENE  # scripted group (container) (typed FeaturePython)
  Dunit = g/cm3
  Dvalue = 0.87
  Group = -> [C_element714,H_element664]
  conduct = 2
  density = 1
  expand = 3
  formula = G4_XYLENE
  name = G4_XYLENE
  specific = 4
FEATURE [App::DocumentObjectGroupPython] C_element715  label="C_element : 469"  # scripted group (container) (typed FeaturePython)
  n = 1
  ref = C_element
FEATURE [App::DocumentObjectGroupPython] G4_GRAPHITE  # scripted group (container) (typed FeaturePython)
  Dunit = g/cm3
  Dvalue = 2.21
  Group = -> [C_element715]
  conduct = 2
  density = 1
  expand = 3
  formula = G4_GRAPHITE
  name = G4_GRAPHITE
  specific = 4
FEATURE [App::DocumentObjectGroupPython] NIST  # scripted group (container) (typed FeaturePython)
  Group = -> [G4_A_150_TISSUE,G4_ACETONE,G4_ACETYLENE,G4_ADENINE,G4_ADIPOSE_TISSUE_ICRP,G4_AIR,G4_ALANINE,G4_ALUMINUM_OXIDE,G4_AMBER,G4_AMMONIA,G4_ANILINE,G4_ANTHRACENE,G4_B_100_BONE,G4_BAKELITE,G4_BARIUM_FLUORIDE,G4_BARIUM_SULFATE,G4_BENZENE,G4_BERYLLIUM_OXIDE,G4_BGO,G4_BLOOD_ICRP,G4_BONE_COMPACT_ICRU,G4_BONE_CORTICAL_ICRP,G4_BORON_CARBIDE,G4_BORON_OXIDE,G4_BRAIN_ICRP,G4_BUTANE,G4_N_BUTYL_ALCOHOL,G4_C_552,+152 more]
FEATURE [App::DocumentObjectGroupPython] H_element665  label="H_element : 430"  # scripted group (container) (typed FeaturePython)
  n = 1
  ref = H_element
FEATURE [App::DocumentObjectGroupPython] G4_H  # scripted group (container) (typed FeaturePython)
  Dunit = g/cm3
  Dvalue = 8.3748e-05
  Group = -> [H_element665]
  conduct = 2
  density = 1
  expand = 3
  formula = H
  name = G4_H
  specific = 4
FEATURE [App::DocumentObjectGroupPython] He_element005  label="He_element : 004"  # scripted group (container) (typed FeaturePython)
  n = 1
  ref = He_element
FEATURE [App::DocumentObjectGroupPython] G4_He  # scripted group (container) (typed FeaturePython)
  Dunit = g/cm3
  Dvalue = 0.000166322
  Group = -> [He_element005]
  conduct = 2
  density = 1
  expand = 3
  formula = He
  name = G4_He
  specific = 4
FEATURE [App::DocumentObjectGroupPython] Li_element040  label="Li_element : 038"  # scripted group (container) (typed FeaturePython)
  n = 1
  ref = Li_element
FEATURE [App::DocumentObjectGroupPython] G4_Li  # scripted group (container) (typed FeaturePython)
  Dunit = g/cm3
  Dvalue = 0.534
  Group = -> [Li_element040]
  conduct = 2
  density = 1
  expand = 3
  formula = Li
  name = G4_Li
  specific = 4
FEATURE [App::DocumentObjectGroupPython] Be_element010  label="Be_element : 009"  # scripted group (container) (typed FeaturePython)
  n = 1
  ref = Be_element
FEATURE [App::DocumentObjectGroupPython] G4_Be  # scripted group (container) (typed FeaturePython)
  Dunit = g/cm3
  Dvalue = 1.848
  Group = -> [Be_element010]
  conduct = 2
  density = 1
  expand = 3
  formula = Be
  name = G4_Be
  specific = 4
FEATURE [App::DocumentObjectGroupPython] B_element035  label="B_element : 028"  # scripted group (container) (typed FeaturePython)
  n = 1
  ref = B_element
FEATURE [App::DocumentObjectGroupPython] G4_B  # scripted group (container) (typed FeaturePython)
  Dunit = g/cm3
  Dvalue = 2.37
  Group = -> [B_element035]
  conduct = 2
  density = 1
  expand = 3
  formula = B
  name = G4_B
  specific = 4
FEATURE [App::DocumentObjectGroupPython] C_element716  label="C_element : 470"  # scripted group (container) (typed FeaturePython)
  n = 1
  ref = C_element
FEATURE [App::DocumentObjectGroupPython] G4_C  # scripted group (container) (typed FeaturePython)
  Dunit = g/cm3
  Dvalue = 2
  Group = -> [C_element716]
  conduct = 2
  density = 1
  expand = 3
  formula = C
  name = G4_C
  specific = 4
FEATURE [App::DocumentObjectGroupPython] N_element320  label="N_element : 172"  # scripted group (container) (typed FeaturePython)
  n = 1
  ref = N_element
FEATURE [App::DocumentObjectGroupPython] G4_N  # scripted group (container) (typed FeaturePython)
  Dunit = g/cm3
  Dvalue = 0.0011652
  Group = -> [N_element320]
  conduct = 2
  density = 1
  expand = 3
  formula = N
  name = G4_N
  specific = 4
FEATURE [App::DocumentObjectGroupPython] O_element625  label="O_element : 398"  # scripted group (container) (typed FeaturePython)
  n = 1
  ref = O_element
FEATURE [App::DocumentObjectGroupPython] G4_O  # scripted group (container) (typed FeaturePython)
  Dunit = g/cm3
  Dvalue = 0.00133151
  Group = -> [O_element625]
  conduct = 2
  density = 1
  expand = 3
  formula = O
  name = G4_O
  specific = 4
FEATURE [App::DocumentObjectGroupPython] F_element095  label="F_element : 047"  # scripted group (container) (typed FeaturePython)
  n = 1
  ref = F_element
FEATURE [App::DocumentObjectGroupPython] G4_F  # scripted group (container) (typed FeaturePython)
  Dunit = g/cm3
  Dvalue = 0.00158029
  Group = -> [F_element095]
  conduct = 2
  density = 1
  expand = 3
  formula = F
  name = G4_F
  specific = 4
FEATURE [App::DocumentObjectGroupPython] Ne_element005  label="Ne_element : 004"  # scripted group (container) (typed FeaturePython)
  n = 1
  ref = Ne_element
FEATURE [App::DocumentObjectGroupPython] G4_Ne  # scripted group (container) (typed FeaturePython)
  Dunit = g/cm3
  Dvalue = 0.000838505
  Group = -> [Ne_element005]
  conduct = 2
  density = 1
  expand = 3
  formula = Ne
  name = G4_Ne
  specific = 4
FEATURE [App::DocumentObjectGroupPython] Na_element100  label="Na_element : 023"  # scripted group (container) (typed FeaturePython)
  n = 1
  ref = Na_element
FEATURE [App::DocumentObjectGroupPython] G4_Na  # scripted group (container) (typed FeaturePython)
  Dunit = g/cm3
  Dvalue = 0.971
  Group = -> [Na_element100]
  conduct = 2
  density = 1
  expand = 3
  formula = Na
  name = G4_Na
  specific = 4
FEATURE [App::DocumentObjectGroupPython] Mg_element055  label="Mg_element : 024"  # scripted group (container) (typed FeaturePython)
  n = 1
  ref = Mg_element
FEATURE [App::DocumentObjectGroupPython] G4_Mg  # scripted group (container) (typed FeaturePython)
  Dunit = g/cm3
  Dvalue = 1.74
  Group = -> [Mg_element055]
  conduct = 2
  density = 1
  expand = 3
  formula = Mg
  name = G4_Mg
  specific = 4
FEATURE [App::DocumentObjectGroupPython] Al_element020  label="Al_element : 008"  # scripted group (container) (typed FeaturePython)
  n = 1
  ref = Al_element
FEATURE [App::DocumentObjectGroupPython] G4_Al  # scripted group (container) (typed FeaturePython)
  Dunit = g/cm3
  Dvalue = 2.699
  Group = -> [Al_element020]
  conduct = 2
  density = 1
  expand = 3
  formula = Al
  name = G4_Al
  specific = 4
FEATURE [App::DocumentObjectGroupPython] Si_element035  label="Si_element : 009"  # scripted group (container) (typed FeaturePython)
  n = 1
  ref = Si_element
FEATURE [App::DocumentObjectGroupPython] G4_Si  # scripted group (container) (typed FeaturePython)
  Dunit = g/cm3
  Dvalue = 2.33
  Group = -> [Si_element035]
  conduct = 2
  density = 1
  expand = 3
  formula = Si
  name = G4_Si
  specific = 4
FEATURE [App::DocumentObjectGroupPython] P_element089  label="P_element : 033"  # scripted group (container) (typed FeaturePython)
  n = 1
  ref = P_element
FEATURE [App::DocumentObjectGroupPython] G4_P  # scripted group (container) (typed FeaturePython)
  Dunit = g/cm3
  Dvalue = 2.2
  Group = -> [P_element089]
  conduct = 2
  density = 1
  expand = 3
  formula = P
  name = G4_P
  specific = 4
FEATURE [App::DocumentObjectGroupPython] S_element115  label="S_element : 034"  # scripted group (container) (typed FeaturePython)
  n = 1
  ref = S_element
FEATURE [App::DocumentObjectGroupPython] G4_S  # scripted group (container) (typed FeaturePython)
  Dunit = g/cm3
  Dvalue = 2
  Group = -> [S_element115]
  conduct = 2
  density = 1
  expand = 3
  formula = S
  name = G4_S
  specific = 4
FEATURE [App::DocumentObjectGroupPython] Cl_element149  label="Cl_element : 075"  # scripted group (container) (typed FeaturePython)
  n = 1
  ref = Cl_element
FEATURE [App::DocumentObjectGroupPython] G4_Cl  # scripted group (container) (typed FeaturePython)
  Dunit = g/cm3
  Dvalue = 0.00299473
  Group = -> [Cl_element149]
  conduct = 2
  density = 1
  expand = 3
  formula = Cl
  name = G4_Cl
  specific = 4
FEATURE [App::DocumentObjectGroupPython] Ar_element010  label="Ar_element : 004"  # scripted group (container) (typed FeaturePython)
  n = 1
  ref = Ar_element
FEATURE [App::DocumentObjectGroupPython] G4_Ar  # scripted group (container) (typed FeaturePython)
  Dunit = g/cm3
  Dvalue = 0.00166201
  Group = -> [Ar_element010]
  conduct = 2
  density = 1
  expand = 3
  formula = Ar
  name = G4_Ar
  specific = 4
FEATURE [App::DocumentObjectGroupPython] K_element065  label="K_element : 013"  # scripted group (container) (typed FeaturePython)
  n = 1
  ref = K_element
FEATURE [App::DocumentObjectGroupPython] G4_K  # scripted group (container) (typed FeaturePython)
  Dunit = g/cm3
  Dvalue = 0.862
  Group = -> [K_element065]
  conduct = 2
  density = 1
  expand = 3
  formula = K
  name = G4_K
  specific = 4
FEATURE [App::DocumentObjectGroupPython] Ca_element070  label="Ca_element : 034"  # scripted group (container) (typed FeaturePython)
  n = 1
  ref = Ca_element
FEATURE [App::DocumentObjectGroupPython] G4_Ca  # scripted group (container) (typed FeaturePython)
  Dunit = g/cm3
  Dvalue = 1.55
  Group = -> [Ca_element070]
  conduct = 2
  density = 1
  expand = 3
  formula = Ca
  name = G4_Ca
  specific = 4
FEATURE [App::DocumentObjectGroupPython] Sc_element005  label="Sc_element : 004"  # scripted group (container) (typed FeaturePython)
  n = 1
  ref = Sc_element
FEATURE [App::DocumentObjectGroupPython] G4_Sc  # scripted group (container) (typed FeaturePython)
  Dunit = g/cm3
  Dvalue = 2.989
  Group = -> [Sc_element005]
  conduct = 2
  density = 1
  expand = 3
  formula = Sc
  name = G4_Sc
  specific = 4
FEATURE [App::DocumentObjectGroupPython] Ti_element020  label="Ti_element : 009"  # scripted group (container) (typed FeaturePython)
  n = 1
  ref = Ti_element
FEATURE [App::DocumentObjectGroupPython] G4_Ti  # scripted group (container) (typed FeaturePython)
  Dunit = g/cm3
  Dvalue = 4.54
  Group = -> [Ti_element020]
  conduct = 2
  density = 1
  expand = 3
  formula = Ti
  name = G4_Ti
  specific = 4
FEATURE [App::DocumentObjectGroupPython] V_element005  label="V_element : 004"  # scripted group (container) (typed FeaturePython)
  n = 1
  ref = V_element
FEATURE [App::DocumentObjectGroupPython] G4_V  # scripted group (container) (typed FeaturePython)
  Dunit = g/cm3
  Dvalue = 6.11
  Group = -> [V_element005]
  conduct = 2
  density = 1
  expand = 3
  formula = V
  name = G4_V
  specific = 4
FEATURE [App::DocumentObjectGroupPython] Cr_element009  label="Cr_element : 023"  # scripted group (container) (typed FeaturePython)
  n = 1
  ref = Cr_element
FEATURE [App::DocumentObjectGroupPython] G4_Cr  # scripted group (container) (typed FeaturePython)
  Dunit = g/cm3
  Dvalue = 7.18
  Group = -> [Cr_element009]
  conduct = 2
  density = 1
  expand = 3
  formula = Cr
  name = G4_Cr
  specific = 4
FEATURE [App::DocumentObjectGroupPython] Mn_element005  label="Mn_element : 004"  # scripted group (container) (typed FeaturePython)
  n = 1
  ref = Mn_element
FEATURE [App::DocumentObjectGroupPython] G4_Mn  # scripted group (container) (typed FeaturePython)
  Dunit = g/cm3
  Dvalue = 7.44
  Group = -> [Mn_element005]
  conduct = 2
  density = 1
  expand = 3
  formula = Mn
  name = G4_Mn
  specific = 4
FEATURE [App::DocumentObjectGroupPython] Fe_element039  label="Fe_element : 020"  # scripted group (container) (typed FeaturePython)
  n = 1
  ref = Fe_element
FEATURE [App::DocumentObjectGroupPython] G4_Fe  # scripted group (container) (typed FeaturePython)
  Dunit = g/cm3
  Dvalue = 7.874
  Group = -> [Fe_element039]
  conduct = 2
  density = 1
  expand = 3
  formula = Fe
  name = G4_Fe
  specific = 4
FEATURE [App::DocumentObjectGroupPython] Co_element005  label="Co_element : 004"  # scripted group (container) (typed FeaturePython)
  n = 1
  ref = Co_element
FEATURE [App::DocumentObjectGroupPython] G4_Co  # scripted group (container) (typed FeaturePython)
  Dunit = g/cm3
  Dvalue = 8.9
  Group = -> [Co_element005]
  conduct = 2
  density = 1
  expand = 3
  formula = Co
  name = G4_Co
  specific = 4
FEATURE [App::DocumentObjectGroupPython] Ni_element009  label="Ni_element : 013"  # scripted group (container) (typed FeaturePython)
  n = 1
  ref = Ni_element
FEATURE [App::DocumentObjectGroupPython] G4_Ni  # scripted group (container) (typed FeaturePython)
  Dunit = g/cm3
  Dvalue = 8.902
  Group = -> [Ni_element009]
  conduct = 2
  density = 1
  expand = 3
  formula = Ni
  name = G4_Ni
  specific = 4
FEATURE [App::DocumentObjectGroupPython] Cu_element013  label="Cu_element : 096"  # scripted group (container) (typed FeaturePython)
  n = 1
  ref = Cu_element
FEATURE [App::DocumentObjectGroupPython] G4_Cu  # scripted group (container) (typed FeaturePython)
  Dunit = g/cm3
  Dvalue = 8.96
  Group = -> [Cu_element013]
  conduct = 2
  density = 1
  expand = 3
  formula = Cu
  name = G4_Cu
  specific = 4
FEATURE [App::DocumentObjectGroupPython] Zn_element013  label="Zn_element : 042"  # scripted group (container) (typed FeaturePython)
  n = 1
  ref = Zn_element
FEATURE [App::DocumentObjectGroupPython] G4_Zn  # scripted group (container) (typed FeaturePython)
  Dunit = g/cm3
  Dvalue = 7.133
  Group = -> [Zn_element013]
  conduct = 2
  density = 1
  expand = 3
  formula = Zn
  name = G4_Zn
  specific = 4
FEATURE [App::DocumentObjectGroupPython] Ga_element010  label="Ga_element : 009"  # scripted group (container) (typed FeaturePython)
  n = 1
  ref = Ga_element
FEATURE [App::DocumentObjectGroupPython] G4_Ga  # scripted group (container) (typed FeaturePython)
  Dunit = g/cm3
  Dvalue = 5.904
  Group = -> [Ga_element010]
  conduct = 2
  density = 1
  expand = 3
  formula = Ga
  name = G4_Ga
  specific = 4
FEATURE [App::DocumentObjectGroupPython] Ge_element010  label="Ge_element : 009"  # scripted group (container) (typed FeaturePython)
  n = 1
  ref = Ge_element
FEATURE [App::DocumentObjectGroupPython] G4_Ge  # scripted group (container) (typed FeaturePython)
  Dunit = g/cm3
  Dvalue = 5.323
  Group = -> [Ge_element010]
  conduct = 2
  density = 1
  expand = 3
  formula = Ge
  name = G4_Ge
  specific = 4
FEATURE [App::DocumentObjectGroupPython] As_element015  label="As_element : 009"  # scripted group (container) (typed FeaturePython)
  n = 1
  ref = As_element
FEATURE [App::DocumentObjectGroupPython] G4_As  # scripted group (container) (typed FeaturePython)
  Dunit = g/cm3
  Dvalue = 5.73
  Group = -> [As_element015]
  conduct = 2
  density = 1
  expand = 3
  formula = As
  name = G4_As
  specific = 4
FEATURE [App::DocumentObjectGroupPython] Se_element005  label="Se_element : 004"  # scripted group (container) (typed FeaturePython)
  n = 1
  ref = Se_element
FEATURE [App::DocumentObjectGroupPython] G4_Se  # scripted group (container) (typed FeaturePython)
  Dunit = g/cm3
  Dvalue = 4.5
  Group = -> [Se_element005]
  conduct = 2
  density = 1
  expand = 3
  formula = Se
  name = G4_Se
  specific = 4
FEATURE [App::DocumentObjectGroupPython] Br_element035  label="Br_element : 019"  # scripted group (container) (typed FeaturePython)
  n = 1
  ref = Br_element
FEATURE [App::DocumentObjectGroupPython] G4_Br  # scripted group (container) (typed FeaturePython)
  Dunit = g/cm3
  Dvalue = 0.0070721
  Group = -> [Br_element035]
  conduct = 2
  density = 1
  expand = 3
  formula = Br
  name = G4_Br
  specific = 4
FEATURE [App::DocumentObjectGroupPython] Kr_element005  label="Kr_element : 004"  # scripted group (container) (typed FeaturePython)
  n = 1
  ref = Kr_element
FEATURE [App::DocumentObjectGroupPython] G4_Kr  # scripted group (container) (typed FeaturePython)
  Dunit = g/cm3
  Dvalue = 0.00347832
  Group = -> [Kr_element005]
  conduct = 2
  density = 1
  expand = 3
  formula = Kr
  name = G4_Kr
  specific = 4
FEATURE [App::DocumentObjectGroupPython] Rb_element005  label="Rb_element : 004"  # scripted group (container) (typed FeaturePython)
  n = 1
  ref = Rb_element
FEATURE [App::DocumentObjectGroupPython] G4_Rb  # scripted group (container) (typed FeaturePython)
  Dunit = g/cm3
  Dvalue = 1.532
  Group = -> [Rb_element005]
  conduct = 2
  density = 1
  expand = 3
  formula = Rb
  name = G4_Rb
  specific = 4
FEATURE [App::DocumentObjectGroupPython] Sr_element005  label="Sr_element : 004"  # scripted group (container) (typed FeaturePython)
  n = 1
  ref = Sr_element
FEATURE [App::DocumentObjectGroupPython] G4_Sr  # scripted group (container) (typed FeaturePython)
  Dunit = g/cm3
  Dvalue = 2.54
  Group = -> [Sr_element005]
  conduct = 2
  density = 1
  expand = 3
  formula = Sr
  name = G4_Sr
  specific = 4
FEATURE [App::DocumentObjectGroupPython] Y_element005  label="Y_element : 004"  # scripted group (container) (typed FeaturePython)
  n = 1
  ref = Y_element
FEATURE [App::DocumentObjectGroupPython] G4_Y  # scripted group (container) (typed FeaturePython)
  Dunit = g/cm3
  Dvalue = 4.469
  Group = -> [Y_element005]
  conduct = 2
  density = 1
  expand = 3
  formula = Y
  name = G4_Y
  specific = 4
FEATURE [App::DocumentObjectGroupPython] Zr_element005  label="Zr_element : 004"  # scripted group (container) (typed FeaturePython)
  n = 1
  ref = Zr_element
FEATURE [App::DocumentObjectGroupPython] G4_Zr  # scripted group (container) (typed FeaturePython)
  Dunit = g/cm3
  Dvalue = 6.506
  Group = -> [Zr_element005]
  conduct = 2
  density = 1
  expand = 3
  formula = Zr
  name = G4_Zr
  specific = 4
FEATURE [App::DocumentObjectGroupPython] Nb_element005  label="Nb_element : 004"  # scripted group (container) (typed FeaturePython)
  n = 1
  ref = Nb_element
FEATURE [App::DocumentObjectGroupPython] G4_Nb  # scripted group (container) (typed FeaturePython)
  Dunit = g/cm3
  Dvalue = 8.57
  Group = -> [Nb_element005]
  conduct = 2
  density = 1
  expand = 3
  formula = Nb
  name = G4_Nb
  specific = 4
FEATURE [App::DocumentObjectGroupPython] Mo_element005  label="Mo_element : 004"  # scripted group (container) (typed FeaturePython)
  n = 1
  ref = Mo_element
FEATURE [App::DocumentObjectGroupPython] G4_Mo  # scripted group (container) (typed FeaturePython)
  Dunit = g/cm3
  Dvalue = 10.22
  Group = -> [Mo_element005]
  conduct = 2
  density = 1
  expand = 3
  formula = Mo
  name = G4_Mo
  specific = 4
FEATURE [App::DocumentObjectGroupPython] Tc_element005  label="Tc_element : 004"  # scripted group (container) (typed FeaturePython)
  n = 1
  ref = Tc_element
FEATURE [App::DocumentObjectGroupPython] G4_Tc  # scripted group (container) (typed FeaturePython)
  Dunit = g/cm3
  Dvalue = 11.5
  Group = -> [Tc_element005]
  conduct = 2
  density = 1
  expand = 3
  formula = Tc
  name = G4_Tc
  specific = 4
FEATURE [App::DocumentObjectGroupPython] Ru_element005  label="Ru_element : 004"  # scripted group (container) (typed FeaturePython)
  n = 1
  ref = Ru_element
FEATURE [App::DocumentObjectGroupPython] G4_Ru  # scripted group (container) (typed FeaturePython)
  Dunit = g/cm3
  Dvalue = 12.41
  Group = -> [Ru_element005]
  conduct = 2
  density = 1
  expand = 3
  formula = Ru
  name = G4_Ru
  specific = 4
FEATURE [App::DocumentObjectGroupPython] Rh_element005  label="Rh_element : 004"  # scripted group (container) (typed FeaturePython)
  n = 1
  ref = Rh_element
FEATURE [App::DocumentObjectGroupPython] G4_Rh  # scripted group (container) (typed FeaturePython)
  Dunit = g/cm3
  Dvalue = 12.41
  Group = -> [Rh_element005]
  conduct = 2
  density = 1
  expand = 3
  formula = Rh
  name = G4_Rh
  specific = 4
FEATURE [App::DocumentObjectGroupPython] Pd_element005  label="Pd_element : 004"  # scripted group (container) (typed FeaturePython)
  n = 1
  ref = Pd_element
FEATURE [App::DocumentObjectGroupPython] G4_Pd  # scripted group (container) (typed FeaturePython)
  Dunit = g/cm3
  Dvalue = 12.02
  Group = -> [Pd_element005]
  conduct = 2
  density = 1
  expand = 3
  formula = Pd
  name = G4_Pd
  specific = 4
FEATURE [App::DocumentObjectGroupPython] Ag_element030  label="Ag_element : 019"  # scripted group (container) (typed FeaturePython)
  n = 1
  ref = Ag_element
FEATURE [App::DocumentObjectGroupPython] G4_Ag  # scripted group (container) (typed FeaturePython)
  Dunit = g/cm3
  Dvalue = 10.5
  Group = -> [Ag_element030]
  conduct = 2
  density = 1
  expand = 3
  formula = Ag
  name = G4_Ag
  specific = 4
FEATURE [App::DocumentObjectGroupPython] Cd_element015  label="Cd_element : 014"  # scripted group (container) (typed FeaturePython)
  n = 1
  ref = Cd_element
FEATURE [App::DocumentObjectGroupPython] G4_Cd  # scripted group (container) (typed FeaturePython)
  Dunit = g/cm3
  Dvalue = 8.65
  Group = -> [Cd_element015]
  conduct = 2
  density = 1
  expand = 3
  formula = Cd
  name = G4_Cd
  specific = 4
FEATURE [App::DocumentObjectGroupPython] In_element005  label="In_element : 004"  # scripted group (container) (typed FeaturePython)
  n = 1
  ref = In_element
FEATURE [App::DocumentObjectGroupPython] G4_In  # scripted group (container) (typed FeaturePython)
  Dunit = g/cm3
  Dvalue = 7.31
  Group = -> [In_element005]
  conduct = 2
  density = 1
  expand = 3
  formula = In
  name = G4_In
  specific = 4
FEATURE [App::DocumentObjectGroupPython] Sn_element005  label="Sn_element : 004"  # scripted group (container) (typed FeaturePython)
  n = 1
  ref = Sn_element
FEATURE [App::DocumentObjectGroupPython] G4_Sn  # scripted group (container) (typed FeaturePython)
  Dunit = g/cm3
  Dvalue = 7.31
  Group = -> [Sn_element005]
  conduct = 2
  density = 1
  expand = 3
  formula = Sn
  name = G4_Sn
  specific = 4
FEATURE [App::DocumentObjectGroupPython] Sb_element005  label="Sb_element : 004"  # scripted group (container) (typed FeaturePython)
  n = 1
  ref = Sb_element
FEATURE [App::DocumentObjectGroupPython] G4_Sb  # scripted group (container) (typed FeaturePython)
  Dunit = g/cm3
  Dvalue = 6.691
  Group = -> [Sb_element005]
  conduct = 2
  density = 1
  expand = 3
  formula = Sb
  name = G4_Sb
  specific = 4
FEATURE [App::DocumentObjectGroupPython] Te_element010  label="Te_element : 009"  # scripted group (container) (typed FeaturePython)
  n = 1
  ref = Te_element
FEATURE [App::DocumentObjectGroupPython] G4_Te  # scripted group (container) (typed FeaturePython)
  Dunit = g/cm3
  Dvalue = 6.24
  Group = -> [Te_element010]
  conduct = 2
  density = 1
  expand = 3
  formula = Te
  name = G4_Te
  specific = 4
FEATURE [App::DocumentObjectGroupPython] I_element050  label="I_element : 032"  # scripted group (container) (typed FeaturePython)
  n = 1
  ref = I_element
FEATURE [App::DocumentObjectGroupPython] G4_I  # scripted group (container) (typed FeaturePython)
  Dunit = g/cm3
  Dvalue = 4.93
  Group = -> [I_element050]
  conduct = 2
  density = 1
  expand = 3
  formula = I
  name = G4_I
  specific = 4
FEATURE [App::DocumentObjectGroupPython] Xe_element005  label="Xe_element : 004"  # scripted group (container) (typed FeaturePython)
  n = 1
  ref = Xe_element
FEATURE [App::DocumentObjectGroupPython] G4_Xe  # scripted group (container) (typed FeaturePython)
  Dunit = g/cm3
  Dvalue = 0.00548536
  Group = -> [Xe_element005]
  conduct = 2
  density = 1
  expand = 3
  formula = Xe
  name = G4_Xe
  specific = 4
FEATURE [App::DocumentObjectGroupPython] Cs_element015  label="Cs_element : 014"  # scripted group (container) (typed FeaturePython)
  n = 1
  ref = Cs_element
FEATURE [App::DocumentObjectGroupPython] G4_Cs  # scripted group (container) (typed FeaturePython)
  Dunit = g/cm3
  Dvalue = 1.873
  Group = -> [Cs_element015]
  conduct = 2
  density = 1
  expand = 3
  formula = Cs
  name = G4_Cs
  specific = 4
FEATURE [App::DocumentObjectGroupPython] Ba_element015  label="Ba_element : 014"  # scripted group (container) (typed FeaturePython)
  n = 1
  ref = Ba_element
FEATURE [App::DocumentObjectGroupPython] G4_Ba  # scripted group (container) (typed FeaturePython)
  Dunit = g/cm3
  Dvalue = 3.5
  Group = -> [Ba_element015]
  conduct = 2
  density = 1
  expand = 3
  formula = Ba
  name = G4_Ba
  specific = 4
FEATURE [App::DocumentObjectGroupPython] La_element015  label="La_element : 013"  # scripted group (container) (typed FeaturePython)
  n = 1
  ref = La_element
FEATURE [App::DocumentObjectGroupPython] G4_La  # scripted group (container) (typed FeaturePython)
  Dunit = g/cm3
  Dvalue = 6.154
  Group = -> [La_element015]
  conduct = 2
  density = 1
  expand = 3
  formula = La
  name = G4_La
  specific = 4
FEATURE [App::DocumentObjectGroupPython] Ce_element010  label="Ce_element : 004"  # scripted group (container) (typed FeaturePython)
  n = 1
  ref = Ce_element
FEATURE [App::DocumentObjectGroupPython] G4_Ce  # scripted group (container) (typed FeaturePython)
  Dunit = g/cm3
  Dvalue = 6.657
  Group = -> [Ce_element010]
  conduct = 2
  density = 1
  expand = 3
  formula = Ce
  name = G4_Ce
  specific = 4
FEATURE [App::DocumentObjectGroupPython] Pr_element005  label="Pr_element : 004"  # scripted group (container) (typed FeaturePython)
  n = 1
  ref = Pr_element
FEATURE [App::DocumentObjectGroupPython] G4_Pr  # scripted group (container) (typed FeaturePython)
  Dunit = g/cm3
  Dvalue = 6.71
  Group = -> [Pr_element005]
  conduct = 2
  density = 1
  expand = 3
  formula = Pr
  name = G4_Pr
  specific = 4
FEATURE [App::DocumentObjectGroupPython] Nd_element005  label="Nd_element : 004"  # scripted group (container) (typed FeaturePython)
  n = 1
  ref = Nd_element
FEATURE [App::DocumentObjectGroupPython] G4_Nd  # scripted group (container) (typed FeaturePython)
  Dunit = g/cm3
  Dvalue = 6.9
  Group = -> [Nd_element005]
  conduct = 2
  density = 1
  expand = 3
  formula = Nd
  name = G4_Nd
  specific = 4
FEATURE [App::DocumentObjectGroupPython] Pm_element005  label="Pm_element : 004"  # scripted group (container) (typed FeaturePython)
  n = 1
  ref = Pm_element
FEATURE [App::DocumentObjectGroupPython] G4_Pm  # scripted group (container) (typed FeaturePython)
  Dunit = g/cm3
  Dvalue = 7.22
  Group = -> [Pm_element005]
  conduct = 2
  density = 1
  expand = 3
  formula = Pm
  name = G4_Pm
  specific = 4
FEATURE [App::DocumentObjectGroupPython] Sm_element005  label="Sm_element : 004"  # scripted group (container) (typed FeaturePython)
  n = 1
  ref = Sm_element
FEATURE [App::DocumentObjectGroupPython] G4_Sm  # scripted group (container) (typed FeaturePython)
  Dunit = g/cm3
  Dvalue = 7.46
  Group = -> [Sm_element005]
  conduct = 2
  density = 1
  expand = 3
  formula = Sm
  name = G4_Sm
  specific = 4
FEATURE [App::DocumentObjectGroupPython] Eu_element005  label="Eu_element : 004"  # scripted group (container) (typed FeaturePython)
  n = 1
  ref = Eu_element
FEATURE [App::DocumentObjectGroupPython] G4_Eu  # scripted group (container) (typed FeaturePython)
  Dunit = g/cm3
  Dvalue = 5.243
  Group = -> [Eu_element005]
  conduct = 2
  density = 1
  expand = 3
  formula = Eu
  name = G4_Eu
  specific = 4
FEATURE [App::DocumentObjectGroupPython] Gd_element010  label="Gd_element : 008"  # scripted group (container) (typed FeaturePython)
  n = 1
  ref = Gd_element
FEATURE [App::DocumentObjectGroupPython] G4_Gd  # scripted group (container) (typed FeaturePython)
  Dunit = g/cm3
  Dvalue = 7.9004
  Group = -> [Gd_element010]
  conduct = 2
  density = 1
  expand = 3
  formula = Gd
  name = G4_Gd
  specific = 4
FEATURE [App::DocumentObjectGroupPython] Tb_element005  label="Tb_element : 004"  # scripted group (container) (typed FeaturePython)
  n = 1
  ref = Tb_element
FEATURE [App::DocumentObjectGroupPython] G4_Tb  # scripted group (container) (typed FeaturePython)
  Dunit = g/cm3
  Dvalue = 8.229
  Group = -> [Tb_element005]
  conduct = 2
  density = 1
  expand = 3
  formula = Tb
  name = G4_Tb
  specific = 4
FEATURE [App::DocumentObjectGroupPython] Dy_element005  label="Dy_element : 004"  # scripted group (container) (typed FeaturePython)
  n = 1
  ref = Dy_element
FEATURE [App::DocumentObjectGroupPython] G4_Dy  # scripted group (container) (typed FeaturePython)
  Dunit = g/cm3
  Dvalue = 8.55
  Group = -> [Dy_element005]
  conduct = 2
  density = 1
  expand = 3
  formula = Dy
  name = G4_Dy
  specific = 4
FEATURE [App::DocumentObjectGroupPython] Ho_element005  label="Ho_element : 004"  # scripted group (container) (typed FeaturePython)
  n = 1
  ref = Ho_element
FEATURE [App::DocumentObjectGroupPython] G4_Ho  # scripted group (container) (typed FeaturePython)
  Dunit = g/cm3
  Dvalue = 8.795
  Group = -> [Ho_element005]
  conduct = 2
  density = 1
  expand = 3
  formula = Ho
  name = G4_Ho
  specific = 4
FEATURE [App::DocumentObjectGroupPython] Er_element005  label="Er_element : 004"  # scripted group (container) (typed FeaturePython)
  n = 1
  ref = Er_element
FEATURE [App::DocumentObjectGroupPython] G4_Er  # scripted group (container) (typed FeaturePython)
  Dunit = g/cm3
  Dvalue = 9.066
  Group = -> [Er_element005]
  conduct = 2
  density = 1
  expand = 3
  formula = Er
  name = G4_Er
  specific = 4
FEATURE [App::DocumentObjectGroupPython] Tm_element005  label="Tm_element : 004"  # scripted group (container) (typed FeaturePython)
  n = 1
  ref = Tm_element
FEATURE [App::DocumentObjectGroupPython] G4_Tm  # scripted group (container) (typed FeaturePython)
  Dunit = g/cm3
  Dvalue = 9.321
  Group = -> [Tm_element005]
  conduct = 2
  density = 1
  expand = 3
  formula = Tm
  name = G4_Tm
  specific = 4
FEATURE [App::DocumentObjectGroupPython] Yb_element005  label="Yb_element : 004"  # scripted group (container) (typed FeaturePython)
  n = 1
  ref = Yb_element
FEATURE [App::DocumentObjectGroupPython] G4_Yb  # scripted group (container) (typed FeaturePython)
  Dunit = g/cm3
  Dvalue = 6.73
  Group = -> [Yb_element005]
  conduct = 2
  density = 1
  expand = 3
  formula = Yb
  name = G4_Yb
  specific = 4
FEATURE [App::DocumentObjectGroupPython] Lu_element005  label="Lu_element : 004"  # scripted group (container) (typed FeaturePython)
  n = 1
  ref = Lu_element
FEATURE [App::DocumentObjectGroupPython] G4_Lu  # scripted group (container) (typed FeaturePython)
  Dunit = g/cm3
  Dvalue = 9.84
  Group = -> [Lu_element005]
  conduct = 2
  density = 1
  expand = 3
  formula = Lu
  name = G4_Lu
  specific = 4
FEATURE [App::DocumentObjectGroupPython] Hf_element005  label="Hf_element : 004"  # scripted group (container) (typed FeaturePython)
  n = 1
  ref = Hf_element
FEATURE [App::DocumentObjectGroupPython] G4_Hf  # scripted group (container) (typed FeaturePython)
  Dunit = g/cm3
  Dvalue = 13.31
  Group = -> [Hf_element005]
  conduct = 2
  density = 1
  expand = 3
  formula = Hf
  name = G4_Hf
  specific = 4
FEATURE [App::DocumentObjectGroupPython] Ta_element005  label="Ta_element : 004"  # scripted group (container) (typed FeaturePython)
  n = 1
  ref = Ta_element
FEATURE [App::DocumentObjectGroupPython] G4_Ta  # scripted group (container) (typed FeaturePython)
  Dunit = g/cm3
  Dvalue = 16.654
  Group = -> [Ta_element005]
  conduct = 2
  density = 1
  expand = 3
  formula = Ta
  name = G4_Ta
  specific = 4
FEATURE [App::DocumentObjectGroupPython] W_element024  label="W_element : 023"  # scripted group (container) (typed FeaturePython)
  n = 1
  ref = W_element
FEATURE [App::DocumentObjectGroupPython] G4_W  # scripted group (container) (typed FeaturePython)
  Dunit = g/cm3
  Dvalue = 19.3
  Group = -> [W_element024]
  conduct = 2
  density = 1
  expand = 3
  formula = W
  name = G4_W
  specific = 4
FEATURE [App::DocumentObjectGroupPython] Re_element005  label="Re_element : 004"  # scripted group (container) (typed FeaturePython)
  n = 1
  ref = Re_element
FEATURE [App::DocumentObjectGroupPython] G4_Re  # scripted group (container) (typed FeaturePython)
  Dunit = g/cm3
  Dvalue = 21.02
  Group = -> [Re_element005]
  conduct = 2
  density = 1
  expand = 3
  formula = Re
  name = G4_Re
  specific = 4
FEATURE [App::DocumentObjectGroupPython] Os_element005  label="Os_element : 004"  # scripted group (container) (typed FeaturePython)
  n = 1
  ref = Os_element
FEATURE [App::DocumentObjectGroupPython] G4_Os  # scripted group (container) (typed FeaturePython)
  Dunit = g/cm3
  Dvalue = 22.57
  Group = -> [Os_element005]
  conduct = 2
  density = 1
  expand = 3
  formula = Os
  name = G4_Os
  specific = 4
FEATURE [App::DocumentObjectGroupPython] Ir_element005  label="Ir_element : 004"  # scripted group (container) (typed FeaturePython)
  n = 1
  ref = Ir_element
FEATURE [App::DocumentObjectGroupPython] G4_Ir  # scripted group (container) (typed FeaturePython)
  Dunit = g/cm3
  Dvalue = 22.42
  Group = -> [Ir_element005]
  conduct = 2
  density = 1
  expand = 3
  formula = Ir
  name = G4_Ir
  specific = 4
FEATURE [App::DocumentObjectGroupPython] Pt_element005  label="Pt_element : 004"  # scripted group (container) (typed FeaturePython)
  n = 1
  ref = Pt_element
FEATURE [App::DocumentObjectGroupPython] G4_Pt  # scripted group (container) (typed FeaturePython)
  Dunit = g/cm3
  Dvalue = 21.45
  Group = -> [Pt_element005]
  conduct = 2
  density = 1
  expand = 3
  formula = Pt
  name = G4_Pt
  specific = 4
FEATURE [App::DocumentObjectGroupPython] Au_element005  label="Au_element : 004"  # scripted group (container) (typed FeaturePython)
  n = 1
  ref = Au_element
FEATURE [App::DocumentObjectGroupPython] G4_Au  # scripted group (container) (typed FeaturePython)
  Dunit = g/cm3
  Dvalue = 19.32
  Group = -> [Au_element005]
  conduct = 2
  density = 1
  expand = 3
  formula = Au
  name = G4_Au
  specific = 4
FEATURE [App::DocumentObjectGroupPython] Hg_element010  label="Hg_element : 009"  # scripted group (container) (typed FeaturePython)
  n = 1
  ref = Hg_element
FEATURE [App::DocumentObjectGroupPython] G4_Hg  # scripted group (container) (typed FeaturePython)
  Dunit = g/cm3
  Dvalue = 13.546
  Group = -> [Hg_element010]
  conduct = 2
  density = 1
  expand = 3
  formula = Hg
  name = G4_Hg
  specific = 4
FEATURE [App::DocumentObjectGroupPython] Tl_element010  label="Tl_element : 009"  # scripted group (container) (typed FeaturePython)
  n = 1
  ref = Tl_element
FEATURE [App::DocumentObjectGroupPython] G4_Tl  # scripted group (container) (typed FeaturePython)
  Dunit = g/cm3
  Dvalue = 11.72
  Group = -> [Tl_element010]
  conduct = 2
  density = 1
  expand = 3
  formula = Tl
  name = G4_Tl
  specific = 4
FEATURE [App::DocumentObjectGroupPython] Pb_element027  label="Pb_element : 012"  # scripted group (container) (typed FeaturePython)
  n = 1
  ref = Pb_element
FEATURE [App::DocumentObjectGroupPython] G4_Pb  # scripted group (container) (typed FeaturePython)
  Dunit = g/cm3
  Dvalue = 11.35
  Group = -> [Pb_element027]
  conduct = 2
  density = 1
  expand = 3
  formula = Pb
  name = G4_Pb
  specific = 4
FEATURE [App::DocumentObjectGroupPython] Bi_element010  label="Bi_element : 010"  # scripted group (container) (typed FeaturePython)
  n = 1
  ref = Bi_element
FEATURE [App::DocumentObjectGroupPython] G4_Bi  # scripted group (container) (typed FeaturePython)
  Dunit = g/cm3
  Dvalue = 9.747
  Group = -> [Bi_element010]
  conduct = 2
  density = 1
  expand = 3
  formula = Bi
  name = G4_Bi
  specific = 4
FEATURE [App::DocumentObjectGroupPython] Po_element005  label="Po_element : 004"  # scripted group (container) (typed FeaturePython)
  n = 1
  ref = Po_element
FEATURE [App::DocumentObjectGroupPython] G4_Po  # scripted group (container) (typed FeaturePython)
  Dunit = g/cm3
  Dvalue = 9.32
  Group = -> [Po_element005]
  conduct = 2
  density = 1
  expand = 3
  formula = Po
  name = G4_Po
  specific = 4
FEATURE [App::DocumentObjectGroupPython] At_element005  label="At_element : 004"  # scripted group (container) (typed FeaturePython)
  n = 1
  ref = At_element
FEATURE [App::DocumentObjectGroupPython] G4_At  # scripted group (container) (typed FeaturePython)
  Dunit = g/cm3
  Dvalue = 9.32
  Group = -> [At_element005]
  conduct = 2
  density = 1
  expand = 3
  formula = At
  name = G4_At
  specific = 4
FEATURE [App::DocumentObjectGroupPython] Rn_element005  label="Rn_element : 004"  # scripted group (container) (typed FeaturePython)
  n = 1
  ref = Rn_element
FEATURE [App::DocumentObjectGroupPython] G4_Rn  # scripted group (container) (typed FeaturePython)
  Dunit = g/cm3
  Dvalue = 0.00900662
  Group = -> [Rn_element005]
  conduct = 2
  density = 1
  expand = 3
  formula = Rn
  name = G4_Rn
  specific = 4
FEATURE [App::DocumentObjectGroupPython] Fr_element005  label="Fr_element : 004"  # scripted group (container) (typed FeaturePython)
  n = 1
  ref = Fr_element
FEATURE [App::DocumentObjectGroupPython] G4_Fr  # scripted group (container) (typed FeaturePython)
  Dunit = g/cm3
  Dvalue = 1
  Group = -> [Fr_element005]
  conduct = 2
  density = 1
  expand = 3
  formula = Fr
  name = G4_Fr
  specific = 4
FEATURE [App::DocumentObjectGroupPython] Ra_element005  label="Ra_element : 004"  # scripted group (container) (typed FeaturePython)
  n = 1
  ref = Ra_element
FEATURE [App::DocumentObjectGroupPython] G4_Ra  # scripted group (container) (typed FeaturePython)
  Dunit = g/cm3
  Dvalue = 5
  Group = -> [Ra_element005]
  conduct = 2
  density = 1
  expand = 3
  formula = Ra
  name = G4_Ra
  specific = 4
FEATURE [App::DocumentObjectGroupPython] Ac_element005  label="Ac_element : 004"  # scripted group (container) (typed FeaturePython)
  n = 1
  ref = Ac_element
FEATURE [App::DocumentObjectGroupPython] G4_Ac  # scripted group (container) (typed FeaturePython)
  Dunit = g/cm3
  Dvalue = 10.07
  Group = -> [Ac_element005]
  conduct = 2
  density = 1
  expand = 3
  formula = Ac
  name = G4_Ac
  specific = 4
FEATURE [App::DocumentObjectGroupPython] Th_element005  label="Th_element : 004"  # scripted group (container) (typed FeaturePython)
  n = 1
  ref = Th_element
FEATURE [App::DocumentObjectGroupPython] G4_Th  # scripted group (container) (typed FeaturePython)
  Dunit = g/cm3
  Dvalue = 11.72
  Group = -> [Th_element005]
  conduct = 2
  density = 1
  expand = 3
  formula = Th
  name = G4_Th
  specific = 4
FEATURE [App::DocumentObjectGroupPython] Pa_element005  label="Pa_element : 004"  # scripted group (container) (typed FeaturePython)
  n = 1
  ref = Pa_element
FEATURE [App::DocumentObjectGroupPython] G4_Pa  # scripted group (container) (typed FeaturePython)
  Dunit = g/cm3
  Dvalue = 15.37
  Group = -> [Pa_element005]
  conduct = 2
  density = 1
  expand = 3
  formula = Pa
  name = G4_Pa
  specific = 4
FEATURE [App::DocumentObjectGroupPython] U_element020  label="U_element : 019"  # scripted group (container) (typed FeaturePython)
  n = 1
  ref = U_element
FEATURE [App::DocumentObjectGroupPython] G4_U  # scripted group (container) (typed FeaturePython)
  Dunit = g/cm3
  Dvalue = 18.95
  Group = -> [U_element020]
  conduct = 2
  density = 1
  expand = 3
  formula = U
  name = G4_U
  specific = 4
FEATURE [App::DocumentObjectGroupPython] Np_element005  label="Np_element : 004"  # scripted group (container) (typed FeaturePython)
  n = 1
  ref = Np_element
FEATURE [App::DocumentObjectGroupPython] G4_Np  # scripted group (container) (typed FeaturePython)
  Dunit = g/cm3
  Dvalue = 20.25
  Group = -> [Np_element005]
  conduct = 2
  density = 1
  expand = 3
  formula = Np
  name = G4_Np
  specific = 4
FEATURE [App::DocumentObjectGroupPython] Pu_element010  label="Pu_element : 009"  # scripted group (container) (typed FeaturePython)
  n = 1
  ref = Pu_element
FEATURE [App::DocumentObjectGroupPython] G4_Pu  # scripted group (container) (typed FeaturePython)
  Dunit = g/cm3
  Dvalue = 19.84
  Group = -> [Pu_element010]
  conduct = 2
  density = 1
  expand = 3
  formula = Pu
  name = G4_Pu
  specific = 4
FEATURE [App::DocumentObjectGroupPython] Am_element005  label="Am_element : 004"  # scripted group (container) (typed FeaturePython)
  n = 1
  ref = Am_element
FEATURE [App::DocumentObjectGroupPython] G4_Am  # scripted group (container) (typed FeaturePython)
  Dunit = g/cm3
  Dvalue = 13.67
  Group = -> [Am_element005]
  conduct = 2
  density = 1
  expand = 3
  formula = Am
  name = G4_Am
  specific = 4
FEATURE [App::DocumentObjectGroupPython] Cm_element005  label="Cm_element : 004"  # scripted group (container) (typed FeaturePython)
  n = 1
  ref = Cm_element
FEATURE [App::DocumentObjectGroupPython] G4_Cm  # scripted group (container) (typed FeaturePython)
  Dunit = g/cm3
  Dvalue = 13.51
  Group = -> [Cm_element005]
  conduct = 2
  density = 1
  expand = 3
  formula = Cm
  name = G4_Cm
  specific = 4
FEATURE [App::DocumentObjectGroupPython] Bk_element005  label="Bk_element : 004"  # scripted group (container) (typed FeaturePython)
  n = 1
  ref = Bk_element
FEATURE [App::DocumentObjectGroupPython] G4_Bk  # scripted group (container) (typed FeaturePython)
  Dunit = g/cm3
  Dvalue = 14
  Group = -> [Bk_element005]
  conduct = 2
  density = 1
  expand = 3
  formula = Bk
  name = G4_Bk
  specific = 4
FEATURE [App::DocumentObjectGroupPython] Cf_element005  label="Cf_element : 004"  # scripted group (container) (typed FeaturePython)
  n = 1
  ref = Cf_element
FEATURE [App::DocumentObjectGroupPython] G4_Cf  # scripted group (container) (typed FeaturePython)
  Dunit = g/cm3
  Dvalue = 10
  Group = -> [Cf_element005]
  conduct = 2
  density = 1
  expand = 3
  formula = Cf
  name = G4_Cf
  specific = 4
FEATURE [App::DocumentObjectGroupPython] Element  # scripted group (container) (typed FeaturePython)
  Group = -> [G4_H,G4_He,G4_Li,G4_Be,G4_B,G4_C,G4_N,G4_O,G4_F,G4_Ne,G4_Na,G4_Mg,G4_Al,G4_Si,G4_P,G4_S,G4_Cl,G4_Ar,G4_K,G4_Ca,G4_Sc,G4_Ti,G4_V,G4_Cr,G4_Mn,G4_Fe,G4_Co,G4_Ni,G4_Cu,G4_Zn,G4_Ga,G4_Ge,G4_As,G4_Se,G4_Br,G4_Kr,G4_Rb,G4_Sr,G4_Y,G4_Zr,G4_Nb,G4_Mo,G4_Tc,G4_Ru,G4_Rh,G4_Pd,G4_Ag,G4_Cd,G4_In,G4_Sn,G4_Sb,G4_Te,G4_I,G4_Xe,G4_Cs,G4_Ba,G4_La,G4_Ce,G4_Pr,G4_Nd,G4_Pm,G4_Sm,G4_Eu,G4_Gd,G4_Tb,G4_Dy,G4_Ho,G4_Er,+30 more]
FEATURE [App::DocumentObjectGroupPython] H_element666  label="H_element : 431"  # scripted group (container) (typed FeaturePython)
  n = 2
  ref = H_element
FEATURE [App::DocumentObjectGroupPython] G4_lH2  # scripted group (container) (typed FeaturePython)
  Dunit = g/cm3
  Dvalue = 0.0708
  Group = -> [H_element666]
  conduct = 2
  density = 1
  expand = 3
  formula = G4_lH2
  name = G4_lH2
  specific = 4
FEATURE [App::DocumentObjectGroupPython] N_element321  label="N_element : 173"  # scripted group (container) (typed FeaturePython)
  n = 2
  ref = N_element
FEATURE [App::DocumentObjectGroupPython] G4_lN2  # scripted group (container) (typed FeaturePython)
  Dunit = g/cm3
  Dvalue = 0.807
  Group = -> [N_element321]
  conduct = 2
  density = 1
  expand = 3
  formula = G4_lN2
  name = G4_lN2
  specific = 4
FEATURE [App::DocumentObjectGroupPython] O_element626  label="O_element : 399"  # scripted group (container) (typed FeaturePython)
  n = 2
  ref = O_element
FEATURE [App::DocumentObjectGroupPython] G4_lO2  # scripted group (container) (typed FeaturePython)
  Dunit = g/cm3
  Dvalue = 1.141
  Group = -> [O_element626]
  conduct = 2
  density = 1
  expand = 3
  formula = G4_lO2
  name = G4_lO2
  specific = 4
FEATURE [App::DocumentObjectGroupPython] Ar003  label="Ar : 004"  # scripted group (container) (typed FeaturePython)
  n = 1
  ref = Ar
FEATURE [App::DocumentObjectGroupPython] G4_lAr  # scripted group (container) (typed FeaturePython)
  Dunit = g/cm3
  Dvalue = 1.396
  Group = -> [Ar003]
  conduct = 2
  density = 1
  expand = 3
  formula = G4_lAr
  name = G4_lAr
  specific = 4
FEATURE [App::DocumentObjectGroupPython] Br003  label="Br : 004"  # scripted group (container) (typed FeaturePython)
  n = 1
  ref = Br
FEATURE [App::DocumentObjectGroupPython] G4_lBr  # scripted group (container) (typed FeaturePython)
  Dunit = g/cm3
  Dvalue = 3.1028
  Group = -> [Br003]
  conduct = 2
  density = 1
  expand = 3
  formula = G4_lBr
  name = G4_lBr
  specific = 4
FEATURE [App::DocumentObjectGroupPython] Kr003  label="Kr : 004"  # scripted group (container) (typed FeaturePython)
  n = 1
  ref = Kr
FEATURE [App::DocumentObjectGroupPython] G4_lKr  # scripted group (container) (typed FeaturePython)
  Dunit = g/cm3
  Dvalue = 2.418
  Group = -> [Kr003]
  conduct = 2
  density = 1
  expand = 3
  formula = G4_lKr
  name = G4_lKr
  specific = 4
FEATURE [App::DocumentObjectGroupPython] Xe003  label="Xe : 004"  # scripted group (container) (typed FeaturePython)
  n = 1
  ref = Xe
FEATURE [App::DocumentObjectGroupPython] G4_lXe  # scripted group (container) (typed FeaturePython)
  Dunit = g/cm3
  Dvalue = 2.953
  Group = -> [Xe003]
  conduct = 2
  density = 1
  expand = 3
  formula = G4_lXe
  name = G4_lXe
  specific = 4
FEATURE [App::DocumentObjectGroupPython] O_element627  label="O_element : 400"  # scripted group (container) (typed FeaturePython)
  n = 4
  ref = O_element
FEATURE [App::DocumentObjectGroupPython] Pb_element028  label="Pb_element : 013"  # scripted group (container) (typed FeaturePython)
  n = 1
  ref = Pb_element
FEATURE [App::DocumentObjectGroupPython] W_element025  label="W_element : 024"  # scripted group (container) (typed FeaturePython)
  n = 1
  ref = W_element
FEATURE [App::DocumentObjectGroupPython] G4_PbWO4  # scripted group (container) (typed FeaturePython)
  Dunit = g/cm3
  Dvalue = 8.28
  Group = -> [O_element627,Pb_element028,W_element025]
  conduct = 2
  density = 1
  expand = 3
  formula = G4_PbWO4
  name = G4_PbWO4
  specific = 4
FEATURE [App::DocumentObjectGroupPython] alactic003  label="alactic : 004"  # scripted group (container) (typed FeaturePython)
  n = 1
  ref = alactic
FEATURE [App::DocumentObjectGroupPython] G4_Galactic  # scripted group (container) (typed FeaturePython)
  Dunit = g/cm3
  Dvalue = 0
  Group = -> [alactic003]
  conduct = 2
  density = 1
  expand = 3
  formula = G4_Galactic
  name = G4_Galactic
  specific = 4
FEATURE [App::DocumentObjectGroupPython] RAPHITE_POROUS003  label="RAPHITE_POROUS : 004"  # scripted group (container) (typed FeaturePython)
  n = 1
  ref = RAPHITE_POROUS
FEATURE [App::DocumentObjectGroupPython] G4_GRAPHITE_POROUS  # scripted group (container) (typed FeaturePython)
  Dunit = g/cm3
  Dvalue = 1.7
  Group = -> [RAPHITE_POROUS003]
  conduct = 2
  density = 1
  expand = 3
  formula = G4_GRAPHITE_POROUS
  name = G4_GRAPHITE_POROUS
  specific = 4
FEATURE [App::DocumentObjectGroupPython] H_element667  label="H_element : 0.286"  # scripted group (container) (typed FeaturePython)
  n = 0.080538
FEATURE [App::DocumentObjectGroupPython] C_element717  label="C_element : 0.1017"  # scripted group (container) (typed FeaturePython)
  n = 0.599848
FEATURE [App::DocumentObjectGroupPython] O_element628  label="O_element : 0.1007"  # scripted group (container) (typed FeaturePython)
  n = 0.319614
FEATURE [App::DocumentObjectGroupPython] G4_LUCITE  # scripted group (container) (typed FeaturePython)
  Dunit = g/cm3
  Dvalue = 1.19
  Group = -> [H_element667,C_element717,O_element628]
  conduct = 2
  density = 1
  expand = 3
  formula = G4_LUCITE
  name = G4_LUCITE
  specific = 4
FEATURE [App::DocumentObjectGroupPython] Cu_element014  label="Cu_element : 097"  # scripted group (container) (typed FeaturePython)
  n = 62
  ref = Cu_element
FEATURE [App::DocumentObjectGroupPython] Zn_element014  label="Zn_element : 043"  # scripted group (container) (typed FeaturePython)
  n = 35
  ref = Zn_element
FEATURE [App::DocumentObjectGroupPython] Pb_element029  label="Pb_element : 014"  # scripted group (container) (typed FeaturePython)
  n = 3
  ref = Pb_element
FEATURE [App::DocumentObjectGroupPython] G4_BRASS  # scripted group (container) (typed FeaturePython)
  Dunit = g/cm3
  Dvalue = 8.52
  Group = -> [Cu_element014,Zn_element014,Pb_element029]
  conduct = 2
  density = 1
  expand = 3
  formula = G4_BRASS
  name = G4_BRASS
  specific = 4
FEATURE [App::DocumentObjectGroupPython] Cu_element015  label="Cu_element : 098"  # scripted group (container) (typed FeaturePython)
  n = 89
  ref = Cu_element
FEATURE [App::DocumentObjectGroupPython] Zn_element015  label="Zn_element : 044"  # scripted group (container) (typed FeaturePython)
  n = 9
  ref = Zn_element
FEATURE [App::DocumentObjectGroupPython] Pb_element030  label="Pb_element : 015"  # scripted group (container) (typed FeaturePython)
  n = 2
  ref = Pb_element
FEATURE [App::DocumentObjectGroupPython] G4_BRONZE  # scripted group (container) (typed FeaturePython)
  Dunit = g/cm3
  Dvalue = 8.82
  Group = -> [Cu_element015,Zn_element015,Pb_element030]
  conduct = 2
  density = 1
  expand = 3
  formula = G4_BRONZE
  name = G4_BRONZE
  specific = 4
FEATURE [App::DocumentObjectGroupPython] Fe_element040  label="Fe_element : 021"  # scripted group (container) (typed FeaturePython)
  n = 74
  ref = Fe_element
FEATURE [App::DocumentObjectGroupPython] Cr_element010  label="Cr_element : 024"  # scripted group (container) (typed FeaturePython)
  n = 18
  ref = Cr_element
FEATURE [App::DocumentObjectGroupPython] Ni_element010  label="Ni_element : 014"  # scripted group (container) (typed FeaturePython)
  n = 8
  ref = Ni_element
FEATURE [App::DocumentObjectGroupPython] G4_STAINLESS_STEEL  label="G4_STAINLESS-STEEL"  # scripted group (container) (typed FeaturePython)
  Dunit = g/cm3
  Dvalue = 8
  Group = -> [Fe_element040,Cr_element010,Ni_element010]
  conduct = 2
  density = 1
  expand = 3
  formula = G4_STAINLESS-STEEL
  name = G4_STAINLESS-STEEL
  specific = 4
FEATURE [App::DocumentObjectGroupPython] H_element668  label="H_element : 432"  # scripted group (container) (typed FeaturePython)
  n = 18
  ref = H_element
FEATURE [App::DocumentObjectGroupPython] C_element718  label="C_element : 471"  # scripted group (container) (typed FeaturePython)
  n = 12
  ref = C_element
FEATURE [App::DocumentObjectGroupPython] O_element629  label="O_element : 401"  # scripted group (container) (typed FeaturePython)
  n = 7
  ref = O_element
FEATURE [App::DocumentObjectGroupPython] G4_CR39  # scripted group (container) (typed FeaturePython)
  Dunit = g/cm3
  Dvalue = 1.32
  Group = -> [H_element668,C_element718,O_element629]
  conduct = 2
  density = 1
  expand = 3
  formula = G4_CR39
  name = G4_CR39
  specific = 4
FEATURE [App::DocumentObjectGroupPython] H_element669  label="H_element : 433"  # scripted group (container) (typed FeaturePython)
  n = 38
  ref = H_element
FEATURE [App::DocumentObjectGroupPython] C_element719  label="C_element : 472"  # scripted group (container) (typed FeaturePython)
  n = 18
  ref = C_element
FEATURE [App::DocumentObjectGroupPython] O_element630  label="O_element : 402"  # scripted group (container) (typed FeaturePython)
  n = 1
  ref = O_element
FEATURE [App::DocumentObjectGroupPython] G4_OCTADECANOL  # scripted group (container) (typed FeaturePython)
  Dunit = g/cm3
  Dvalue = 0.812
  Group = -> [H_element669,C_element719,O_element630]
  conduct = 2
  density = 1
  expand = 3
  formula = G4_OCTADECANOL
  name = G4_OCTADECANOL
  specific = 4
FEATURE [App::DocumentObjectGroupPython] HEP  # scripted group (container) (typed FeaturePython)
  Group = -> [G4_lH2,G4_lN2,G4_lO2,G4_lAr,G4_lBr,G4_lKr,G4_lXe,G4_PbWO4,G4_Galactic,G4_GRAPHITE_POROUS,G4_LUCITE,G4_BRASS,G4_BRONZE,G4_STAINLESS_STEEL,G4_CR39,G4_OCTADECANOL]
FEATURE [App::DocumentObjectGroupPython] C_element720  label="C_element : 473"  # scripted group (container) (typed FeaturePython)
  n = 14
  ref = C_element
FEATURE [App::DocumentObjectGroupPython] H_element670  label="H_element : 434"  # scripted group (container) (typed FeaturePython)
  n = 10
  ref = H_element
FEATURE [App::DocumentObjectGroupPython] O_element631  label="O_element : 403"  # scripted group (container) (typed FeaturePython)
  n = 2
  ref = O_element
FEATURE [App::DocumentObjectGroupPython] N_element322  label="N_element : 174"  # scripted group (container) (typed FeaturePython)
  n = 2
  ref = N_element
FEATURE [App::DocumentObjectGroupPython] G4_KEVLAR  # scripted group (container) (typed FeaturePython)
  Dunit = g/cm3
  Dvalue = 1.44
  Group = -> [C_element720,H_element670,O_element631,N_element322]
  conduct = 2
  density = 1
  expand = 3
  formula = G4_KEVLAR
  name = G4_KEVLAR
  specific = 4
FEATURE [App::DocumentObjectGroupPython] C_element721  label="C_element : 474"  # scripted group (container) (typed FeaturePython)
  n = 10
  ref = C_element
FEATURE [App::DocumentObjectGroupPython] H_element671  label="H_element : 435"  # scripted group (container) (typed FeaturePython)
  n = 8
  ref = H_element
FEATURE [App::DocumentObjectGroupPython] O_element632  label="O_element : 404"  # scripted group (container) (typed FeaturePython)
  n = 4
  ref = O_element
FEATURE [App::DocumentObjectGroupPython] G4_DACRON  # scripted group (container) (typed FeaturePython)
  Dunit = g/cm3
  Dvalue = 1.4
  Group = -> [C_element721,H_element671,O_element632]
  conduct = 2
  density = 1
  expand = 3
  formula = G4_DACRON
  name = G4_DACRON
  specific = 4
FEATURE [App::DocumentObjectGroupPython] C_element722  label="C_element : 475"  # scripted group (container) (typed FeaturePython)
  n = 4
  ref = C_element
FEATURE [App::DocumentObjectGroupPython] H_element672  label="H_element : 436"  # scripted group (container) (typed FeaturePython)
  n = 5
  ref = H_element
FEATURE [App::DocumentObjectGroupPython] Cl_element150  label="Cl_element : 076"  # scripted group (container) (typed FeaturePython)
  n = 1
  ref = Cl_element
FEATURE [App::DocumentObjectGroupPython] G4_NEOPRENE  # scripted group (container) (typed FeaturePython)
  Dunit = g/cm3
  Dvalue = 1.23
  Group = -> [C_element722,H_element672,Cl_element150]
  conduct = 2
  density = 1
  expand = 3
  formula = G4_NEOPRENE
  name = G4_NEOPRENE
  specific = 4
FEATURE [App::DocumentObjectGroupPython] Space  # scripted group (container) (typed FeaturePython)
  Group = -> [G4_KEVLAR,G4_DACRON,G4_NEOPRENE]
FEATURE [App::DocumentObjectGroupPython] H_element673  label="H_element : 437"  # scripted group (container) (typed FeaturePython)
  n = 5
  ref = H_element
FEATURE [App::DocumentObjectGroupPython] C_element723  label="C_element : 476"  # scripted group (container) (typed FeaturePython)
  n = 4
  ref = C_element
FEATURE [App::DocumentObjectGroupPython] N_element323  label="N_element : 175"  # scripted group (container) (typed FeaturePython)
  n = 3
  ref = N_element
FEATURE [App::DocumentObjectGroupPython] O_element633  label="O_element : 405"  # scripted group (container) (typed FeaturePython)
  n = 1
  ref = O_element
FEATURE [App::DocumentObjectGroupPython] G4_CYTOSINE  # scripted group (container) (typed FeaturePython)
  Dunit = g/cm3
  Dvalue = 1.55
  Group = -> [H_element673,C_element723,N_element323,O_element633]
  conduct = 2
  density = 1
  expand = 3
  formula = G4_CYTOSINE
  name = G4_CYTOSINE
  specific = 4
FEATURE [App::DocumentObjectGroupPython] H_element674  label="H_element : 438"  # scripted group (container) (typed FeaturePython)
  n = 6
  ref = H_element
FEATURE [App::DocumentObjectGroupPython] C_element724  label="C_element : 477"  # scripted group (container) (typed FeaturePython)
  n = 5
  ref = C_element
FEATURE [App::DocumentObjectGroupPython] N_element324  label="N_element : 176"  # scripted group (container) (typed FeaturePython)
  n = 2
  ref = N_element
FEATURE [App::DocumentObjectGroupPython] O_element634  label="O_element : 406"  # scripted group (container) (typed FeaturePython)
  n = 2
  ref = O_element
FEATURE [App::DocumentObjectGroupPython] G4_THYMINE  # scripted group (container) (typed FeaturePython)
  Dunit = g/cm3
  Dvalue = 1.23
  Group = -> [H_element674,C_element724,N_element324,O_element634]
  conduct = 2
  density = 1
  expand = 3
  formula = G4_THYMINE
  name = G4_THYMINE
  specific = 4
FEATURE [App::DocumentObjectGroupPython] H_element675  label="H_element : 439"  # scripted group (container) (typed FeaturePython)
  n = 4
  ref = H_element
FEATURE [App::DocumentObjectGroupPython] C_element725  label="C_element : 478"  # scripted group (container) (typed FeaturePython)
  n = 4
  ref = C_element
FEATURE [App::DocumentObjectGroupPython] N_element325  label="N_element : 177"  # scripted group (container) (typed FeaturePython)
  n = 2
  ref = N_element
FEATURE [App::DocumentObjectGroupPython] O_element635  label="O_element : 407"  # scripted group (container) (typed FeaturePython)
  n = 2
  ref = O_element
FEATURE [App::DocumentObjectGroupPython] G4_URACIL  # scripted group (container) (typed FeaturePython)
  Dunit = g/cm3
  Dvalue = 1.32
  Group = -> [H_element675,C_element725,N_element325,O_element635]
  conduct = 2
  density = 1
  expand = 3
  formula = G4_URACIL
  name = G4_URACIL
  specific = 4
FEATURE [App::DocumentObjectGroupPython] H_element676  label="H_element : 440"  # scripted group (container) (typed FeaturePython)
  n = 4
  ref = H_element
FEATURE [App::DocumentObjectGroupPython] C_element726  label="C_element : 479"  # scripted group (container) (typed FeaturePython)
  n = 5
  ref = C_element
FEATURE [App::DocumentObjectGroupPython] N_element326  label="N_element : 178"  # scripted group (container) (typed FeaturePython)
  n = 5
  ref = N_element
FEATURE [App::DocumentObjectGroupPython] G4_DNA_ADENINE  # scripted group (container) (typed FeaturePython)
  Dunit = g/cm3
  Dvalue = 1
  Group = -> [H_element676,C_element726,N_element326]
  conduct = 2
  density = 1
  expand = 3
  formula = G4_DNA_ADENINE
  name = G4_DNA_ADENINE
  specific = 4
FEATURE [App::DocumentObjectGroupPython] H_element677  label="H_element : 441"  # scripted group (container) (typed FeaturePython)
  n = 4
  ref = H_element
FEATURE [App::DocumentObjectGroupPython] C_element727  label="C_element : 480"  # scripted group (container) (typed FeaturePython)
  n = 5
  ref = C_element
FEATURE [App::DocumentObjectGroupPython] N_element327  label="N_element : 179"  # scripted group (container) (typed FeaturePython)
  n = 5
  ref = N_element
FEATURE [App::DocumentObjectGroupPython] O_element636  label="O_element : 408"  # scripted group (container) (typed FeaturePython)
  n = 1
  ref = O_element
FEATURE [App::DocumentObjectGroupPython] G4_DNA_GUANINE  # scripted group (container) (typed FeaturePython)
  Dunit = g/cm3
  Dvalue = 1
  Group = -> [H_element677,C_element727,N_element327,O_element636]
  conduct = 2
  density = 1
  expand = 3
  formula = G4_DNA_GUANINE
  name = G4_DNA_GUANINE
  specific = 4
FEATURE [App::DocumentObjectGroupPython] H_element678  label="H_element : 442"  # scripted group (container) (typed FeaturePython)
  n = 4
  ref = H_element
FEATURE [App::DocumentObjectGroupPython] C_element728  label="C_element : 481"  # scripted group (container) (typed FeaturePython)
  n = 4
  ref = C_element
FEATURE [App::DocumentObjectGroupPython] N_element328  label="N_element : 180"  # scripted group (container) (typed FeaturePython)
  n = 3
  ref = N_element
FEATURE [App::DocumentObjectGroupPython] O_element637  label="O_element : 409"  # scripted group (container) (typed FeaturePython)
  n = 1
  ref = O_element
FEATURE [App::DocumentObjectGroupPython] G4_DNA_CYTOSINE  # scripted group (container) (typed FeaturePython)
  Dunit = g/cm3
  Dvalue = 1
  Group = -> [H_element678,C_element728,N_element328,O_element637]
  conduct = 2
  density = 1
  expand = 3
  formula = G4_DNA_CYTOSINE
  name = G4_DNA_CYTOSINE
  specific = 4
FEATURE [App::DocumentObjectGroupPython] H_element679  label="H_element : 443"  # scripted group (container) (typed FeaturePython)
  n = 5
  ref = H_element
FEATURE [App::DocumentObjectGroupPython] C_element729  label="C_element : 482"  # scripted group (container) (typed FeaturePython)
  n = 5
  ref = C_element
FEATURE [App::DocumentObjectGroupPython] N_element329  label="N_element : 181"  # scripted group (container) (typed FeaturePython)
  n = 2
  ref = N_element
FEATURE [App::DocumentObjectGroupPython] O_element638  label="O_element : 410"  # scripted group (container) (typed FeaturePython)
  n = 2
  ref = O_element
FEATURE [App::DocumentObjectGroupPython] G4_DNA_THYMINE  # scripted group (container) (typed FeaturePython)
  Dunit = g/cm3
  Dvalue = 1
  Group = -> [H_element679,C_element729,N_element329,O_element638]
  conduct = 2
  density = 1
  expand = 3
  formula = G4_DNA_THYMINE
  name = G4_DNA_THYMINE
  specific = 4
FEATURE [App::DocumentObjectGroupPython] H_element680  label="H_element : 444"  # scripted group (container) (typed FeaturePython)
  n = 3
  ref = H_element
FEATURE [App::DocumentObjectGroupPython] C_element730  label="C_element : 483"  # scripted group (container) (typed FeaturePython)
  n = 4
  ref = C_element
FEATURE [App::DocumentObjectGroupPython] N_element330  label="N_element : 182"  # scripted group (container) (typed FeaturePython)
  n = 2
  ref = N_element
FEATURE [App::DocumentObjectGroupPython] O_element639  label="O_element : 411"  # scripted group (container) (typed FeaturePython)
  n = 2
  ref = O_element
FEATURE [App::DocumentObjectGroupPython] G4_DNA_URACIL  # scripted group (container) (typed FeaturePython)
  Dunit = g/cm3
  Dvalue = 1
  Group = -> [H_element680,C_element730,N_element330,O_element639]
  conduct = 2
  density = 1
  expand = 3
  formula = G4_DNA_URACIL
  name = G4_DNA_URACIL
  specific = 4
FEATURE [App::DocumentObjectGroupPython] H_element681  label="H_element : 445"  # scripted group (container) (typed FeaturePython)
  n = 10
  ref = H_element
FEATURE [App::DocumentObjectGroupPython] C_element731  label="C_element : 484"  # scripted group (container) (typed FeaturePython)
  n = 10
  ref = C_element
FEATURE [App::DocumentObjectGroupPython] N_element331  label="N_element : 183"  # scripted group (container) (typed FeaturePython)
  n = 5
  ref = N_element
FEATURE [App::DocumentObjectGroupPython] O_element640  label="O_element : 412"  # scripted group (container) (typed FeaturePython)
  n = 4
  ref = O_element
FEATURE [App::DocumentObjectGroupPython] G4_DNA_ADENOSINE  # scripted group (container) (typed FeaturePython)
  Dunit = g/cm3
  Dvalue = 1
  Group = -> [H_element681,C_element731,N_element331,O_element640]
  conduct = 2
  density = 1
  expand = 3
  formula = G4_DNA_ADENOSINE
  name = G4_DNA_ADENOSINE
  specific = 4
FEATURE [App::DocumentObjectGroupPython] H_element682  label="H_element : 446"  # scripted group (container) (typed FeaturePython)
  n = 10
  ref = H_element
FEATURE [App::DocumentObjectGroupPython] C_element732  label="C_element : 485"  # scripted group (container) (typed FeaturePython)
  n = 10
  ref = C_element
FEATURE [App::DocumentObjectGroupPython] N_element332  label="N_element : 184"  # scripted group (container) (typed FeaturePython)
  n = 5
  ref = N_element
FEATURE [App::DocumentObjectGroupPython] O_element641  label="O_element : 413"  # scripted group (container) (typed FeaturePython)
  n = 5
  ref = O_element
FEATURE [App::DocumentObjectGroupPython] G4_DNA_GUANOSINE  # scripted group (container) (typed FeaturePython)
  Dunit = g/cm3
  Dvalue = 1
  Group = -> [H_element682,C_element732,N_element332,O_element641]
  conduct = 2
  density = 1
  expand = 3
  formula = G4_DNA_GUANOSINE
  name = G4_DNA_GUANOSINE
  specific = 4
FEATURE [App::DocumentObjectGroupPython] H_element683  label="H_element : 447"  # scripted group (container) (typed FeaturePython)
  n = 10
  ref = H_element
FEATURE [App::DocumentObjectGroupPython] C_element733  label="C_element : 486"  # scripted group (container) (typed FeaturePython)
  n = 9
  ref = C_element
FEATURE [App::DocumentObjectGroupPython] N_element333  label="N_element : 185"  # scripted group (container) (typed FeaturePython)
  n = 3
  ref = N_element
FEATURE [App::DocumentObjectGroupPython] O_element642  label="O_element : 414"  # scripted group (container) (typed FeaturePython)
  n = 5
  ref = O_element
FEATURE [App::DocumentObjectGroupPython] G4_DNA_CYTIDINE  # scripted group (container) (typed FeaturePython)
  Dunit = g/cm3
  Dvalue = 1
  Group = -> [H_element683,C_element733,N_element333,O_element642]
  conduct = 2
  density = 1
  expand = 3
  formula = G4_DNA_CYTIDINE
  name = G4_DNA_CYTIDINE
  specific = 4
FEATURE [App::DocumentObjectGroupPython] H_element684  label="H_element : 448"  # scripted group (container) (typed FeaturePython)
  n = 9
  ref = H_element
FEATURE [App::DocumentObjectGroupPython] C_element734  label="C_element : 487"  # scripted group (container) (typed FeaturePython)
  n = 9
  ref = C_element
FEATURE [App::DocumentObjectGroupPython] N_element334  label="N_element : 186"  # scripted group (container) (typed FeaturePython)
  n = 2
  ref = N_element
FEATURE [App::DocumentObjectGroupPython] O_element643  label="O_element : 415"  # scripted group (container) (typed FeaturePython)
  n = 6
  ref = O_element
FEATURE [App::DocumentObjectGroupPython] G4_DNA_URIDINE  # scripted group (container) (typed FeaturePython)
  Dunit = g/cm3
  Dvalue = 1
  Group = -> [H_element684,C_element734,N_element334,O_element643]
  conduct = 2
  density = 1
  expand = 3
  formula = G4_DNA_URIDINE
  name = G4_DNA_URIDINE
  specific = 4
FEATURE [App::DocumentObjectGroupPython] H_element685  label="H_element : 449"  # scripted group (container) (typed FeaturePython)
  n = 11
  ref = H_element
FEATURE [App::DocumentObjectGroupPython] C_element735  label="C_element : 488"  # scripted group (container) (typed FeaturePython)
  n = 10
  ref = C_element
FEATURE [App::DocumentObjectGroupPython] N_element335  label="N_element : 187"  # scripted group (container) (typed FeaturePython)
  n = 2
  ref = N_element
FEATURE [App::DocumentObjectGroupPython] O_element644  label="O_element : 416"  # scripted group (container) (typed FeaturePython)
  n = 6
  ref = O_element
FEATURE [App::DocumentObjectGroupPython] G4_DNA_METHYLURIDINE  # scripted group (container) (typed FeaturePython)
  Dunit = g/cm3
  Dvalue = 1
  Group = -> [H_element685,C_element735,N_element335,O_element644]
  conduct = 2
  density = 1
  expand = 3
  formula = G4_DNA_METHYLURIDINE
  name = G4_DNA_METHYLURIDINE
  specific = 4
FEATURE [App::DocumentObjectGroupPython] P_element090  label="P_element : 034"  # scripted group (container) (typed FeaturePython)
  n = 1
  ref = P_element
FEATURE [App::DocumentObjectGroupPython] O_element645  label="O_element : 417"  # scripted group (container) (typed FeaturePython)
  n = 3
  ref = O_element
FEATURE [App::DocumentObjectGroupPython] G4_DNA_MONOPHOSPHATE  # scripted group (container) (typed FeaturePython)
  Dunit = g/cm3
  Dvalue = 1
  Group = -> [P_element090,O_element645]
  conduct = 2
  density = 1
  expand = 3
  formula = G4_DNA_MONOPHOSPHATE
  name = G4_DNA_MONOPHOSPHATE
  specific = 4
FEATURE [App::DocumentObjectGroupPython] H_element686  label="H_element : 450"  # scripted group (container) (typed FeaturePython)
  n = 10
  ref = H_element
FEATURE [App::DocumentObjectGroupPython] C_element736  label="C_element : 489"  # scripted group (container) (typed FeaturePython)
  n = 10
  ref = C_element
FEATURE [App::DocumentObjectGroupPython] N_element336  label="N_element : 188"  # scripted group (container) (typed FeaturePython)
  n = 5
  ref = N_element
FEATURE [App::DocumentObjectGroupPython] O_element646  label="O_element : 418"  # scripted group (container) (typed FeaturePython)
  n = 7
  ref = O_element
FEATURE [App::DocumentObjectGroupPython] P_element091  label="P_element : 035"  # scripted group (container) (typed FeaturePython)
  n = 1
  ref = P_element
FEATURE [App::DocumentObjectGroupPython] G4_DNA_A  # scripted group (container) (typed FeaturePython)
  Dunit = g/cm3
  Dvalue = 1
  Group = -> [H_element686,C_element736,N_element336,O_element646,P_element091]
  conduct = 2
  density = 1
  expand = 3
  formula = G4_DNA_A
  name = G4_DNA_A
  specific = 4
FEATURE [App::DocumentObjectGroupPython] H_element687  label="H_element : 451"  # scripted group (container) (typed FeaturePython)
  n = 10
  ref = H_element
FEATURE [App::DocumentObjectGroupPython] C_element737  label="C_element : 490"  # scripted group (container) (typed FeaturePython)
  n = 10
  ref = C_element
FEATURE [App::DocumentObjectGroupPython] N_element337  label="N_element : 189"  # scripted group (container) (typed FeaturePython)
  n = 5
  ref = N_element
FEATURE [App::DocumentObjectGroupPython] O_element647  label="O_element : 419"  # scripted group (container) (typed FeaturePython)
  n = 8
  ref = O_element
FEATURE [App::DocumentObjectGroupPython] P_element092  label="P_element : 036"  # scripted group (container) (typed FeaturePython)
  n = 1
  ref = P_element
FEATURE [App::DocumentObjectGroupPython] G4_DNA_G  # scripted group (container) (typed FeaturePython)
  Dunit = g/cm3
  Dvalue = 1
  Group = -> [H_element687,C_element737,N_element337,O_element647,P_element092]
  conduct = 2
  density = 1
  expand = 3
  formula = G4_DNA_G
  name = G4_DNA_G
  specific = 4
FEATURE [App::DocumentObjectGroupPython] H_element688  label="H_element : 452"  # scripted group (container) (typed FeaturePython)
  n = 10
  ref = H_element
FEATURE [App::DocumentObjectGroupPython] C_element738  label="C_element : 491"  # scripted group (container) (typed FeaturePython)
  n = 9
  ref = C_element
FEATURE [App::DocumentObjectGroupPython] N_element338  label="N_element : 190"  # scripted group (container) (typed FeaturePython)
  n = 3
  ref = N_element
FEATURE [App::DocumentObjectGroupPython] O_element648  label="O_element : 420"  # scripted group (container) (typed FeaturePython)
  n = 8
  ref = O_element
FEATURE [App::DocumentObjectGroupPython] P_element093  label="P_element : 037"  # scripted group (container) (typed FeaturePython)
  n = 1
  ref = P_element
FEATURE [App::DocumentObjectGroupPython] G4_DNA_C  # scripted group (container) (typed FeaturePython)
  Dunit = g/cm3
  Dvalue = 1
  Group = -> [H_element688,C_element738,N_element338,O_element648,P_element093]
  conduct = 2
  density = 1
  expand = 3
  formula = G4_DNA_C
  name = G4_DNA_C
  specific = 4
FEATURE [App::DocumentObjectGroupPython] H_element689  label="H_element : 453"  # scripted group (container) (typed FeaturePython)
  n = 9
  ref = H_element
FEATURE [App::DocumentObjectGroupPython] C_element739  label="C_element : 492"  # scripted group (container) (typed FeaturePython)
  n = 9
  ref = C_element
FEATURE [App::DocumentObjectGroupPython] N_element339  label="N_element : 191"  # scripted group (container) (typed FeaturePython)
  n = 2
  ref = N_element
FEATURE [App::DocumentObjectGroupPython] O_element649  label="O_element : 421"  # scripted group (container) (typed FeaturePython)
  n = 9
  ref = O_element
FEATURE [App::DocumentObjectGroupPython] P_element094  label="P_element : 038"  # scripted group (container) (typed FeaturePython)
  n = 1
  ref = P_element
FEATURE [App::DocumentObjectGroupPython] G4_DNA_U  # scripted group (container) (typed FeaturePython)
  Dunit = g/cm3
  Dvalue = 1
  Group = -> [H_element689,C_element739,N_element339,O_element649,P_element094]
  conduct = 2
  density = 1
  expand = 3
  formula = G4_DNA_U
  name = G4_DNA_U
  specific = 4
FEATURE [App::DocumentObjectGroupPython] H_element690  label="H_element : 454"  # scripted group (container) (typed FeaturePython)
  n = 11
  ref = H_element
FEATURE [App::DocumentObjectGroupPython] C_element740  label="C_element : 493"  # scripted group (container) (typed FeaturePython)
  n = 10
  ref = C_element
FEATURE [App::DocumentObjectGroupPython] N_element340  label="N_element : 192"  # scripted group (container) (typed FeaturePython)
  n = 2
  ref = N_element
FEATURE [App::DocumentObjectGroupPython] O_element650  label="O_element : 422"  # scripted group (container) (typed FeaturePython)
  n = 9
  ref = O_element
FEATURE [App::DocumentObjectGroupPython] P_element095  label="P_element : 039"  # scripted group (container) (typed FeaturePython)
  n = 1
  ref = P_element
FEATURE [App::DocumentObjectGroupPython] G4_DNA_MU  # scripted group (container) (typed FeaturePython)
  Dunit = g/cm3
  Dvalue = 1
  Group = -> [H_element690,C_element740,N_element340,O_element650,P_element095]
  conduct = 2
  density = 1
  expand = 3
  formula = G4_DNA_MU
  name = G4_DNA_MU
  specific = 4
FEATURE [App::DocumentObjectGroupPython] BioChemical  # scripted group (container) (typed FeaturePython)
  Group = -> [G4_CYTOSINE,G4_THYMINE,G4_URACIL,G4_DNA_ADENINE,G4_DNA_GUANINE,G4_DNA_CYTOSINE,G4_DNA_THYMINE,G4_DNA_URACIL,G4_DNA_ADENOSINE,G4_DNA_GUANOSINE,G4_DNA_CYTIDINE,G4_DNA_URIDINE,G4_DNA_METHYLURIDINE,G4_DNA_MONOPHOSPHATE,G4_DNA_A,G4_DNA_G,G4_DNA_C,G4_DNA_U,G4_DNA_MU]
FEATURE [App::DocumentObjectGroupPython] G4Materials  # scripted group (container) (typed FeaturePython)
  Group = -> [NIST,Element,HEP,Space,BioChemical]
FEATURE [App::DocumentObjectGroupPython] Geant4  # scripted group (container) (typed FeaturePython)
  Group = -> [G4Isotopes,G4Elements,G4Materials]
FEATURE [App::DocumentObjectGroupPython] Materials  # scripted group (container) (typed FeaturePython)
  Group = -> [Geant4]
